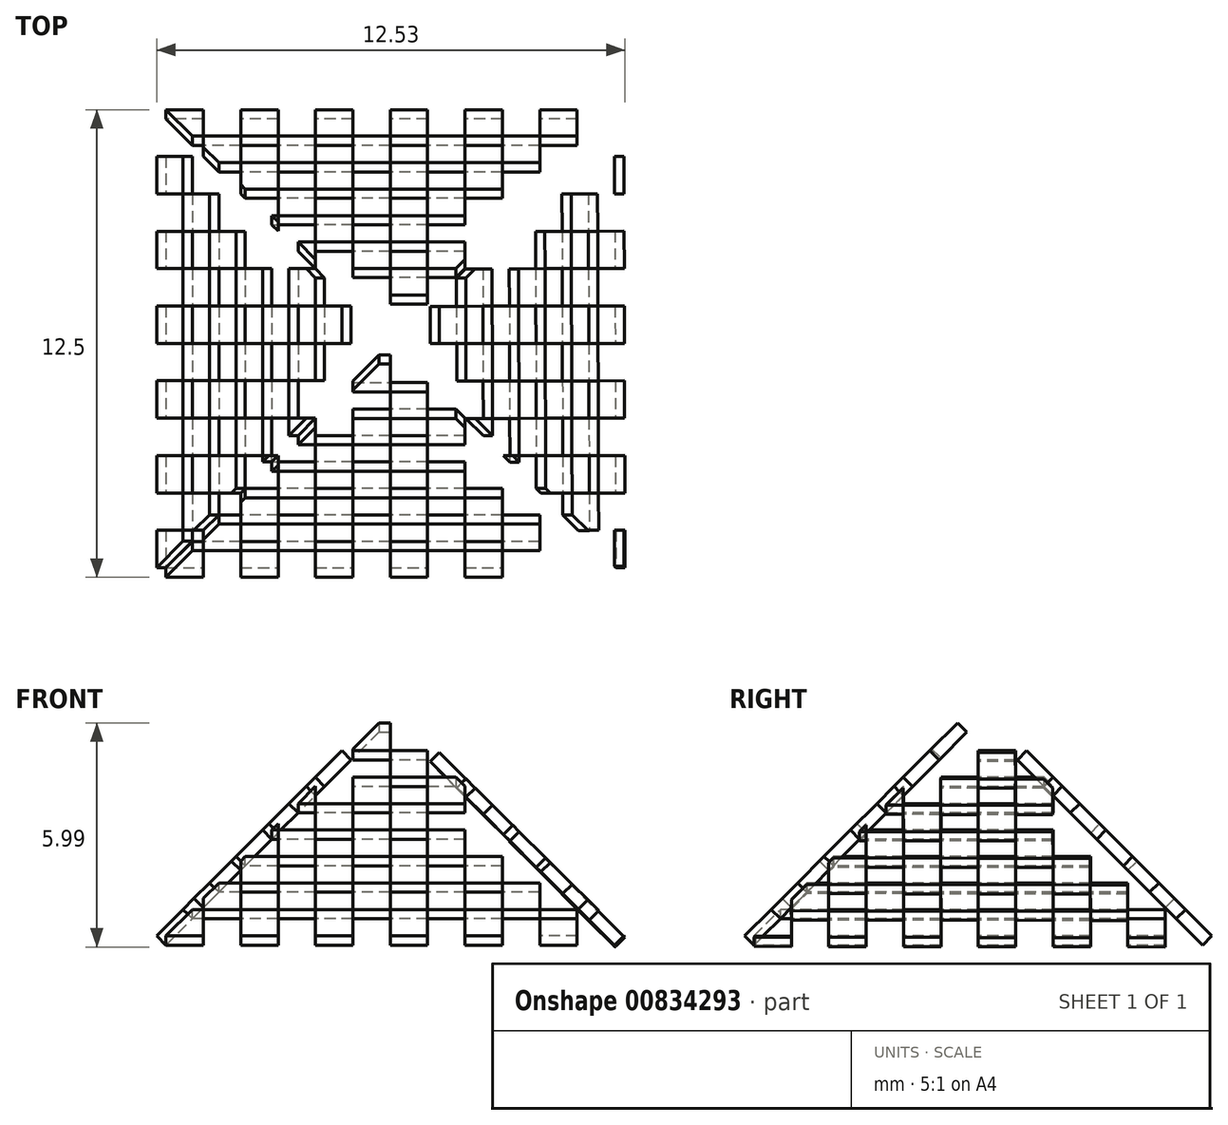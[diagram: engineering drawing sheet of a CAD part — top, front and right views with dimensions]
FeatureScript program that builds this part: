
annotation { "Feature Type Name" : "Feature", "Feature Type Description" : "" }
export const myFeature = defineFeature(function(context is Context, id is Id, definition is map)
    precondition{}
    {
        {
            var Q0;
            Q0=qCreatedBy(makeId("Front.planeOp"),FACE);
            var sketch = newSketch(context, id + "F7", { "sketchPlane" : qUnion([Q0])});
            skLineSegment(sketch, "E0.bottom", {"start": v(0, 0) * mm, "end": v(-1, 0) * mm});
            skLineSegment(sketch, "E0.top", {"start": v(-0.7, 1) * mm, "end": v(-1, 1) * mm});
            skLineSegment(sketch, "E0.right", {"start": v(-1, 0) * mm, "end": v(-1, 1) * mm});
            skLineSegment(sketch, "E1.bottom", {"start": v(-1, 1) * mm, "end": v(-2, 1) * mm});
            skLineSegment(sketch, "E1.left", {"start": v(-1, 1) * mm, "end": v(-1, 0) * mm});
            skLineSegment(sketch, "E1.right", {"start": v(-2, 1) * mm, "end": v(-2, 0) * mm});
            skLineSegment(sketch, "E2.bottom", {"start": v(-2, 1) * mm, "end": v(-3, 1) * mm});
            skLineSegment(sketch, "E2.top", {"start": v(-2, 0) * mm, "end": v(-3, 0) * mm});
            skLineSegment(sketch, "E2.right", {"start": v(-3, 1) * mm, "end": v(-3, 0) * mm});
            skLineSegment(sketch, "E3.bottom", {"start": v(-3, 1) * mm, "end": v(-4, 1) * mm});
            skLineSegment(sketch, "E3.right", {"start": v(-4, 1) * mm, "end": v(-4, 0) * mm});
            skLineSegment(sketch, "E4.bottom", {"start": v(-4, 1) * mm, "end": v(-5, 1) * mm});
            skLineSegment(sketch, "E4.top", {"start": v(-4, 0) * mm, "end": v(-5, 0) * mm});
            skLineSegment(sketch, "E4.right", {"start": v(-5, 1) * mm, "end": v(-5, 0) * mm});
            skLineSegment(sketch, "E5.bottom", {"start": v(-5, 1) * mm, "end": v(-6, 1) * mm});
            skLineSegment(sketch, "E5.right", {"start": v(-6, 1) * mm, "end": v(-6, 0) * mm});
            skLineSegment(sketch, "E6.bottom", {"start": v(-6, 1) * mm, "end": v(-7, 1) * mm});
            skLineSegment(sketch, "E6.top", {"start": v(-6, 0) * mm, "end": v(-7, 0) * mm});
            skLineSegment(sketch, "E6.right", {"start": v(-7, 1) * mm, "end": v(-7, 0) * mm});
            skLineSegment(sketch, "E7.bottom", {"start": v(-7, 1) * mm, "end": v(-8, 1) * mm});
            skLineSegment(sketch, "E7.right", {"start": v(-8, 1) * mm, "end": v(-8, 0) * mm});
            skLineSegment(sketch, "E8.bottom", {"start": v(-8, 1) * mm, "end": v(-9, 1) * mm});
            skLineSegment(sketch, "E8.top", {"start": v(-8, 0) * mm, "end": v(-9, 0) * mm});
            skLineSegment(sketch, "E8.right", {"start": v(-9, 1) * mm, "end": v(-9, 0) * mm});
            skLineSegment(sketch, "E9.bottom", {"start": v(-9, 1) * mm, "end": v(-10, 1) * mm});
            skLineSegment(sketch, "E9.right", {"start": v(-10, 1) * mm, "end": v(-10, 0) * mm});
            skLineSegment(sketch, "E10.bottom", {"start": v(-10, 1) * mm, "end": v(-11, 1) * mm});
            skLineSegment(sketch, "E10.top", {"start": v(-10, 0) * mm, "end": v(-11, 0) * mm});
            skLineSegment(sketch, "E10.right", {"start": v(-11, 1) * mm, "end": v(-11, 0) * mm});
            skLineSegment(sketch, "E11.bottom", {"start": v(-11, 1) * mm, "end": v(-11.3, 1) * mm});
            skLineSegment(sketch, "E12.right", {"start": v(-1, 1) * mm, "end": v(-1, 1.4) * mm});
            skLineSegment(sketch, "E13.bottom", {"start": v(-1.41, 2) * mm, "end": v(-2, 2) * mm});
            skLineSegment(sketch, "E13.left", {"start": v(-1, 1.4) * mm, "end": v(-1, 1) * mm});
            skLineSegment(sketch, "E13.right", {"start": v(-2, 2) * mm, "end": v(-2, 1) * mm});
            skLineSegment(sketch, "E14.bottom", {"start": v(-2, 2) * mm, "end": v(-3, 2) * mm});
            skLineSegment(sketch, "E14.right", {"start": v(-3, 2) * mm, "end": v(-3, 1) * mm});
            skLineSegment(sketch, "E15.bottom", {"start": v(-3, 2) * mm, "end": v(-4, 2) * mm});
            skLineSegment(sketch, "E15.right", {"start": v(-4, 2) * mm, "end": v(-4, 1) * mm});
            skLineSegment(sketch, "E16.bottom", {"start": v(-4, 2) * mm, "end": v(-5, 2) * mm});
            skLineSegment(sketch, "E16.right", {"start": v(-5, 2) * mm, "end": v(-5, 1) * mm});
            skLineSegment(sketch, "E17.bottom", {"start": v(-5, 2) * mm, "end": v(-6, 2) * mm});
            skLineSegment(sketch, "E17.right", {"start": v(-6, 2) * mm, "end": v(-6, 1) * mm});
            skLineSegment(sketch, "E18.right", {"start": v(-7, 2) * mm, "end": v(-7, 1) * mm});
            skLineSegment(sketch, "E19.bottom", {"start": v(-7, 2) * mm, "end": v(-8, 2) * mm});
            skLineSegment(sketch, "E19.right", {"start": v(-8, 2) * mm, "end": v(-8, 1) * mm});
            skLineSegment(sketch, "E20.bottom", {"start": v(-8, 2) * mm, "end": v(-9, 2) * mm});
            skLineSegment(sketch, "E20.right", {"start": v(-9, 2) * mm, "end": v(-9, 1) * mm});
            skLineSegment(sketch, "E21.bottom", {"start": v(-9, 2) * mm, "end": v(-10, 2) * mm});
            skLineSegment(sketch, "E21.right", {"start": v(-10, 2) * mm, "end": v(-10, 1) * mm});
            skLineSegment(sketch, "E22.bottom", {"start": v(-10, 2) * mm, "end": v(-10.59, 2) * mm});
            skLineSegment(sketch, "E22.right", {"start": v(-11, 1.41) * mm, "end": v(-11, 1) * mm});
            skLineSegment(sketch, "E23.right", {"start": v(-2, 2.83) * mm, "end": v(-2, 2) * mm});
            skLineSegment(sketch, "E24.bottom", {"start": v(-2.12, 3) * mm, "end": v(-3, 3) * mm});
            skLineSegment(sketch, "E24.right", {"start": v(-3, 3) * mm, "end": v(-3, 2) * mm});
            skLineSegment(sketch, "E25.bottom", {"start": v(-3, 3) * mm, "end": v(-4, 3) * mm});
            skLineSegment(sketch, "E25.right", {"start": v(-4, 3) * mm, "end": v(-4, 2) * mm});
            skLineSegment(sketch, "E26.bottom", {"start": v(-4, 3) * mm, "end": v(-5, 3) * mm});
            skLineSegment(sketch, "E26.right", {"start": v(-5, 3) * mm, "end": v(-5, 2) * mm});
            skLineSegment(sketch, "E27.right", {"start": v(-6, 3) * mm, "end": v(-6, 2) * mm});
            skLineSegment(sketch, "E28.bottom", {"start": v(-6, 3) * mm, "end": v(-7, 3) * mm});
            skLineSegment(sketch, "E28.top", {"start": v(-6, 2) * mm, "end": v(-7, 2) * mm});
            skLineSegment(sketch, "E28.right", {"start": v(-7, 3) * mm, "end": v(-7, 2) * mm});
            skLineSegment(sketch, "E29.bottom", {"start": v(-7, 3) * mm, "end": v(-8, 3) * mm});
            skLineSegment(sketch, "E29.right", {"start": v(-8, 3) * mm, "end": v(-8, 2) * mm});
            skLineSegment(sketch, "E30.bottom", {"start": v(-8, 3) * mm, "end": v(-9, 3) * mm});
            skLineSegment(sketch, "E30.right", {"start": v(-9, 3) * mm, "end": v(-9, 2) * mm});
            skLineSegment(sketch, "E31.bottom", {"start": v(-9, 3) * mm, "end": v(-9.88, 3) * mm});
            skLineSegment(sketch, "E31.right", {"start": v(-10, 2.83) * mm, "end": v(-10, 2) * mm});
            skLineSegment(sketch, "E32.right", {"start": v(-3, 4) * mm, "end": v(-3, 3) * mm});
            skLineSegment(sketch, "E33.bottom", {"start": v(-3, 4) * mm, "end": v(-4, 4) * mm});
            skLineSegment(sketch, "E33.right", {"start": v(-4, 4) * mm, "end": v(-4, 3) * mm});
            skLineSegment(sketch, "E34.bottom", {"start": v(-4, 4) * mm, "end": v(-5, 4) * mm});
            skLineSegment(sketch, "E34.right", {"start": v(-5, 4) * mm, "end": v(-5, 3) * mm});
            skLineSegment(sketch, "E35.bottom", {"start": v(-5, 4) * mm, "end": v(-6, 4) * mm});
            skLineSegment(sketch, "E35.top", {"start": v(-5, 3) * mm, "end": v(-6, 3) * mm});
            skLineSegment(sketch, "E35.right", {"start": v(-6, 4) * mm, "end": v(-6, 3) * mm});
            skLineSegment(sketch, "E36.bottom", {"start": v(-6, 4) * mm, "end": v(-7, 4) * mm});
            skLineSegment(sketch, "E36.right", {"start": v(-7, 4) * mm, "end": v(-7, 3) * mm});
            skLineSegment(sketch, "E37.bottom", {"start": v(-7, 4) * mm, "end": v(-8, 4) * mm});
            skLineSegment(sketch, "E37.right", {"start": v(-8, 4) * mm, "end": v(-8, 3) * mm});
            skLineSegment(sketch, "E38.bottom", {"start": v(-8, 4) * mm, "end": v(-9, 4) * mm});
            skLineSegment(sketch, "E38.right", {"start": v(-9, 4) * mm, "end": v(-9, 3) * mm});
            skLineSegment(sketch, "E39.right", {"start": v(-4, 5) * mm, "end": v(-4, 4) * mm});
            skLineSegment(sketch, "E40.bottom", {"start": v(-4, 5) * mm, "end": v(-5, 5) * mm});
            skLineSegment(sketch, "E40.right", {"start": v(-5, 5) * mm, "end": v(-5, 4) * mm});
            skLineSegment(sketch, "E41.bottom", {"start": v(-5, 5) * mm, "end": v(-6, 5) * mm});
            skLineSegment(sketch, "E41.right", {"start": v(-6, 5) * mm, "end": v(-6, 4) * mm});
            skLineSegment(sketch, "E42.bottom", {"start": v(-6, 5) * mm, "end": v(-7, 5) * mm});
            skLineSegment(sketch, "E42.right", {"start": v(-7, 5) * mm, "end": v(-7, 4) * mm});
            skLineSegment(sketch, "E43.bottom", {"start": v(-7, 5) * mm, "end": v(-8, 5) * mm});
            skLineSegment(sketch, "E43.right", {"start": v(-8, 5) * mm, "end": v(-8, 4) * mm});
            skLineSegment(sketch, "E44.right", {"start": v(-5, 6) * mm, "end": v(-5, 5) * mm});
            skLineSegment(sketch, "E45.bottom", {"start": v(-5, 6) * mm, "end": v(-6, 6) * mm});
            skLineSegment(sketch, "E45.right", {"start": v(-6, 6) * mm, "end": v(-6, 5) * mm});
            skLineSegment(sketch, "E46.right", {"start": v(-7, 6) * mm, "end": v(-7, 5) * mm});
            skLineSegment(sketch, "E47.top", {"start": v(-2, 2) * mm, "end": v(-1.41, 2) * mm});
            skLineSegment(sketch, "E48.bottom", {"start": v(-3, 4) * mm, "end": v(-2.83, 4) * mm});
            skLineSegment(sketch, "E48.top", {"start": v(-3, 3) * mm, "end": v(-2.12, 3) * mm});
            skLineSegment(sketch, "E49.bottom", {"start": v(-4, 5) * mm, "end": v(-3.54, 5) * mm});
            skLineSegment(sketch, "E49.top", {"start": v(-4, 4) * mm, "end": v(-3, 4) * mm});
            skLineSegment(sketch, "E49.right", {"start": v(-3, 4.24) * mm, "end": v(-3, 4) * mm});
            skLineSegment(sketch, "E50.top", {"start": v(-4.24, 6) * mm, "end": v(-5, 6) * mm});
            skLineSegment(sketch, "E50.left", {"start": v(-4, 5) * mm, "end": v(-4, 5.65) * mm});
            skLineSegment(sketch, "E50.right", {"start": v(-5, 5) * mm, "end": v(-5, 6) * mm});
            skLineSegment(sketch, "E51.right", {"start": v(-5, 6) * mm, "end": v(-5, 7) * mm});
            skLineSegment(sketch, "E52.bottom", {"start": v(-8, 5) * mm, "end": v(-7, 5) * mm});
            skLineSegment(sketch, "E52.top", {"start": v(-7.76, 6) * mm, "end": v(-7, 6) * mm});
            skLineSegment(sketch, "E52.right", {"start": v(-7, 5) * mm, "end": v(-7, 6) * mm});
            skLineSegment(sketch, "E53.bottom", {"start": v(-5, 7) * mm, "end": v(-6, 7) * mm});
            skLineSegment(sketch, "E53.left", {"start": v(-5, 7) * mm, "end": v(-5, 6) * mm});
            skLineSegment(sketch, "E53.right", {"start": v(-6, 7) * mm, "end": v(-6, 6) * mm});
            skLineSegment(sketch, "E54.top", {"start": v(-6, 6) * mm, "end": v(-7, 6) * mm});
            skLineSegment(sketch, "E54.right", {"start": v(-7, 7) * mm, "end": v(-7, 6) * mm});
            skLineSegment(sketch, "E55.top", {"start": v(-7, 6) * mm, "end": v(-7.76, 6) * mm});
            skLineSegment(sketch, "E56.right", {"start": v(-5, 7) * mm, "end": v(-5, 7.07) * mm});
            skLineSegment(sketch, "E57.bottom", {"start": v(-6, 7) * mm, "end": v(-5, 7) * mm});
            skLineSegment(sketch, "E57.top", {"start": v(-6, 8.05) * mm, "end": v(-5.7, 8.05) * mm});
            skLineSegment(sketch, "E57.left", {"start": v(-6, 7) * mm, "end": v(-6, 8.05) * mm});
            skLineSegment(sketch, "E58.bottom", {"start": v(-7, 7) * mm, "end": v(-6, 7) * mm});
            skLineSegment(sketch, "E58.top", {"start": v(-6.3, 8.05) * mm, "end": v(-6, 8.05) * mm});
            skLineSegment(sketch, "E58.left", {"start": v(-7, 7) * mm, "end": v(-7, 7.07) * mm});
            skLineSegment(sketch, "E59.bottom", {"start": v(-10.59, 2) * mm, "end": v(-10, 2) * mm});
            skLineSegment(sketch, "E59.right", {"start": v(-10, 2) * mm, "end": v(-10, 2.83) * mm});
            skLineSegment(sketch, "E60.bottom", {"start": v(-9.88, 3) * mm, "end": v(-9, 3) * mm});
            skLineSegment(sketch, "E60.top", {"start": v(-9.17, 4) * mm, "end": v(-9, 4) * mm});
            skLineSegment(sketch, "E60.right", {"start": v(-9, 3) * mm, "end": v(-9, 4) * mm});
            skLineSegment(sketch, "E61.bottom", {"start": v(-9, 4) * mm, "end": v(-8, 4) * mm});
            skLineSegment(sketch, "E61.top", {"start": v(-8.46, 5) * mm, "end": v(-8, 5) * mm});
            skLineSegment(sketch, "E61.left", {"start": v(-9, 4) * mm, "end": v(-9, 4.24) * mm});
            skLineSegment(sketch, "E61.right", {"start": v(-8, 4) * mm, "end": v(-8, 5) * mm});
            skLineSegment(sketch, "E62.right", {"start": v(-8, 5) * mm, "end": v(-8, 5.65) * mm});
            skLineSegment(sketch, "E63.bottom", {"start": v(-11.3, 1) * mm, "end": v(-11, 1) * mm});
            skLineSegment(sketch, "E63.right", {"start": v(-11, 1) * mm, "end": v(-11, 1.41) * mm});
            skLineSegment(sketch, "E64.bottom", {"start": v(-2.83, 4) * mm, "end": v(-3, 4) * mm});
            skLineSegment(sketch, "E64.right", {"start": v(-3, 4) * mm, "end": v(-3, 4.24) * mm});
            skLineSegment(sketch, "E65.left", {"start": v(-4, 5.65) * mm, "end": v(-4, 5) * mm});
            skLineSegment(sketch, "E66.bottom", {"start": v(-7, 7) * mm, "end": v(-7.05, 7) * mm});
            skLineSegment(sketch, "E67.bottom", {"start": v(-7.05, 7) * mm, "end": v(-7, 7) * mm});
            skLineSegment(sketch, "E68.bottom", {"start": v(-4.95, 7) * mm, "end": v(-5, 7) * mm});
            skLineSegment(sketch, "E69.bottom", {"start": v(-5.7, 8.05) * mm, "end": v(-6, 8.05) * mm});
            skLineSegment(sketch, "E69.right", {"start": v(-6, 8.05) * mm, "end": v(-6, 8.48) * mm});
            skLineSegment(sketch, "E70", {"start": v(-12, 0) * mm, "end": v(-11, 1.41) * mm});
            skLineSegment(sketch, "E71", {"start": v(-5.7, 8.05) * mm, "end": v(-5, 7.07) * mm});
            skLineSegment(sketch, "E72.trimOffspring", {"start": v(-10.59, 2) * mm, "end": v(-10, 2.83) * mm});
            skLineSegment(sketch, "E73.trimOffspring", {"start": v(-9.88, 3) * mm, "end": v(-9.17, 4) * mm});
            skLineSegment(sketch, "E74.trimOffspring", {"start": v(-9, 4.24) * mm, "end": v(-8.46, 5) * mm});
            skLineSegment(sketch, "E75.trimOffspring", {"start": v(-8, 5.65) * mm, "end": v(-7.76, 6) * mm});
            skLineSegment(sketch, "E76.trimOffspring", {"start": v(-7.05, 7) * mm, "end": v(-7, 7.07) * mm});
            skLineSegment(sketch, "E77.trimOffspring", {"start": v(-6.3, 8.05) * mm, "end": v(-6, 8.48) * mm});
            skLineSegment(sketch, "E78.trimOffspring", {"start": v(-4.95, 7) * mm, "end": v(-4.24, 6) * mm});
            skLineSegment(sketch, "E79.trimOffspring", {"start": v(-0.7, 1) * mm, "end": v(0, 0) * mm});
            skLineSegment(sketch, "E80.trimOffspring", {"start": v(-1.41, 2) * mm, "end": v(-1, 1.4) * mm});
            skLineSegment(sketch, "E81.trimOffspring", {"start": v(-2.12, 3) * mm, "end": v(-2, 2.83) * mm});
            skLineSegment(sketch, "E82.trimOffspring", {"start": v(-3, 4.24) * mm, "end": v(-2.83, 4) * mm});
            skLineSegment(sketch, "E83.trimOffspring", {"start": v(-4, 5.65) * mm, "end": v(-3.54, 5) * mm});
            skLineSegment(sketch, "E84", {"start": v(-6, 8.48) * mm, "end": v(0, 0) * mm});
            skLineSegment(sketch, "E85", {"start": v(-6, 8.48) * mm, "end": v(-12, 0) * mm});
            skLineSegment(sketch, "E86", {"start": v(-12, 0) * mm, "end": v(0, 0) * mm});
            skSolve(sketch);
        }
        {
            var Q0;
            {var subQ0=sQuery(id+"F7.wireOp",EDGE,"E10.right");Q0=makeQuery(id+"F7.imprint","IMPRINT",FACE,{"disambiguationData":[TD([[makeQuery(id+"F7.imprint","IMPRINT",EDGE,{"derivedFrom":subQ0}),-1.0]])]});}
            var Q1;
            Q1=makeQuery(id+"F7.imprint","IMPRINT",FACE,{"disambiguationData":[TD([[makeQuery(id+"F7.imprint","IMPRINT",EDGE,{"derivedFrom":sQuery(id+"F7.wireOp",EDGE,"E10.bottom")}),-1.0]])]});
            var Q2;
            Q2=makeQuery(id+"F7.imprint","IMPRINT",FACE,{"disambiguationData":[TD([[makeQuery(id+"F7.imprint","IMPRINT",EDGE,{"derivedFrom":sQuery(id+"F7.wireOp",EDGE,"E21.bottom")}),-1.0]])]});
            var Q3;
            {var subQ0=sQuery(id+"F7.wireOp",EDGE,"E8.right");Q3=makeQuery(id+"F7.imprint","IMPRINT",FACE,{"disambiguationData":[TD([[makeQuery(id+"F7.imprint","IMPRINT",EDGE,{"derivedFrom":subQ0}),-1.0]])]});}
            var Q4;
            Q4=makeQuery(id+"F7.imprint","IMPRINT",FACE,{"disambiguationData":[TD([[makeQuery(id+"F7.imprint","IMPRINT",EDGE,{"derivedFrom":sQuery(id+"F7.wireOp",EDGE,"E8.bottom")}),-1.0]])]});
            var Q5;
            Q5=makeQuery(id+"F7.imprint","IMPRINT",FACE,{"disambiguationData":[TD([[makeQuery(id+"F7.imprint","IMPRINT",EDGE,{"derivedFrom":sQuery(id+"F7.wireOp",EDGE,"E19.bottom")}),-1.0]])]});
            var Q6;
            Q6=makeQuery(id+"F7.imprint","IMPRINT",FACE,{"disambiguationData":[TD([[makeQuery(id+"F7.imprint","IMPRINT",EDGE,{"derivedFrom":sQuery(id+"F7.wireOp",EDGE,"E30.bottom")}),-1.0]])]});
            var Q7;
            Q7=makeQuery(id+"F7.imprint","IMPRINT",FACE,{"disambiguationData":[TD([[makeQuery(id+"F7.imprint","IMPRINT",EDGE,{"derivedFrom":sQuery(id+"F7.wireOp",EDGE,"E37.bottom")}),-1.0]])]});
            var Q8;
            {var subQ0=sQuery(id+"F7.wireOp",EDGE,"E61.top");Q8=makeQuery(id+"F7.imprint","IMPRINT",FACE,{"disambiguationData":[TD([[makeQuery(id+"F7.imprint","IMPRINT",EDGE,{"derivedFrom":subQ0}),1.0]])]});}
            var Q9;
            Q9=makeQuery(id+"F7.imprint","IMPRINT",FACE,{"disambiguationData":[TD([[makeQuery(id+"F7.imprint","IMPRINT",EDGE,{"derivedFrom":sQuery(id+"F7.wireOp",EDGE,"E42.bottom")}),-1.0]])]});
            var Q10;
            {var subQ0=sQuery(id+"F7.wireOp",EDGE,"E55.top");Q10=makeQuery(id+"F7.imprint","IMPRINT",FACE,{"disambiguationData":[TD([[makeQuery(id+"F7.imprint","IMPRINT",EDGE,{"derivedFrom":subQ0}),-1.0]])]});}
            var Q11;
            Q11=makeQuery(id+"F7.imprint","IMPRINT",FACE,{"disambiguationData":[TD([[makeQuery(id+"F7.imprint","IMPRINT",EDGE,{"derivedFrom":sQuery(id+"F7.wireOp",EDGE,"E58.bottom")}),1.0]])]});
            var Q12;
            {var subQ0=sQuery(id+"F7.wireOp",EDGE,"E69.bottom");Q12=makeQuery(id+"F7.imprint","IMPRINT",FACE,{"disambiguationData":[TD([[makeQuery(id+"F7.imprint","IMPRINT",EDGE,{"derivedFrom":subQ0}),-1.0]])]});}
            var Q13;
            Q13=makeQuery(id+"F7.imprint","IMPRINT",FACE,{"disambiguationData":[TD([[makeQuery(id+"F7.imprint","IMPRINT",EDGE,{"derivedFrom":sQuery(id+"F7.wireOp",EDGE,"E45.bottom")}),-1.0]])]});
            var Q14;
            Q14=makeQuery(id+"F7.imprint","IMPRINT",FACE,{"disambiguationData":[TD([[makeQuery(id+"F7.imprint","IMPRINT",EDGE,{"derivedFrom":sQuery(id+"F7.wireOp",EDGE,"E40.bottom")}),-1.0]])]});
            var Q15;
            Q15=makeQuery(id+"F7.imprint","IMPRINT",FACE,{"disambiguationData":[TD([[makeQuery(id+"F7.imprint","IMPRINT",EDGE,{"derivedFrom":sQuery(id+"F7.wireOp",EDGE,"E35.bottom")}),-1.0]])]});
            var Q16;
            Q16=makeQuery(id+"F7.imprint","IMPRINT",FACE,{"disambiguationData":[TD([[makeQuery(id+"F7.imprint","IMPRINT",EDGE,{"derivedFrom":sQuery(id+"F7.wireOp",EDGE,"E28.bottom")}),-1.0]])]});
            var Q17;
            Q17=makeQuery(id+"F7.imprint","IMPRINT",FACE,{"disambiguationData":[TD([[makeQuery(id+"F7.imprint","IMPRINT",EDGE,{"derivedFrom":sQuery(id+"F7.wireOp",EDGE,"E17.bottom")}),-1.0]])]});
            var Q18;
            Q18=makeQuery(id+"F7.imprint","IMPRINT",FACE,{"disambiguationData":[TD([[makeQuery(id+"F7.imprint","IMPRINT",EDGE,{"derivedFrom":sQuery(id+"F7.wireOp",EDGE,"E6.bottom")}),-1.0]])]});
            var Q19;
            {var subQ0=sQuery(id+"F7.wireOp",EDGE,"E6.right");Q19=makeQuery(id+"F7.imprint","IMPRINT",FACE,{"disambiguationData":[TD([[makeQuery(id+"F7.imprint","IMPRINT",EDGE,{"derivedFrom":subQ0}),-1.0]])]});}
            var Q20;
            Q20=makeQuery(id+"F7.imprint","IMPRINT",FACE,{"disambiguationData":[TD([[makeQuery(id+"F7.imprint","IMPRINT",EDGE,{"derivedFrom":sQuery(id+"F7.wireOp",EDGE,"E26.bottom")}),-1.0]])]});
            var Q21;
            Q21=makeQuery(id+"F7.imprint","IMPRINT",FACE,{"disambiguationData":[TD([[makeQuery(id+"F7.imprint","IMPRINT",EDGE,{"derivedFrom":sQuery(id+"F7.wireOp",EDGE,"E49.top")}),1.0]])]});
            var Q22;
            {var subQ0=sQuery(id+"F7.wireOp",EDGE,"E48.top");Q22=makeQuery(id+"F7.imprint","IMPRINT",FACE,{"disambiguationData":[TD([[makeQuery(id+"F7.imprint","IMPRINT",EDGE,{"derivedFrom":subQ0}),1.0]])]});}
            var Q23;
            Q23=makeQuery(id+"F7.imprint","IMPRINT",FACE,{"disambiguationData":[TD([[makeQuery(id+"F7.imprint","IMPRINT",EDGE,{"derivedFrom":sQuery(id+"F7.wireOp",EDGE,"E15.bottom")}),-1.0]])]});
            var Q24;
            Q24=makeQuery(id+"F7.imprint","IMPRINT",FACE,{"disambiguationData":[TD([[makeQuery(id+"F7.imprint","IMPRINT",EDGE,{"derivedFrom":sQuery(id+"F7.wireOp",EDGE,"E4.bottom")}),-1.0]])]});
            var Q25;
            {var subQ0=sQuery(id+"F7.wireOp",EDGE,"E4.right");Q25=makeQuery(id+"F7.imprint","IMPRINT",FACE,{"disambiguationData":[TD([[makeQuery(id+"F7.imprint","IMPRINT",EDGE,{"derivedFrom":subQ0}),-1.0]])]});}
            var Q26;
            {var subQ0=sQuery(id+"F7.wireOp",EDGE,"E2.right");Q26=makeQuery(id+"F7.imprint","IMPRINT",FACE,{"disambiguationData":[TD([[makeQuery(id+"F7.imprint","IMPRINT",EDGE,{"derivedFrom":subQ0}),-1.0]])]});}
            var Q27;
            Q27=makeQuery(id+"F7.imprint","IMPRINT",FACE,{"disambiguationData":[TD([[makeQuery(id+"F7.imprint","IMPRINT",EDGE,{"derivedFrom":sQuery(id+"F7.wireOp",EDGE,"E2.bottom")}),-1.0]])]});
            var Q28;
            {var subQ0=sQuery(id+"F7.wireOp",EDGE,"E47.top");Q28=makeQuery(id+"F7.imprint","IMPRINT",FACE,{"disambiguationData":[TD([[makeQuery(id+"F7.imprint","IMPRINT",EDGE,{"derivedFrom":subQ0}),1.0]])]});}
            var Q29;
            {var subQ0=sQuery(id+"F7.wireOp",EDGE,"E0.top");Q29=makeQuery(id+"F7.imprint","IMPRINT",FACE,{"disambiguationData":[TD([[makeQuery(id+"F7.imprint","IMPRINT",EDGE,{"derivedFrom":subQ0}),-1.0]])]});}
            var Q30;
            {var subQ0=sQuery(id+"F7.wireOp",EDGE,"E1.left");Q30=makeQuery(id+"F7.imprint","IMPRINT",FACE,{"disambiguationData":[TD([[makeQuery(id+"F7.imprint","IMPRINT",EDGE,{"derivedFrom":subQ0}),-1.0]])]});}
            var Q31;
            {var subQ0=sQuery(id+"F7.wireOp",EDGE,"E60.top");Q31=makeQuery(id+"F7.imprint","IMPRINT",FACE,{"disambiguationData":[TD([[makeQuery(id+"F7.imprint","IMPRINT",EDGE,{"derivedFrom":subQ0}),1.0]])]});}
            extrude(context, id + "F8", {"entities" : qUnion([Q0, Q1, Q2, Q3, Q4, Q5, Q6, Q7, Q8, Q9, Q10, Q11, Q12, Q13, Q14, Q15, Q16, Q17, Q18, Q19, Q20, Q21, Q22, Q23, Q24, Q25, Q26, Q27, Q28, Q29, Q30, Q31]), "depth" : 0.35 * mm, "offsetDistance" : 25.4 * mm});
        }
        {
            var Q0;
            Q0=makeQuery(id+"FwjZak2WU2AujaI_0.opExtrude","SWEPT_BODY",BODY,{"disambiguationData":[OSD([sQuery(id+"F7.wireOp",EDGE,"E59.bottom"),sQuery(id+"F7.wireOp",EDGE,"E59.right"),sQuery(id+"F7.wireOp",EDGE,"E85")])]});
            var Q1;
            Q1=makeQuery(id+"FwjZak2WU2AujaI_0.opExtrude","SWEPT_BODY",BODY,{"disambiguationData":[OSD([sQuery(id+"F7.wireOp",EDGE,"E60.bottom"),sQuery(id+"F7.wireOp",EDGE,"E60.right"),sQuery(id+"F7.wireOp",EDGE,"E60.top"),sQuery(id+"F7.wireOp",EDGE,"E85")])]});
            var Q2;
            Q2=makeQuery(id+"FwjZak2WU2AujaI_0.opExtrude","SWEPT_BODY",BODY,{"disambiguationData":[OSD([sQuery(id+"F7.wireOp",EDGE,"E57.bottom"),sQuery(id+"F7.wireOp",EDGE,"E57.left"),sQuery(id+"F7.wireOp",EDGE,"E56.right"),sQuery(id+"F7.wireOp",EDGE,"E69.bottom"),sQuery(id+"F7.wireOp",EDGE,"E84")])]});
            var Q3;
            Q3=makeQuery(id+"FwjZak2WU2AujaI_0.opExtrude","SWEPT_BODY",BODY,{"disambiguationData":[OSD([sQuery(id+"F7.wireOp",EDGE,"E54.top"),sQuery(id+"F7.wireOp",EDGE,"E53.right"),sQuery(id+"F7.wireOp",EDGE,"E58.bottom"),sQuery(id+"F7.wireOp",EDGE,"E54.right")])]});
            var Q4;
            Q4=makeQuery(id+"FwjZak2WU2AujaI_0.opExtrude","SWEPT_BODY",BODY,{"disambiguationData":[OSD([sQuery(id+"F7.wireOp",EDGE,"E67.bottom"),sQuery(id+"F7.wireOp",EDGE,"E58.left"),sQuery(id+"F7.wireOp",EDGE,"E85")])]});
            var Q5;
            Q5=makeQuery(id+"FwjZak2WU2AujaI_0.opExtrude","SWEPT_BODY",BODY,{"disambiguationData":[OSD([sQuery(id+"F7.wireOp",EDGE,"E52.bottom"),sQuery(id+"F7.wireOp",EDGE,"E52.right"),sQuery(id+"F7.wireOp",EDGE,"E62.right"),sQuery(id+"F7.wireOp",EDGE,"E55.top"),sQuery(id+"F7.wireOp",EDGE,"E85")])]});
            var Q6;
            Q6=makeQuery(id+"FwjZak2WU2AujaI_0.opExtrude","SWEPT_BODY",BODY,{"disambiguationData":[OSD([sQuery(id+"F7.wireOp",EDGE,"E63.bottom"),sQuery(id+"F7.wireOp",EDGE,"E63.right"),sQuery(id+"F7.wireOp",EDGE,"E85")])]});
            var Q7;
            Q7=makeQuery(id+"FwjZak2WU2AujaI_0.opExtrude","SWEPT_BODY",BODY,{"disambiguationData":[OSD([sQuery(id+"F7.wireOp",EDGE,"E48.bottom"),sQuery(id+"F7.wireOp",EDGE,"E49.right"),sQuery(id+"F7.wireOp",EDGE,"E84")])]});
            var Q8;
            Q8=makeQuery(id+"FwjZak2WU2AujaI_0.opExtrude","SWEPT_BODY",BODY,{"disambiguationData":[OSD([sQuery(id+"F7.wireOp",EDGE,"E49.bottom"),sQuery(id+"F7.wireOp",EDGE,"E65.left"),sQuery(id+"F7.wireOp",EDGE,"E84")])]});
            var Q9;
            Q9=makeQuery(id+"FwjZak2WU2AujaI_0.opExtrude","SWEPT_BODY",BODY,{"disambiguationData":[OSD([sQuery(id+"F7.wireOp",EDGE,"E61.bottom"),sQuery(id+"F7.wireOp",EDGE,"E61.right"),sQuery(id+"F7.wireOp",EDGE,"E61.left"),sQuery(id+"F7.wireOp",EDGE,"E61.top"),sQuery(id+"F7.wireOp",EDGE,"E85")])]});
            var Q10;
            Q10=makeQuery(id+"FwjZak2WU2AujaI_0.opExtrude","SWEPT_BODY",BODY,{"disambiguationData":[OSD([sQuery(id+"F7.wireOp",EDGE,"E35.top"),sQuery(id+"F7.wireOp",EDGE,"E34.right"),sQuery(id+"F7.wireOp",EDGE,"E35.right"),sQuery(id+"F7.wireOp",EDGE,"E35.bottom")])]});
            var Q11;
            Q11=makeQuery(id+"FwjZak2WU2AujaI_0.opExtrude","SWEPT_BODY",BODY,{"disambiguationData":[OSD([sQuery(id+"F7.wireOp",EDGE,"E29.bottom"),sQuery(id+"F7.wireOp",EDGE,"E36.right"),sQuery(id+"F7.wireOp",EDGE,"E37.right"),sQuery(id+"F7.wireOp",EDGE,"E37.bottom")])]});
            var Q12;
            Q12=makeQuery(id+"FwjZak2WU2AujaI_0.opExtrude","SWEPT_BODY",BODY,{"disambiguationData":[OSD([sQuery(id+"F7.wireOp",EDGE,"E34.bottom"),sQuery(id+"F7.wireOp",EDGE,"E40.right"),sQuery(id+"F7.wireOp",EDGE,"E39.right"),sQuery(id+"F7.wireOp",EDGE,"E40.bottom")])]});
            var Q13;
            Q13=makeQuery(id+"FwjZak2WU2AujaI_0.opExtrude","SWEPT_BODY",BODY,{"disambiguationData":[OSD([sQuery(id+"F7.wireOp",EDGE,"E41.bottom"),sQuery(id+"F7.wireOp",EDGE,"E45.right"),sQuery(id+"F7.wireOp",EDGE,"E50.right"),sQuery(id+"F7.wireOp",EDGE,"E45.bottom")])]});
            var Q14;
            Q14=makeQuery(id+"FwjZak2WU2AujaI_0.opExtrude","SWEPT_BODY",BODY,{"disambiguationData":[OSD([sQuery(id+"F7.wireOp",EDGE,"E16.bottom"),sQuery(id+"F7.wireOp",EDGE,"E25.right"),sQuery(id+"F7.wireOp",EDGE,"E26.right"),sQuery(id+"F7.wireOp",EDGE,"E26.bottom")])]});
            var Q15;
            Q15=makeQuery(id+"FwjZak2WU2AujaI_0.opExtrude","SWEPT_BODY",BODY,{"disambiguationData":[OSD([sQuery(id+"F7.wireOp",EDGE,"E20.bottom"),sQuery(id+"F7.wireOp",EDGE,"E29.right"),sQuery(id+"F7.wireOp",EDGE,"E30.right"),sQuery(id+"F7.wireOp",EDGE,"E30.bottom")])]});
            var Q16;
            Q16=makeQuery(id+"FwjZak2WU2AujaI_0.opExtrude","SWEPT_BODY",BODY,{"disambiguationData":[OSD([sQuery(id+"F7.wireOp",EDGE,"E28.top"),sQuery(id+"F7.wireOp",EDGE,"E27.right"),sQuery(id+"F7.wireOp",EDGE,"E28.right"),sQuery(id+"F7.wireOp",EDGE,"E28.bottom")])]});
            var Q17;
            Q17=makeQuery(id+"FwjZak2WU2AujaI_0.opExtrude","SWEPT_BODY",BODY,{"disambiguationData":[OSD([sQuery(id+"F7.wireOp",EDGE,"E36.bottom"),sQuery(id+"F7.wireOp",EDGE,"E41.right"),sQuery(id+"F7.wireOp",EDGE,"E42.right"),sQuery(id+"F7.wireOp",EDGE,"E42.bottom")])]});
            var Q18;
            Q18=makeQuery(id+"FwjZak2WU2AujaI_0.opExtrude","SWEPT_BODY",BODY,{"disambiguationData":[OSD([sQuery(id+"F7.wireOp",EDGE,"E9.bottom"),sQuery(id+"F7.wireOp",EDGE,"E20.right"),sQuery(id+"F7.wireOp",EDGE,"E21.right"),sQuery(id+"F7.wireOp",EDGE,"E21.bottom")])]});
            var Q19;
            Q19=makeQuery(id+"FwjZak2WU2AujaI_0.opExtrude","SWEPT_BODY",BODY,{"disambiguationData":[OSD([sQuery(id+"F7.wireOp",EDGE,"E25.bottom"),sQuery(id+"F7.wireOp",EDGE,"E33.right"),sQuery(id+"F7.wireOp",EDGE,"E32.right"),sQuery(id+"F7.wireOp",EDGE,"E49.top")])]});
            var Q20;
            Q20=makeQuery(id+"FwjZak2WU2AujaI_0.opExtrude","SWEPT_BODY",BODY,{"disambiguationData":[OSD([sQuery(id+"F7.wireOp",EDGE,"E14.bottom"),sQuery(id+"F7.wireOp",EDGE,"E24.right"),sQuery(id+"F7.wireOp",EDGE,"E23.right"),sQuery(id+"F7.wireOp",EDGE,"E48.top"),sQuery(id+"F7.wireOp",EDGE,"E84")])]});
            var Q21;
            Q21=makeQuery(id+"FwjZak2WU2AujaI_0.opExtrude","SWEPT_BODY",BODY,{"disambiguationData":[OSD([sQuery(id+"F7.wireOp",EDGE,"E50.top"),sQuery(id+"F7.wireOp",EDGE,"E53.left"),sQuery(id+"F7.wireOp",EDGE,"E68.bottom"),sQuery(id+"F7.wireOp",EDGE,"E84")])]});
            var Q22;
            Q22=makeQuery(id+"FwjZak2WU2AujaI_0.opExtrude","SWEPT_BODY",BODY,{"disambiguationData":[OSD([sQuery(id+"F7.wireOp",EDGE,"E3.bottom"),sQuery(id+"F7.wireOp",EDGE,"E14.right"),sQuery(id+"F7.wireOp",EDGE,"E15.right"),sQuery(id+"F7.wireOp",EDGE,"E15.bottom")])]});
            var Q23;
            Q23=makeQuery(id+"F8.opExtrude","SWEPT_BODY",BODY,{"disambiguationData":[OSD([sQuery(id+"F7.wireOp",EDGE,"E2.right"),sQuery(id+"F7.wireOp",EDGE,"E3.right"),sQuery(id+"F7.wireOp",EDGE,"E3.bottom"),sQuery(id+"F7.wireOp",EDGE,"E86")])]});
            var Q24;
            Q24=makeQuery(id+"FwjZak2WU2AujaI_0.opExtrude","SWEPT_BODY",BODY,{"disambiguationData":[OSD([sQuery(id+"F7.wireOp",EDGE,"E9.right"),sQuery(id+"F7.wireOp",EDGE,"E10.right"),sQuery(id+"F7.wireOp",EDGE,"E10.bottom"),sQuery(id+"F7.wireOp",EDGE,"E86")])]});
            var Q25;
            Q25=makeQuery(id+"FwjZak2WU2AujaI_0.opExtrude","SWEPT_BODY",BODY,{"disambiguationData":[OSD([sQuery(id+"F7.wireOp",EDGE,"E5.right"),sQuery(id+"F7.wireOp",EDGE,"E6.right"),sQuery(id+"F7.wireOp",EDGE,"E6.bottom"),sQuery(id+"F7.wireOp",EDGE,"E86")])]});
            var Q26;
            Q26=makeQuery(id+"FwjZak2WU2AujaI_0.opExtrude","SWEPT_BODY",BODY,{"disambiguationData":[OSD([sQuery(id+"F7.wireOp",EDGE,"E7.right"),sQuery(id+"F7.wireOp",EDGE,"E8.right"),sQuery(id+"F7.wireOp",EDGE,"E8.bottom"),sQuery(id+"F7.wireOp",EDGE,"E86")])]});
            var Q27;
            Q27=makeQuery(id+"FwjZak2WU2AujaI_0.opExtrude","SWEPT_BODY",BODY,{"disambiguationData":[OSD([sQuery(id+"F7.wireOp",EDGE,"E1.right"),sQuery(id+"F7.wireOp",EDGE,"E2.right"),sQuery(id+"F7.wireOp",EDGE,"E2.bottom"),sQuery(id+"F7.wireOp",EDGE,"E86")])]});
            var Q28;
            Q28=makeQuery(id+"FwjZak2WU2AujaI_0.opExtrude","SWEPT_BODY",BODY,{"disambiguationData":[OSD([sQuery(id+"F7.wireOp",EDGE,"E3.right"),sQuery(id+"F7.wireOp",EDGE,"E4.right"),sQuery(id+"F7.wireOp",EDGE,"E4.bottom"),sQuery(id+"F7.wireOp",EDGE,"E86")])]});
            var Q29;
            Q29=makeQuery(id+"FwjZak2WU2AujaI_0.opExtrude","SWEPT_BODY",BODY,{"disambiguationData":[OSD([sQuery(id+"F7.wireOp",EDGE,"E1.left"),sQuery(id+"F7.wireOp",EDGE,"E1.bottom"),sQuery(id+"F7.wireOp",EDGE,"E13.right"),sQuery(id+"F7.wireOp",EDGE,"E0.top"),sQuery(id+"F7.wireOp",EDGE,"E12.right"),sQuery(id+"F7.wireOp",EDGE,"E47.top"),sQuery(id+"F7.wireOp",EDGE,"E84"),sQuery(id+"F7.wireOp",EDGE,"E86")])]});
            var Q30;
            Q30=makeQuery(id+"F8.opExtrude","SWEPT_BODY",BODY,{"disambiguationData":[OSD([sQuery(id+"F7.wireOp",EDGE,"E6.right"),sQuery(id+"F7.wireOp",EDGE,"E7.right"),sQuery(id+"F7.wireOp",EDGE,"E7.bottom"),sQuery(id+"F7.wireOp",EDGE,"E86")])]});
            var Q31;
            Q31=makeQuery(id+"F8.opExtrude","SWEPT_BODY",BODY,{"disambiguationData":[OSD([sQuery(id+"F7.wireOp",EDGE,"E1.left"),sQuery(id+"F7.wireOp",EDGE,"E1.right"),sQuery(id+"F7.wireOp",EDGE,"E1.bottom"),sQuery(id+"F7.wireOp",EDGE,"E86")])]});
            var Q32;
            Q32=makeQuery(id+"FwjZak2WU2AujaI_0.opExtrude","SWEPT_BODY",BODY,{"disambiguationData":[OSD([sQuery(id+"F7.wireOp",EDGE,"E7.bottom"),sQuery(id+"F7.wireOp",EDGE,"E18.right"),sQuery(id+"F7.wireOp",EDGE,"E19.right"),sQuery(id+"F7.wireOp",EDGE,"E19.bottom")])]});
            var Q33;
            Q33=makeQuery(id+"F8.opExtrude","SWEPT_BODY",BODY,{"disambiguationData":[OSD([sQuery(id+"F7.wireOp",EDGE,"E8.right"),sQuery(id+"F7.wireOp",EDGE,"E9.right"),sQuery(id+"F7.wireOp",EDGE,"E9.bottom"),sQuery(id+"F7.wireOp",EDGE,"E86")])]});
            var Q34;
            Q34=makeQuery(id+"F8.opExtrude","SWEPT_BODY",BODY,{"disambiguationData":[OSD([sQuery(id+"F7.wireOp",EDGE,"E4.right"),sQuery(id+"F7.wireOp",EDGE,"E5.right"),sQuery(id+"F7.wireOp",EDGE,"E5.bottom"),sQuery(id+"F7.wireOp",EDGE,"E86")])]});
            var Q35;
            Q35=makeQuery(id+"F8.opExtrude","SWEPT_BODY",BODY,{"disambiguationData":[OSD([sQuery(id+"F7.wireOp",EDGE,"E10.right"),sQuery(id+"F7.wireOp",EDGE,"E63.bottom"),sQuery(id+"F7.wireOp",EDGE,"E85"),sQuery(id+"F7.wireOp",EDGE,"E86")])]});
            var Q36;
            Q36=makeQuery(id+"F8.opExtrude","SWEPT_BODY",BODY,{"disambiguationData":[OSD([sQuery(id+"F7.wireOp",EDGE,"E8.bottom"),sQuery(id+"F7.wireOp",EDGE,"E19.right"),sQuery(id+"F7.wireOp",EDGE,"E20.right"),sQuery(id+"F7.wireOp",EDGE,"E20.bottom")])]});
            var Q37;
            Q37=makeQuery(id+"F8.opExtrude","SWEPT_BODY",BODY,{"disambiguationData":[OSD([sQuery(id+"F7.wireOp",EDGE,"E10.bottom"),sQuery(id+"F7.wireOp",EDGE,"E21.right"),sQuery(id+"F7.wireOp",EDGE,"E59.bottom"),sQuery(id+"F7.wireOp",EDGE,"E63.right"),sQuery(id+"F7.wireOp",EDGE,"E85")])]});
            var Q38;
            Q38=makeQuery(id+"F8.opExtrude","SWEPT_BODY",BODY,{"disambiguationData":[OSD([sQuery(id+"F7.wireOp",EDGE,"E15.bottom"),sQuery(id+"F7.wireOp",EDGE,"E24.right"),sQuery(id+"F7.wireOp",EDGE,"E25.right"),sQuery(id+"F7.wireOp",EDGE,"E25.bottom")])]});
            var Q39;
            Q39=makeQuery(id+"F8.opExtrude","SWEPT_BODY",BODY,{"disambiguationData":[OSD([sQuery(id+"F7.wireOp",EDGE,"E17.bottom"),sQuery(id+"F7.wireOp",EDGE,"E26.right"),sQuery(id+"F7.wireOp",EDGE,"E27.right"),sQuery(id+"F7.wireOp",EDGE,"E35.top")])]});
            var Q40;
            Q40=makeQuery(id+"F8.opExtrude","SWEPT_BODY",BODY,{"disambiguationData":[OSD([sQuery(id+"F7.wireOp",EDGE,"E21.bottom"),sQuery(id+"F7.wireOp",EDGE,"E30.right"),sQuery(id+"F7.wireOp",EDGE,"E60.bottom"),sQuery(id+"F7.wireOp",EDGE,"E59.right"),sQuery(id+"F7.wireOp",EDGE,"E85")])]});
            var Q41;
            Q41=makeQuery(id+"F8.opExtrude","SWEPT_BODY",BODY,{"disambiguationData":[OSD([sQuery(id+"F7.wireOp",EDGE,"E19.bottom"),sQuery(id+"F7.wireOp",EDGE,"E28.right"),sQuery(id+"F7.wireOp",EDGE,"E29.right"),sQuery(id+"F7.wireOp",EDGE,"E29.bottom")])]});
            var Q42;
            Q42=makeQuery(id+"F8.opExtrude","SWEPT_BODY",BODY,{"disambiguationData":[OSD([sQuery(id+"F7.wireOp",EDGE,"E26.bottom"),sQuery(id+"F7.wireOp",EDGE,"E33.right"),sQuery(id+"F7.wireOp",EDGE,"E34.right"),sQuery(id+"F7.wireOp",EDGE,"E34.bottom")])]});
            var Q43;
            Q43=makeQuery(id+"F8.opExtrude","SWEPT_BODY",BODY,{"disambiguationData":[OSD([sQuery(id+"F7.wireOp",EDGE,"E35.bottom"),sQuery(id+"F7.wireOp",EDGE,"E40.right"),sQuery(id+"F7.wireOp",EDGE,"E41.right"),sQuery(id+"F7.wireOp",EDGE,"E41.bottom")])]});
            var Q44;
            Q44=makeQuery(id+"F8.opExtrude","SWEPT_BODY",BODY,{"disambiguationData":[OSD([sQuery(id+"F7.wireOp",EDGE,"E30.bottom"),sQuery(id+"F7.wireOp",EDGE,"E37.right"),sQuery(id+"F7.wireOp",EDGE,"E60.right"),sQuery(id+"F7.wireOp",EDGE,"E61.bottom")])]});
            var Q45;
            Q45=makeQuery(id+"F8.opExtrude","SWEPT_BODY",BODY,{"disambiguationData":[OSD([sQuery(id+"F7.wireOp",EDGE,"E37.bottom"),sQuery(id+"F7.wireOp",EDGE,"E42.right"),sQuery(id+"F7.wireOp",EDGE,"E52.bottom"),sQuery(id+"F7.wireOp",EDGE,"E61.right")])]});
            var Q46;
            Q46=makeQuery(id+"F8.opExtrude","SWEPT_BODY",BODY,{"disambiguationData":[OSD([sQuery(id+"F7.wireOp",EDGE,"E42.bottom"),sQuery(id+"F7.wireOp",EDGE,"E45.right"),sQuery(id+"F7.wireOp",EDGE,"E52.right"),sQuery(id+"F7.wireOp",EDGE,"E54.top")])]});
            var Q47;
            Q47=makeQuery(id+"F8.opExtrude","SWEPT_BODY",BODY,{"disambiguationData":[OSD([sQuery(id+"F7.wireOp",EDGE,"E48.top"),sQuery(id+"F7.wireOp",EDGE,"E32.right"),sQuery(id+"F7.wireOp",EDGE,"E48.bottom"),sQuery(id+"F7.wireOp",EDGE,"E84")])]});
            var Q48;
            Q48=makeQuery(id+"F8.opExtrude","SWEPT_BODY",BODY,{"disambiguationData":[OSD([sQuery(id+"F7.wireOp",EDGE,"E47.top"),sQuery(id+"F7.wireOp",EDGE,"E23.right"),sQuery(id+"F7.wireOp",EDGE,"E84")])]});
            var Q49;
            Q49=makeQuery(id+"F8.opExtrude","SWEPT_BODY",BODY,{"disambiguationData":[OSD([sQuery(id+"F7.wireOp",EDGE,"E49.top"),sQuery(id+"F7.wireOp",EDGE,"E39.right"),sQuery(id+"F7.wireOp",EDGE,"E49.right"),sQuery(id+"F7.wireOp",EDGE,"E49.bottom"),sQuery(id+"F7.wireOp",EDGE,"E84")])]});
            var Q50;
            Q50=makeQuery(id+"F8.opExtrude","SWEPT_BODY",BODY,{"disambiguationData":[OSD([sQuery(id+"F7.wireOp",EDGE,"E40.bottom"),sQuery(id+"F7.wireOp",EDGE,"E50.right"),sQuery(id+"F7.wireOp",EDGE,"E50.top"),sQuery(id+"F7.wireOp",EDGE,"E65.left"),sQuery(id+"F7.wireOp",EDGE,"E84")])]});
            var Q51;
            Q51=makeQuery(id+"F8.opExtrude","SWEPT_BODY",BODY,{"disambiguationData":[OSD([sQuery(id+"F7.wireOp",EDGE,"E58.bottom"),sQuery(id+"F7.wireOp",EDGE,"E57.left"),sQuery(id+"F7.wireOp",EDGE,"E58.left"),sQuery(id+"F7.wireOp",EDGE,"E58.top"),sQuery(id+"F7.wireOp",EDGE,"E85")])]});
            var Q52;
            Q52=makeQuery(id+"F8.opExtrude","SWEPT_BODY",BODY,{"disambiguationData":[OSD([sQuery(id+"F7.wireOp",EDGE,"E45.bottom"),sQuery(id+"F7.wireOp",EDGE,"E53.left"),sQuery(id+"F7.wireOp",EDGE,"E53.right"),sQuery(id+"F7.wireOp",EDGE,"E57.bottom")])]});
            var Q53;
            Q53=makeQuery(id+"F8.opExtrude","SWEPT_BODY",BODY,{"disambiguationData":[OSD([sQuery(id+"F7.wireOp",EDGE,"E60.top"),sQuery(id+"F7.wireOp",EDGE,"E61.left"),sQuery(id+"F7.wireOp",EDGE,"E85")])]});
            var Q54;
            Q54=makeQuery(id+"F8.opExtrude","SWEPT_BODY",BODY,{"disambiguationData":[OSD([sQuery(id+"F7.wireOp",EDGE,"E55.top"),sQuery(id+"F7.wireOp",EDGE,"E54.right"),sQuery(id+"F7.wireOp",EDGE,"E67.bottom"),sQuery(id+"F7.wireOp",EDGE,"E85")])]});
            var Q55;
            Q55=makeQuery(id+"F8.opExtrude","SWEPT_BODY",BODY,{"disambiguationData":[OSD([sQuery(id+"F7.wireOp",EDGE,"E61.top"),sQuery(id+"F7.wireOp",EDGE,"E62.right"),sQuery(id+"F7.wireOp",EDGE,"E85")])]});
            var Q56;
            Q56=makeQuery(id+"FwjZak2WU2AujaI_0.opExtrude","SWEPT_BODY",BODY,{"disambiguationData":[OSD([sQuery(id+"F7.wireOp",EDGE,"E58.top"),sQuery(id+"F7.wireOp",EDGE,"E69.right"),sQuery(id+"F7.wireOp",EDGE,"E85")])]});
            var Q57;
            Q57=makeQuery(id+"FwjZak2WU2AujaI_0.opExtrude","SWEPT_BODY",BODY,{"disambiguationData":[OSD([sQuery(id+"F7.wireOp",EDGE,"E5.bottom"),sQuery(id+"F7.wireOp",EDGE,"E16.right"),sQuery(id+"F7.wireOp",EDGE,"E17.right"),sQuery(id+"F7.wireOp",EDGE,"E17.bottom")])]});
            var Q58;
            Q58=makeQuery(id+"F8.opExtrude","SWEPT_BODY",BODY,{"disambiguationData":[OSD([sQuery(id+"F7.wireOp",EDGE,"E2.bottom"),sQuery(id+"F7.wireOp",EDGE,"E13.right"),sQuery(id+"F7.wireOp",EDGE,"E14.right"),sQuery(id+"F7.wireOp",EDGE,"E14.bottom")])]});
            var Q59;
            Q59=makeQuery(id+"F8.opExtrude","SWEPT_BODY",BODY,{"disambiguationData":[OSD([sQuery(id+"F7.wireOp",EDGE,"E4.bottom"),sQuery(id+"F7.wireOp",EDGE,"E15.right"),sQuery(id+"F7.wireOp",EDGE,"E16.right"),sQuery(id+"F7.wireOp",EDGE,"E16.bottom")])]});
            var Q60;
            Q60=makeQuery(id+"F8.opExtrude","SWEPT_BODY",BODY,{"disambiguationData":[OSD([sQuery(id+"F7.wireOp",EDGE,"E6.bottom"),sQuery(id+"F7.wireOp",EDGE,"E17.right"),sQuery(id+"F7.wireOp",EDGE,"E18.right"),sQuery(id+"F7.wireOp",EDGE,"E28.top")])]});
            var Q61;
            Q61=makeQuery(id+"F8.opExtrude","SWEPT_BODY",BODY,{"disambiguationData":[OSD([sQuery(id+"F7.wireOp",EDGE,"E28.bottom"),sQuery(id+"F7.wireOp",EDGE,"E35.right"),sQuery(id+"F7.wireOp",EDGE,"E36.right"),sQuery(id+"F7.wireOp",EDGE,"E36.bottom")])]});
            var Q62;
            Q62=makeQuery(id+"F8.opExtrude","SWEPT_BODY",BODY,{"disambiguationData":[OSD([sQuery(id+"F7.wireOp",EDGE,"E0.top"),sQuery(id+"F7.wireOp",EDGE,"E12.right"),sQuery(id+"F7.wireOp",EDGE,"E84")])]});
            var Q63;
            Q63=makeQuery(id+"F8.opExtrude","SWEPT_BODY",BODY,{"disambiguationData":[OSD([sQuery(id+"F7.wireOp",EDGE,"E69.bottom"),sQuery(id+"F7.wireOp",EDGE,"E69.right"),sQuery(id+"F7.wireOp",EDGE,"E84")])]});
            var Q64;
            Q64=sQuery(id+"F7.wireOp",EDGE,"E86");
            transform(context, id + "F9", {"entities" : qUnion([Q0, Q1, Q2, Q3, Q4, Q5, Q6, Q7, Q8, Q9, Q10, Q11, Q12, Q13, Q14, Q15, Q16, Q17, Q18, Q19, Q20, Q21, Q22, Q23, Q24, Q25, Q26, Q27, Q28, Q29, Q30, Q31, Q32, Q33, Q34, Q35, Q36, Q37, Q38, Q39, Q40, Q41, Q42, Q43, Q44, Q45, Q46, Q47, Q48, Q49, Q50, Q51, Q52, Q53, Q54, Q55, Q56, Q57, Q58, Q59, Q60, Q61, Q62, Q63]), "transformType" : TransformType.ROTATION, "transformAxis" : qUnion([Q64]), "angle" : 45 * degree, "oppositeDirection" : true, "makeCopy" : false});
        }
        {
            var Q0;
            Q0=qCreatedBy(makeId("Right.planeOp"),FACE);
            var sketch = newSketch(context, id + "F10", { "sketchPlane" : qUnion([Q0])});
            skLineSegment(sketch, "E87.bottom", {"start": v(12, -0.05) * mm, "end": v(11, -0.05) * mm});
            skLineSegment(sketch, "E87.top", {"start": v(11.3, 0.95) * mm, "end": v(11, 0.95) * mm});
            skLineSegment(sketch, "E87.right", {"start": v(11, -0.05) * mm, "end": v(11, 0.95) * mm});
            skLineSegment(sketch, "E88.bottom", {"start": v(11, 0.95) * mm, "end": v(10, 0.95) * mm});
            skLineSegment(sketch, "E88.top", {"start": v(11, -0.05) * mm, "end": v(10, -0.05) * mm});
            skLineSegment(sketch, "E88.left", {"start": v(11, 0.95) * mm, "end": v(11, -0.05) * mm});
            skLineSegment(sketch, "E88.right", {"start": v(10, 0.95) * mm, "end": v(10, -0.05) * mm});
            skLineSegment(sketch, "E89.bottom", {"start": v(10, 0.95) * mm, "end": v(9, 0.95) * mm});
            skLineSegment(sketch, "E89.top", {"start": v(10, -0.05) * mm, "end": v(9, -0.05) * mm});
            skLineSegment(sketch, "E89.right", {"start": v(9, 0.95) * mm, "end": v(9, -0.05) * mm});
            skLineSegment(sketch, "E90.bottom", {"start": v(9, 0.95) * mm, "end": v(8, 0.95) * mm});
            skLineSegment(sketch, "E90.top", {"start": v(9, -0.05) * mm, "end": v(8, -0.05) * mm});
            skLineSegment(sketch, "E90.right", {"start": v(8, 0.95) * mm, "end": v(8, -0.05) * mm});
            skLineSegment(sketch, "E91.bottom", {"start": v(8, 0.95) * mm, "end": v(7, 0.95) * mm});
            skLineSegment(sketch, "E91.top", {"start": v(8, -0.05) * mm, "end": v(7, -0.05) * mm});
            skLineSegment(sketch, "E91.right", {"start": v(7, 0.95) * mm, "end": v(7, -0.05) * mm});
            skLineSegment(sketch, "E92.bottom", {"start": v(7, 0.95) * mm, "end": v(6, 0.95) * mm});
            skLineSegment(sketch, "E92.top", {"start": v(7, -0.05) * mm, "end": v(6, -0.05) * mm});
            skLineSegment(sketch, "E92.right", {"start": v(6, 0.95) * mm, "end": v(6, -0.05) * mm});
            skLineSegment(sketch, "E93.bottom", {"start": v(6, 0.95) * mm, "end": v(5, 0.95) * mm});
            skLineSegment(sketch, "E93.top", {"start": v(6, -0.05) * mm, "end": v(5, -0.05) * mm});
            skLineSegment(sketch, "E93.right", {"start": v(5, 0.95) * mm, "end": v(5, -0.05) * mm});
            skLineSegment(sketch, "E94.bottom", {"start": v(5, 0.95) * mm, "end": v(4, 0.95) * mm});
            skLineSegment(sketch, "E94.top", {"start": v(5, -0.05) * mm, "end": v(4, -0.05) * mm});
            skLineSegment(sketch, "E94.right", {"start": v(4, 0.95) * mm, "end": v(4, -0.05) * mm});
            skLineSegment(sketch, "E95.bottom", {"start": v(4, 0.95) * mm, "end": v(3, 0.95) * mm});
            skLineSegment(sketch, "E95.top", {"start": v(4, -0.05) * mm, "end": v(3, -0.05) * mm});
            skLineSegment(sketch, "E95.right", {"start": v(3, 0.95) * mm, "end": v(3, -0.05) * mm});
            skLineSegment(sketch, "E96.bottom", {"start": v(3, 0.95) * mm, "end": v(2, 0.95) * mm});
            skLineSegment(sketch, "E96.top", {"start": v(3, -0.05) * mm, "end": v(2, -0.05) * mm});
            skLineSegment(sketch, "E96.right", {"start": v(2, 0.95) * mm, "end": v(2, -0.05) * mm});
            skLineSegment(sketch, "E97.bottom", {"start": v(2, 0.95) * mm, "end": v(1, 0.95) * mm});
            skLineSegment(sketch, "E97.top", {"start": v(2, -0.05) * mm, "end": v(1, -0.05) * mm});
            skLineSegment(sketch, "E97.right", {"start": v(1, 0.95) * mm, "end": v(1, -0.05) * mm});
            skLineSegment(sketch, "E98.bottom", {"start": v(1, 0.95) * mm, "end": v(0.7, 0.95) * mm});
            skLineSegment(sketch, "E98.top", {"start": v(1, -0.05) * mm, "end": v(0, -0.05) * mm});
            skLineSegment(sketch, "E99.right", {"start": v(11, 0.95) * mm, "end": v(11, 1.36) * mm});
            skLineSegment(sketch, "E100.bottom", {"start": v(10.59, 1.95) * mm, "end": v(10, 1.95) * mm});
            skLineSegment(sketch, "E100.left", {"start": v(11, 1.36) * mm, "end": v(11, 0.95) * mm});
            skLineSegment(sketch, "E100.right", {"start": v(10, 1.95) * mm, "end": v(10, 0.95) * mm});
            skLineSegment(sketch, "E101.bottom", {"start": v(10, 1.95) * mm, "end": v(9, 1.95) * mm});
            skLineSegment(sketch, "E101.right", {"start": v(9, 1.95) * mm, "end": v(9, 0.95) * mm});
            skLineSegment(sketch, "E102.bottom", {"start": v(9, 1.95) * mm, "end": v(8, 1.95) * mm});
            skLineSegment(sketch, "E102.right", {"start": v(8, 1.95) * mm, "end": v(8, 0.95) * mm});
            skLineSegment(sketch, "E103.bottom", {"start": v(8, 1.95) * mm, "end": v(7, 1.95) * mm});
            skLineSegment(sketch, "E103.right", {"start": v(7, 1.95) * mm, "end": v(7, 0.95) * mm});
            skLineSegment(sketch, "E104.bottom", {"start": v(7, 1.95) * mm, "end": v(6, 1.95) * mm});
            skLineSegment(sketch, "E104.right", {"start": v(6, 1.95) * mm, "end": v(6, 0.95) * mm});
            skLineSegment(sketch, "E105.bottom", {"start": v(6, 1.95) * mm, "end": v(5, 1.95) * mm});
            skLineSegment(sketch, "E105.right", {"start": v(5, 1.95) * mm, "end": v(5, 0.95) * mm});
            skLineSegment(sketch, "E106.bottom", {"start": v(5, 1.95) * mm, "end": v(4, 1.95) * mm});
            skLineSegment(sketch, "E106.right", {"start": v(4, 1.95) * mm, "end": v(4, 0.95) * mm});
            skLineSegment(sketch, "E107.bottom", {"start": v(4, 1.95) * mm, "end": v(3, 1.95) * mm});
            skLineSegment(sketch, "E107.right", {"start": v(3, 1.95) * mm, "end": v(3, 0.95) * mm});
            skLineSegment(sketch, "E108.bottom", {"start": v(3, 1.95) * mm, "end": v(2, 1.95) * mm});
            skLineSegment(sketch, "E108.right", {"start": v(2, 1.95) * mm, "end": v(2, 0.95) * mm});
            skLineSegment(sketch, "E109.bottom", {"start": v(2, 1.95) * mm, "end": v(1.41, 1.95) * mm});
            skLineSegment(sketch, "E109.right", {"start": v(1, 1.36) * mm, "end": v(1, 0.95) * mm});
            skLineSegment(sketch, "E110.right", {"start": v(10, 2.78) * mm, "end": v(10, 1.95) * mm});
            skLineSegment(sketch, "E111.bottom", {"start": v(9.88, 2.95) * mm, "end": v(9, 2.95) * mm});
            skLineSegment(sketch, "E111.right", {"start": v(9, 2.95) * mm, "end": v(9, 1.95) * mm});
            skLineSegment(sketch, "E112.bottom", {"start": v(9, 2.95) * mm, "end": v(8, 2.95) * mm});
            skLineSegment(sketch, "E112.right", {"start": v(8, 2.95) * mm, "end": v(8, 1.95) * mm});
            skLineSegment(sketch, "E113.bottom", {"start": v(8, 2.95) * mm, "end": v(7, 2.95) * mm});
            skLineSegment(sketch, "E113.right", {"start": v(7, 2.95) * mm, "end": v(7, 1.95) * mm});
            skLineSegment(sketch, "E114.bottom", {"start": v(7, 2.95) * mm, "end": v(6, 2.95) * mm});
            skLineSegment(sketch, "E114.right", {"start": v(6, 2.95) * mm, "end": v(6, 1.95) * mm});
            skLineSegment(sketch, "E115.bottom", {"start": v(6, 2.95) * mm, "end": v(5, 2.95) * mm});
            skLineSegment(sketch, "E115.right", {"start": v(5, 2.95) * mm, "end": v(5, 1.95) * mm});
            skLineSegment(sketch, "E116.bottom", {"start": v(5, 2.95) * mm, "end": v(4, 2.95) * mm});
            skLineSegment(sketch, "E116.right", {"start": v(4, 2.95) * mm, "end": v(4, 1.95) * mm});
            skLineSegment(sketch, "E117.bottom", {"start": v(4, 2.95) * mm, "end": v(3, 2.95) * mm});
            skLineSegment(sketch, "E117.right", {"start": v(3, 2.95) * mm, "end": v(3, 1.95) * mm});
            skLineSegment(sketch, "E118.bottom", {"start": v(3, 2.95) * mm, "end": v(2.12, 2.95) * mm});
            skLineSegment(sketch, "E118.right", {"start": v(2, 2.78) * mm, "end": v(2, 1.95) * mm});
            skLineSegment(sketch, "E119.right", {"start": v(9, 3.95) * mm, "end": v(9, 2.95) * mm});
            skLineSegment(sketch, "E120.bottom", {"start": v(9, 3.95) * mm, "end": v(8, 3.95) * mm});
            skLineSegment(sketch, "E120.right", {"start": v(8, 3.95) * mm, "end": v(8, 2.95) * mm});
            skLineSegment(sketch, "E121.bottom", {"start": v(8, 3.95) * mm, "end": v(7, 3.95) * mm});
            skLineSegment(sketch, "E121.right", {"start": v(7, 3.95) * mm, "end": v(7, 2.95) * mm});
            skLineSegment(sketch, "E122.bottom", {"start": v(7, 3.95) * mm, "end": v(6, 3.95) * mm});
            skLineSegment(sketch, "E122.right", {"start": v(6, 3.95) * mm, "end": v(6, 2.95) * mm});
            skLineSegment(sketch, "E123.bottom", {"start": v(6, 3.95) * mm, "end": v(5, 3.95) * mm});
            skLineSegment(sketch, "E123.right", {"start": v(5, 3.95) * mm, "end": v(5, 2.95) * mm});
            skLineSegment(sketch, "E124.bottom", {"start": v(5, 3.95) * mm, "end": v(4, 3.95) * mm});
            skLineSegment(sketch, "E124.right", {"start": v(4, 3.95) * mm, "end": v(4, 2.95) * mm});
            skLineSegment(sketch, "E125.bottom", {"start": v(4, 3.95) * mm, "end": v(3, 3.95) * mm});
            skLineSegment(sketch, "E125.right", {"start": v(3, 3.95) * mm, "end": v(3, 2.95) * mm});
            skLineSegment(sketch, "E126.right", {"start": v(8, 4.95) * mm, "end": v(8, 3.95) * mm});
            skLineSegment(sketch, "E127.bottom", {"start": v(8, 4.95) * mm, "end": v(7, 4.95) * mm});
            skLineSegment(sketch, "E127.right", {"start": v(7, 4.95) * mm, "end": v(7, 3.95) * mm});
            skLineSegment(sketch, "E128.bottom", {"start": v(7, 4.95) * mm, "end": v(6, 4.95) * mm});
            skLineSegment(sketch, "E128.right", {"start": v(6, 4.95) * mm, "end": v(6, 3.95) * mm});
            skLineSegment(sketch, "E129.bottom", {"start": v(6, 4.95) * mm, "end": v(5, 4.95) * mm});
            skLineSegment(sketch, "E129.right", {"start": v(5, 4.95) * mm, "end": v(5, 3.95) * mm});
            skLineSegment(sketch, "E130.bottom", {"start": v(5, 4.95) * mm, "end": v(4, 4.95) * mm});
            skLineSegment(sketch, "E130.right", {"start": v(4, 4.95) * mm, "end": v(4, 3.95) * mm});
            skLineSegment(sketch, "E131.right", {"start": v(7, 5.95) * mm, "end": v(7, 4.95) * mm});
            skLineSegment(sketch, "E132.bottom", {"start": v(7, 5.95) * mm, "end": v(6, 5.95) * mm});
            skLineSegment(sketch, "E132.right", {"start": v(6, 5.95) * mm, "end": v(6, 4.95) * mm});
            skLineSegment(sketch, "E133.bottom", {"start": v(6, 5.95) * mm, "end": v(5, 5.95) * mm});
            skLineSegment(sketch, "E133.right", {"start": v(5, 5.95) * mm, "end": v(5, 4.95) * mm});
            skLineSegment(sketch, "E134.top", {"start": v(10, 1.95) * mm, "end": v(10.59, 1.95) * mm});
            skLineSegment(sketch, "E135.bottom", {"start": v(9, 3.95) * mm, "end": v(9.17, 3.95) * mm});
            skLineSegment(sketch, "E135.top", {"start": v(9, 2.95) * mm, "end": v(9.88, 2.95) * mm});
            skLineSegment(sketch, "E136.bottom", {"start": v(8, 4.95) * mm, "end": v(8.46, 4.95) * mm});
            skLineSegment(sketch, "E136.top", {"start": v(8, 3.95) * mm, "end": v(9, 3.95) * mm});
            skLineSegment(sketch, "E136.right", {"start": v(9, 4.2) * mm, "end": v(9, 3.95) * mm});
            skLineSegment(sketch, "E137.top", {"start": v(7.76, 5.95) * mm, "end": v(7, 5.95) * mm});
            skLineSegment(sketch, "E137.left", {"start": v(8, 4.95) * mm, "end": v(8, 5.6) * mm});
            skLineSegment(sketch, "E137.right", {"start": v(7, 4.95) * mm, "end": v(7, 5.95) * mm});
            skLineSegment(sketch, "E138.right", {"start": v(7, 5.95) * mm, "end": v(7, 6.95) * mm});
            skLineSegment(sketch, "E139.bottom", {"start": v(4, 4.95) * mm, "end": v(5, 4.95) * mm});
            skLineSegment(sketch, "E139.top", {"start": v(4.24, 5.95) * mm, "end": v(5, 5.95) * mm});
            skLineSegment(sketch, "E139.right", {"start": v(5, 4.95) * mm, "end": v(5, 5.95) * mm});
            skLineSegment(sketch, "E140.bottom", {"start": v(7, 6.95) * mm, "end": v(6, 6.95) * mm});
            skLineSegment(sketch, "E140.left", {"start": v(7, 6.95) * mm, "end": v(7, 5.95) * mm});
            skLineSegment(sketch, "E140.right", {"start": v(6, 6.95) * mm, "end": v(6, 5.95) * mm});
            skLineSegment(sketch, "E141.bottom", {"start": v(6, 6.95) * mm, "end": v(5, 6.95) * mm});
            skLineSegment(sketch, "E141.right", {"start": v(5, 6.95) * mm, "end": v(5, 5.95) * mm});
            skLineSegment(sketch, "E142.top", {"start": v(5, 5.95) * mm, "end": v(4.24, 5.95) * mm});
            skLineSegment(sketch, "E143.right", {"start": v(7, 6.95) * mm, "end": v(7, 7.02) * mm});
            skLineSegment(sketch, "E144.bottom", {"start": v(6, 6.95) * mm, "end": v(7, 6.95) * mm});
            skLineSegment(sketch, "E144.top", {"start": v(6, 8) * mm, "end": v(6.3, 8) * mm});
            skLineSegment(sketch, "E144.left", {"start": v(6, 6.95) * mm, "end": v(6, 8) * mm});
            skLineSegment(sketch, "E145.bottom", {"start": v(5, 6.95) * mm, "end": v(6, 6.95) * mm});
            skLineSegment(sketch, "E145.top", {"start": v(5.7, 8) * mm, "end": v(6, 8) * mm});
            skLineSegment(sketch, "E145.left", {"start": v(5, 6.95) * mm, "end": v(5, 7.02) * mm});
            skLineSegment(sketch, "E146.bottom", {"start": v(1.41, 1.95) * mm, "end": v(2, 1.95) * mm});
            skLineSegment(sketch, "E146.right", {"start": v(2, 1.95) * mm, "end": v(2, 2.78) * mm});
            skLineSegment(sketch, "E147.bottom", {"start": v(2.12, 2.95) * mm, "end": v(3, 2.95) * mm});
            skLineSegment(sketch, "E147.top", {"start": v(2.83, 3.95) * mm, "end": v(3, 3.95) * mm});
            skLineSegment(sketch, "E147.right", {"start": v(3, 2.95) * mm, "end": v(3, 3.95) * mm});
            skLineSegment(sketch, "E148.bottom", {"start": v(3, 3.95) * mm, "end": v(4, 3.95) * mm});
            skLineSegment(sketch, "E148.top", {"start": v(3.54, 4.95) * mm, "end": v(4, 4.95) * mm});
            skLineSegment(sketch, "E148.left", {"start": v(3, 3.95) * mm, "end": v(3, 4.2) * mm});
            skLineSegment(sketch, "E148.right", {"start": v(4, 3.95) * mm, "end": v(4, 4.95) * mm});
            skLineSegment(sketch, "E149.right", {"start": v(4, 4.95) * mm, "end": v(4, 5.6) * mm});
            skLineSegment(sketch, "E150.bottom", {"start": v(0.7, 0.95) * mm, "end": v(1, 0.95) * mm});
            skLineSegment(sketch, "E150.right", {"start": v(1, 0.95) * mm, "end": v(1, 1.36) * mm});
            skLineSegment(sketch, "E151.bottom", {"start": v(9.17, 3.95) * mm, "end": v(9, 3.95) * mm});
            skLineSegment(sketch, "E151.right", {"start": v(9, 3.95) * mm, "end": v(9, 4.2) * mm});
            skLineSegment(sketch, "E152.left", {"start": v(8, 5.6) * mm, "end": v(8, 4.95) * mm});
            skLineSegment(sketch, "E153.bottom", {"start": v(5, 6.95) * mm, "end": v(4.95, 6.95) * mm});
            skLineSegment(sketch, "E154.bottom", {"start": v(4.95, 6.95) * mm, "end": v(5, 6.95) * mm});
            skLineSegment(sketch, "E155.bottom", {"start": v(7.05, 6.95) * mm, "end": v(7, 6.95) * mm});
            skLineSegment(sketch, "E156.bottom", {"start": v(6.3, 8) * mm, "end": v(6, 8) * mm});
            skLineSegment(sketch, "E156.right", {"start": v(6, 8) * mm, "end": v(6, 8.43) * mm});
            skLineSegment(sketch, "E157", {"start": v(0, -0.05) * mm, "end": v(6, 8.43) * mm});
            skLineSegment(sketch, "E158", {"start": v(6, 8.43) * mm, "end": v(12, -0.05) * mm});
            skLineSegment(sketch, "E159", {"start": v(0, 0) * mm, "end": v(12, -0.05) * mm});
            skSolve(sketch);
        }
        {
            var Q0;
            {var subQ0=sQuery(id+"F10.wireOp",EDGE,"E98.top");Q0=makeQuery(id+"F10.imprint","IMPRINT",FACE,{"disambiguationData":[TD([[makeQuery(id+"F10.imprint","IMPRINT",EDGE,{"derivedFrom":subQ0}),-1.0]])]});}
            var Q1;
            Q1=makeQuery(id+"F10.imprint","IMPRINT",FACE,{"disambiguationData":[TD([[makeQuery(id+"F10.imprint","IMPRINT",EDGE,{"derivedFrom":sQuery(id+"F10.wireOp",EDGE,"E97.bottom")}),-1.0]])]});
            var Q2;
            Q2=makeQuery(id+"F10.imprint","IMPRINT",FACE,{"disambiguationData":[TD([[makeQuery(id+"F10.imprint","IMPRINT",EDGE,{"derivedFrom":sQuery(id+"F10.wireOp",EDGE,"E108.bottom")}),-1.0]])]});
            var Q3;
            Q3=makeQuery(id+"F10.imprint","IMPRINT",FACE,{"disambiguationData":[TD([[makeQuery(id+"F10.imprint","IMPRINT",EDGE,{"derivedFrom":sQuery(id+"F10.wireOp",EDGE,"E96.top")}),-1.0]])]});
            var Q4;
            Q4=makeQuery(id+"F10.imprint","IMPRINT",FACE,{"disambiguationData":[TD([[makeQuery(id+"F10.imprint","IMPRINT",EDGE,{"derivedFrom":sQuery(id+"F10.wireOp",EDGE,"E95.bottom")}),-1.0]])]});
            var Q5;
            Q5=makeQuery(id+"F10.imprint","IMPRINT",FACE,{"disambiguationData":[TD([[makeQuery(id+"F10.imprint","IMPRINT",EDGE,{"derivedFrom":sQuery(id+"F10.wireOp",EDGE,"E106.bottom")}),-1.0]])]});
            var Q6;
            Q6=makeQuery(id+"F10.imprint","IMPRINT",FACE,{"disambiguationData":[TD([[makeQuery(id+"F10.imprint","IMPRINT",EDGE,{"derivedFrom":sQuery(id+"F10.wireOp",EDGE,"E117.bottom")}),-1.0]])]});
            var Q7;
            Q7=makeQuery(id+"F10.imprint","IMPRINT",FACE,{"disambiguationData":[TD([[makeQuery(id+"F10.imprint","IMPRINT",EDGE,{"derivedFrom":sQuery(id+"F10.wireOp",EDGE,"E124.bottom")}),-1.0]])]});
            var Q8;
            Q8=makeQuery(id+"F10.imprint","IMPRINT",FACE,{"disambiguationData":[TD([[makeQuery(id+"F10.imprint","IMPRINT",EDGE,{"derivedFrom":sQuery(id+"F10.wireOp",EDGE,"E115.bottom")}),-1.0]])]});
            var Q9;
            Q9=makeQuery(id+"F10.imprint","IMPRINT",FACE,{"disambiguationData":[TD([[makeQuery(id+"F10.imprint","IMPRINT",EDGE,{"derivedFrom":sQuery(id+"F10.wireOp",EDGE,"E93.bottom")}),-1.0]])]});
            var Q10;
            Q10=makeQuery(id+"F10.imprint","IMPRINT",FACE,{"disambiguationData":[TD([[makeQuery(id+"F10.imprint","IMPRINT",EDGE,{"derivedFrom":sQuery(id+"F10.wireOp",EDGE,"E94.top")}),-1.0]])]});
            var Q11;
            Q11=makeQuery(id+"F10.imprint","IMPRINT",FACE,{"disambiguationData":[TD([[makeQuery(id+"F10.imprint","IMPRINT",EDGE,{"derivedFrom":sQuery(id+"F10.wireOp",EDGE,"E104.bottom")}),-1.0]])]});
            var Q12;
            Q12=makeQuery(id+"F10.imprint","IMPRINT",FACE,{"disambiguationData":[TD([[makeQuery(id+"F10.imprint","IMPRINT",EDGE,{"derivedFrom":sQuery(id+"F10.wireOp",EDGE,"E91.bottom")}),-1.0]])]});
            var Q13;
            Q13=makeQuery(id+"F10.imprint","IMPRINT",FACE,{"disambiguationData":[TD([[makeQuery(id+"F10.imprint","IMPRINT",EDGE,{"derivedFrom":sQuery(id+"F10.wireOp",EDGE,"E92.top")}),-1.0]])]});
            var Q14;
            Q14=makeQuery(id+"F10.imprint","IMPRINT",FACE,{"disambiguationData":[TD([[makeQuery(id+"F10.imprint","IMPRINT",EDGE,{"derivedFrom":sQuery(id+"F10.wireOp",EDGE,"E102.bottom")}),-1.0]])]});
            var Q15;
            Q15=makeQuery(id+"F10.imprint","IMPRINT",FACE,{"disambiguationData":[TD([[makeQuery(id+"F10.imprint","IMPRINT",EDGE,{"derivedFrom":sQuery(id+"F10.wireOp",EDGE,"E89.bottom")}),-1.0]])]});
            var Q16;
            Q16=makeQuery(id+"F10.imprint","IMPRINT",FACE,{"disambiguationData":[TD([[makeQuery(id+"F10.imprint","IMPRINT",EDGE,{"derivedFrom":sQuery(id+"F10.wireOp",EDGE,"E90.top")}),-1.0]])]});
            var Q17;
            Q17=makeQuery(id+"F10.imprint","IMPRINT",FACE,{"disambiguationData":[TD([[makeQuery(id+"F10.imprint","IMPRINT",EDGE,{"derivedFrom":sQuery(id+"F10.wireOp",EDGE,"E88.top")}),-1.0]])]});
            var Q18;
            {var subQ0=sQuery(id+"F10.wireOp",EDGE,"E87.top");Q18=makeQuery(id+"F10.imprint","IMPRINT",FACE,{"disambiguationData":[TD([[makeQuery(id+"F10.imprint","IMPRINT",EDGE,{"derivedFrom":subQ0}),-1.0]])]});}
            var Q19;
            {var subQ0=sQuery(id+"F10.wireOp",EDGE,"E134.top");Q19=makeQuery(id+"F10.imprint","IMPRINT",FACE,{"disambiguationData":[TD([[makeQuery(id+"F10.imprint","IMPRINT",EDGE,{"derivedFrom":subQ0}),1.0]])]});}
            var Q20;
            {var subQ0=sQuery(id+"F10.wireOp",EDGE,"E135.top");Q20=makeQuery(id+"F10.imprint","IMPRINT",FACE,{"disambiguationData":[TD([[makeQuery(id+"F10.imprint","IMPRINT",EDGE,{"derivedFrom":subQ0}),1.0]])]});}
            var Q21;
            Q21=makeQuery(id+"F10.imprint","IMPRINT",FACE,{"disambiguationData":[TD([[makeQuery(id+"F10.imprint","IMPRINT",EDGE,{"derivedFrom":sQuery(id+"F10.wireOp",EDGE,"E136.top")}),1.0]])]});
            var Q22;
            Q22=makeQuery(id+"F10.imprint","IMPRINT",FACE,{"disambiguationData":[TD([[makeQuery(id+"F10.imprint","IMPRINT",EDGE,{"derivedFrom":sQuery(id+"F10.wireOp",EDGE,"E113.bottom")}),-1.0]])]});
            var Q23;
            Q23=makeQuery(id+"F10.imprint","IMPRINT",FACE,{"disambiguationData":[TD([[makeQuery(id+"F10.imprint","IMPRINT",EDGE,{"derivedFrom":sQuery(id+"F10.wireOp",EDGE,"E122.bottom")}),-1.0]])]});
            var Q24;
            Q24=makeQuery(id+"F10.imprint","IMPRINT",FACE,{"disambiguationData":[TD([[makeQuery(id+"F10.imprint","IMPRINT",EDGE,{"derivedFrom":sQuery(id+"F10.wireOp",EDGE,"E127.bottom")}),-1.0]])]});
            var Q25;
            Q25=makeQuery(id+"F10.imprint","IMPRINT",FACE,{"disambiguationData":[TD([[makeQuery(id+"F10.imprint","IMPRINT",EDGE,{"derivedFrom":sQuery(id+"F10.wireOp",EDGE,"E129.bottom")}),-1.0]])]});
            var Q26;
            {var subQ0=sQuery(id+"F10.wireOp",EDGE,"E142.top");Q26=makeQuery(id+"F10.imprint","IMPRINT",FACE,{"disambiguationData":[TD([[makeQuery(id+"F10.imprint","IMPRINT",EDGE,{"derivedFrom":subQ0}),-1.0]])]});}
            var Q27;
            {var subQ0=sQuery(id+"F10.wireOp",EDGE,"E148.top");Q27=makeQuery(id+"F10.imprint","IMPRINT",FACE,{"disambiguationData":[TD([[makeQuery(id+"F10.imprint","IMPRINT",EDGE,{"derivedFrom":subQ0}),1.0]])]});}
            var Q28;
            {var subQ0=sQuery(id+"F10.wireOp",EDGE,"E147.top");Q28=makeQuery(id+"F10.imprint","IMPRINT",FACE,{"disambiguationData":[TD([[makeQuery(id+"F10.imprint","IMPRINT",EDGE,{"derivedFrom":subQ0}),1.0]])]});}
            var Q29;
            Q29=makeQuery(id+"F10.imprint","IMPRINT",FACE,{"disambiguationData":[TD([[makeQuery(id+"F10.imprint","IMPRINT",EDGE,{"derivedFrom":sQuery(id+"F10.wireOp",EDGE,"E145.bottom")}),1.0]])]});
            var Q30;
            Q30=makeQuery(id+"F10.imprint","IMPRINT",FACE,{"disambiguationData":[TD([[makeQuery(id+"F10.imprint","IMPRINT",EDGE,{"derivedFrom":sQuery(id+"F10.wireOp",EDGE,"E132.bottom")}),-1.0]])]});
            var Q31;
            {var subQ0=sQuery(id+"F10.wireOp",EDGE,"E156.bottom");Q31=makeQuery(id+"F10.imprint","IMPRINT",FACE,{"disambiguationData":[TD([[makeQuery(id+"F10.imprint","IMPRINT",EDGE,{"derivedFrom":subQ0}),-1.0]])]});}
            var Q32;
            {var subQ0=sQuery(id+"F10.wireOp",EDGE,"E150.bottom");Q32=makeQuery(id+"F10.imprint","IMPRINT",FACE,{"disambiguationData":[TD([[makeQuery(id+"F10.imprint","IMPRINT",EDGE,{"derivedFrom":subQ0}),-1.0]])]});}
            var Q33;
            {var subQ0=sQuery(id+"F10.wireOp",EDGE,"E96.bottom");Q33=makeQuery(id+"F10.imprint","IMPRINT",FACE,{"disambiguationData":[TD([[makeQuery(id+"F10.imprint","IMPRINT",EDGE,{"derivedFrom":subQ0}),1.0]])]});}
            var Q34;
            {var subQ0=sQuery(id+"F10.wireOp",EDGE,"E94.bottom");Q34=makeQuery(id+"F10.imprint","IMPRINT",FACE,{"disambiguationData":[TD([[makeQuery(id+"F10.imprint","IMPRINT",EDGE,{"derivedFrom":subQ0}),1.0]])]});}
            var Q35;
            {var subQ0=sQuery(id+"F10.wireOp",EDGE,"E92.bottom");Q35=makeQuery(id+"F10.imprint","IMPRINT",FACE,{"disambiguationData":[TD([[makeQuery(id+"F10.imprint","IMPRINT",EDGE,{"derivedFrom":subQ0}),1.0]])]});}
            var Q36;
            {var subQ0=sQuery(id+"F10.wireOp",EDGE,"E90.bottom");Q36=makeQuery(id+"F10.imprint","IMPRINT",FACE,{"disambiguationData":[TD([[makeQuery(id+"F10.imprint","IMPRINT",EDGE,{"derivedFrom":subQ0}),1.0]])]});}
            var Q37;
            {var subQ0=sQuery(id+"F10.wireOp",EDGE,"E88.bottom");var subQ1=sQuery(id+"F10.wireOp",EDGE,"E88.left");var subQ2=makeQuery(id+"F10.imprint","INTERSECT",VERTEX,{"derivedFrom":[subQ1,subQ0]});Q37=makeQuery(id+"F10.imprint","IMPRINT",FACE,{"disambiguationData":[TD([[makeQuery(id+"F10.imprint","IMPRINT",EDGE,{"disambiguationData":[TD([[subQ2,-1.0]])],"derivedFrom":subQ1}),-1.0]])]});}
            extrude(context, id + "F11", {"entities" : qUnion([Q0, Q1, Q2, Q3, Q4, Q5, Q6, Q7, Q8, Q9, Q10, Q11, Q12, Q13, Q14, Q15, Q16, Q17, Q18, Q19, Q20, Q21, Q22, Q23, Q24, Q25, Q26, Q27, Q28, Q29, Q30, Q31, Q32, Q33, Q34, Q35, Q36, Q37]), "depth" : 0.35 * mm, "offsetDistance" : 25.4 * mm});
        }
        {
            var Q0;
            Q0=makeQuery(id+"F11.opExtrude","SWEPT_BODY",BODY,{"disambiguationData":[OSD([sQuery(id+"F10.wireOp",EDGE,"E142.top"),sQuery(id+"F10.wireOp",EDGE,"E141.right"),sQuery(id+"F10.wireOp",EDGE,"E154.bottom"),sQuery(id+"F10.wireOp",EDGE,"E157")])]});
            var Q1;
            Q1=makeQuery(id+"FCQHRB49jGmblAJ_62.opExtrude","SWEPT_BODY",BODY,{"disambiguationData":[OSD([sQuery(id+"F10.wireOp",EDGE,"E147.bottom"),sQuery(id+"F10.wireOp",EDGE,"E147.right"),sQuery(id+"F10.wireOp",EDGE,"E147.top"),sQuery(id+"F10.wireOp",EDGE,"E157")])]});
            var Q2;
            Q2=makeQuery(id+"F11.opExtrude","SWEPT_BODY",BODY,{"disambiguationData":[OSD([sQuery(id+"F10.wireOp",EDGE,"E148.top"),sQuery(id+"F10.wireOp",EDGE,"E149.right"),sQuery(id+"F10.wireOp",EDGE,"E157")])]});
            var Q3;
            Q3=makeQuery(id+"F11.opExtrude","SWEPT_BODY",BODY,{"disambiguationData":[OSD([sQuery(id+"F10.wireOp",EDGE,"E147.top"),sQuery(id+"F10.wireOp",EDGE,"E148.left"),sQuery(id+"F10.wireOp",EDGE,"E157")])]});
            var Q4;
            Q4=makeQuery(id+"F11.opExtrude","SWEPT_BODY",BODY,{"disambiguationData":[OSD([sQuery(id+"F10.wireOp",EDGE,"E145.bottom"),sQuery(id+"F10.wireOp",EDGE,"E144.left"),sQuery(id+"F10.wireOp",EDGE,"E145.left"),sQuery(id+"F10.wireOp",EDGE,"E145.top"),sQuery(id+"F10.wireOp",EDGE,"E157")])]});
            var Q5;
            Q5=makeQuery(id+"F11.opExtrude","SWEPT_BODY",BODY,{"disambiguationData":[OSD([sQuery(id+"F10.wireOp",EDGE,"E108.bottom"),sQuery(id+"F10.wireOp",EDGE,"E117.right"),sQuery(id+"F10.wireOp",EDGE,"E147.bottom"),sQuery(id+"F10.wireOp",EDGE,"E146.right"),sQuery(id+"F10.wireOp",EDGE,"E157")])]});
            var Q6;
            Q6=makeQuery(id+"F11.opExtrude","SWEPT_BODY",BODY,{"disambiguationData":[OSD([sQuery(id+"F10.wireOp",EDGE,"E97.bottom"),sQuery(id+"F10.wireOp",EDGE,"E108.right"),sQuery(id+"F10.wireOp",EDGE,"E146.bottom"),sQuery(id+"F10.wireOp",EDGE,"E150.right"),sQuery(id+"F10.wireOp",EDGE,"E157")])]});
            var Q7;
            Q7=makeQuery(id+"FCQHRB49jGmblAJ_62.opExtrude","SWEPT_BODY",BODY,{"disambiguationData":[OSD([sQuery(id+"F10.wireOp",EDGE,"E145.top"),sQuery(id+"F10.wireOp",EDGE,"E156.right"),sQuery(id+"F10.wireOp",EDGE,"E157")])]});
            var Q8;
            Q8=makeQuery(id+"FCQHRB49jGmblAJ_62.opExtrude","SWEPT_BODY",BODY,{"disambiguationData":[OSD([sQuery(id+"F10.wireOp",EDGE,"E150.bottom"),sQuery(id+"F10.wireOp",EDGE,"E150.right"),sQuery(id+"F10.wireOp",EDGE,"E157")])]});
            var Q9;
            Q9=makeQuery(id+"FCQHRB49jGmblAJ_62.opExtrude","SWEPT_BODY",BODY,{"disambiguationData":[OSD([sQuery(id+"F10.wireOp",EDGE,"E148.bottom"),sQuery(id+"F10.wireOp",EDGE,"E148.right"),sQuery(id+"F10.wireOp",EDGE,"E148.left"),sQuery(id+"F10.wireOp",EDGE,"E148.top"),sQuery(id+"F10.wireOp",EDGE,"E157")])]});
            var Q10;
            Q10=makeQuery(id+"FCQHRB49jGmblAJ_62.opExtrude","SWEPT_BODY",BODY,{"disambiguationData":[OSD([sQuery(id+"F10.wireOp",EDGE,"E146.bottom"),sQuery(id+"F10.wireOp",EDGE,"E146.right"),sQuery(id+"F10.wireOp",EDGE,"E157")])]});
            var Q11;
            Q11=makeQuery(id+"FCQHRB49jGmblAJ_62.opExtrude","SWEPT_BODY",BODY,{"disambiguationData":[OSD([sQuery(id+"F10.wireOp",EDGE,"E139.bottom"),sQuery(id+"F10.wireOp",EDGE,"E139.right"),sQuery(id+"F10.wireOp",EDGE,"E149.right"),sQuery(id+"F10.wireOp",EDGE,"E142.top"),sQuery(id+"F10.wireOp",EDGE,"E157")])]});
            var Q12;
            Q12=makeQuery(id+"F11.opExtrude","SWEPT_BODY",BODY,{"disambiguationData":[OSD([sQuery(id+"F10.wireOp",EDGE,"E98.top"),sQuery(id+"F10.wireOp",EDGE,"E97.right"),sQuery(id+"F10.wireOp",EDGE,"E150.bottom"),sQuery(id+"F10.wireOp",EDGE,"E157")])]});
            var Q13;
            Q13=makeQuery(id+"F11.opExtrude","SWEPT_BODY",BODY,{"disambiguationData":[OSD([sQuery(id+"F10.wireOp",EDGE,"E156.bottom"),sQuery(id+"F10.wireOp",EDGE,"E156.right"),sQuery(id+"F10.wireOp",EDGE,"E158")])]});
            var Q14;
            Q14=makeQuery(id+"F11.opExtrude","SWEPT_BODY",BODY,{"disambiguationData":[OSD([sQuery(id+"F10.wireOp",EDGE,"E124.bottom"),sQuery(id+"F10.wireOp",EDGE,"E129.right"),sQuery(id+"F10.wireOp",EDGE,"E139.bottom"),sQuery(id+"F10.wireOp",EDGE,"E148.right")])]});
            var Q15;
            Q15=makeQuery(id+"F11.opExtrude","SWEPT_BODY",BODY,{"disambiguationData":[OSD([sQuery(id+"F10.wireOp",EDGE,"E129.bottom"),sQuery(id+"F10.wireOp",EDGE,"E132.right"),sQuery(id+"F10.wireOp",EDGE,"E139.right"),sQuery(id+"F10.wireOp",EDGE,"E133.bottom")])]});
            var Q16;
            Q16=makeQuery(id+"F11.opExtrude","SWEPT_BODY",BODY,{"disambiguationData":[OSD([sQuery(id+"F10.wireOp",EDGE,"E117.bottom"),sQuery(id+"F10.wireOp",EDGE,"E124.right"),sQuery(id+"F10.wireOp",EDGE,"E147.right"),sQuery(id+"F10.wireOp",EDGE,"E148.bottom")])]});
            var Q17;
            Q17=makeQuery(id+"FCQHRB49jGmblAJ_62.opExtrude","SWEPT_BODY",BODY,{"disambiguationData":[OSD([sQuery(id+"F10.wireOp",EDGE,"E136.bottom"),sQuery(id+"F10.wireOp",EDGE,"E152.left"),sQuery(id+"F10.wireOp",EDGE,"E158")])]});
            var Q18;
            Q18=makeQuery(id+"FCQHRB49jGmblAJ_62.opExtrude","SWEPT_BODY",BODY,{"disambiguationData":[OSD([sQuery(id+"F10.wireOp",EDGE,"E135.bottom"),sQuery(id+"F10.wireOp",EDGE,"E136.right"),sQuery(id+"F10.wireOp",EDGE,"E158")])]});
            var Q19;
            Q19=makeQuery(id+"FCQHRB49jGmblAJ_62.opExtrude","SWEPT_BODY",BODY,{"disambiguationData":[OSD([sQuery(id+"F10.wireOp",EDGE,"E133.bottom"),sQuery(id+"F10.wireOp",EDGE,"E140.right"),sQuery(id+"F10.wireOp",EDGE,"E145.bottom"),sQuery(id+"F10.wireOp",EDGE,"E141.right")])]});
            var Q20;
            Q20=makeQuery(id+"FCQHRB49jGmblAJ_62.opExtrude","SWEPT_BODY",BODY,{"disambiguationData":[OSD([sQuery(id+"F10.wireOp",EDGE,"E144.bottom"),sQuery(id+"F10.wireOp",EDGE,"E144.left"),sQuery(id+"F10.wireOp",EDGE,"E143.right"),sQuery(id+"F10.wireOp",EDGE,"E156.bottom"),sQuery(id+"F10.wireOp",EDGE,"E158")])]});
            var Q21;
            Q21=makeQuery(id+"FCQHRB49jGmblAJ_62.opExtrude","SWEPT_BODY",BODY,{"disambiguationData":[OSD([sQuery(id+"F10.wireOp",EDGE,"E96.bottom"),sQuery(id+"F10.wireOp",EDGE,"E107.right"),sQuery(id+"F10.wireOp",EDGE,"E108.right"),sQuery(id+"F10.wireOp",EDGE,"E108.bottom")])]});
            var Q22;
            Q22=makeQuery(id+"FCQHRB49jGmblAJ_62.opExtrude","SWEPT_BODY",BODY,{"disambiguationData":[OSD([sQuery(id+"F10.wireOp",EDGE,"E107.bottom"),sQuery(id+"F10.wireOp",EDGE,"E116.right"),sQuery(id+"F10.wireOp",EDGE,"E117.right"),sQuery(id+"F10.wireOp",EDGE,"E117.bottom")])]});
            var Q23;
            Q23=makeQuery(id+"FCQHRB49jGmblAJ_62.opExtrude","SWEPT_BODY",BODY,{"disambiguationData":[OSD([sQuery(id+"F10.wireOp",EDGE,"E101.bottom"),sQuery(id+"F10.wireOp",EDGE,"E111.right"),sQuery(id+"F10.wireOp",EDGE,"E110.right"),sQuery(id+"F10.wireOp",EDGE,"E135.top"),sQuery(id+"F10.wireOp",EDGE,"E158")])]});
            var Q24;
            Q24=makeQuery(id+"FCQHRB49jGmblAJ_62.opExtrude","SWEPT_BODY",BODY,{"disambiguationData":[OSD([sQuery(id+"F10.wireOp",EDGE,"E97.top"),sQuery(id+"F10.wireOp",EDGE,"E96.right"),sQuery(id+"F10.wireOp",EDGE,"E97.right"),sQuery(id+"F10.wireOp",EDGE,"E97.bottom")])]});
            var Q25;
            Q25=makeQuery(id+"FCQHRB49jGmblAJ_62.opExtrude","SWEPT_BODY",BODY,{"disambiguationData":[OSD([sQuery(id+"F10.wireOp",EDGE,"E87.bottom"),sQuery(id+"F10.wireOp",EDGE,"E88.left"),sQuery(id+"F10.wireOp",EDGE,"E88.bottom"),sQuery(id+"F10.wireOp",EDGE,"E100.right"),sQuery(id+"F10.wireOp",EDGE,"E87.top"),sQuery(id+"F10.wireOp",EDGE,"E99.right"),sQuery(id+"F10.wireOp",EDGE,"E134.top"),sQuery(id+"F10.wireOp",EDGE,"E158")])]});
            var Q26;
            Q26=makeQuery(id+"F11.opExtrude","SWEPT_BODY",BODY,{"disambiguationData":[OSD([sQuery(id+"F10.wireOp",EDGE,"E132.bottom"),sQuery(id+"F10.wireOp",EDGE,"E140.left"),sQuery(id+"F10.wireOp",EDGE,"E140.right"),sQuery(id+"F10.wireOp",EDGE,"E144.bottom")])]});
            var Q27;
            Q27=makeQuery(id+"F11.opExtrude","SWEPT_BODY",BODY,{"disambiguationData":[OSD([sQuery(id+"F10.wireOp",EDGE,"E127.bottom"),sQuery(id+"F10.wireOp",EDGE,"E137.right"),sQuery(id+"F10.wireOp",EDGE,"E137.top"),sQuery(id+"F10.wireOp",EDGE,"E152.left"),sQuery(id+"F10.wireOp",EDGE,"E158")])]});
            var Q28;
            Q28=makeQuery(id+"F11.opExtrude","SWEPT_BODY",BODY,{"disambiguationData":[OSD([sQuery(id+"F10.wireOp",EDGE,"E136.top"),sQuery(id+"F10.wireOp",EDGE,"E126.right"),sQuery(id+"F10.wireOp",EDGE,"E136.right"),sQuery(id+"F10.wireOp",EDGE,"E136.bottom"),sQuery(id+"F10.wireOp",EDGE,"E158")])]});
            var Q29;
            Q29=makeQuery(id+"F11.opExtrude","SWEPT_BODY",BODY,{"disambiguationData":[OSD([sQuery(id+"F10.wireOp",EDGE,"E134.top"),sQuery(id+"F10.wireOp",EDGE,"E110.right"),sQuery(id+"F10.wireOp",EDGE,"E158")])]});
            var Q30;
            Q30=makeQuery(id+"F11.opExtrude","SWEPT_BODY",BODY,{"disambiguationData":[OSD([sQuery(id+"F10.wireOp",EDGE,"E87.top"),sQuery(id+"F10.wireOp",EDGE,"E99.right"),sQuery(id+"F10.wireOp",EDGE,"E158")])]});
            var Q31;
            Q31=makeQuery(id+"F11.opExtrude","SWEPT_BODY",BODY,{"disambiguationData":[OSD([sQuery(id+"F10.wireOp",EDGE,"E106.bottom"),sQuery(id+"F10.wireOp",EDGE,"E115.right"),sQuery(id+"F10.wireOp",EDGE,"E116.right"),sQuery(id+"F10.wireOp",EDGE,"E116.bottom")])]});
            var Q32;
            Q32=makeQuery(id+"F11.opExtrude","SWEPT_BODY",BODY,{"disambiguationData":[OSD([sQuery(id+"F10.wireOp",EDGE,"E95.bottom"),sQuery(id+"F10.wireOp",EDGE,"E106.right"),sQuery(id+"F10.wireOp",EDGE,"E107.right"),sQuery(id+"F10.wireOp",EDGE,"E107.bottom")])]});
            var Q33;
            Q33=makeQuery(id+"FCQHRB49jGmblAJ_62.opExtrude","SWEPT_BODY",BODY,{"disambiguationData":[OSD([sQuery(id+"F10.wireOp",EDGE,"E128.bottom"),sQuery(id+"F10.wireOp",EDGE,"E132.right"),sQuery(id+"F10.wireOp",EDGE,"E137.right"),sQuery(id+"F10.wireOp",EDGE,"E132.bottom")])]});
            var Q34;
            Q34=makeQuery(id+"FCQHRB49jGmblAJ_62.opExtrude","SWEPT_BODY",BODY,{"disambiguationData":[OSD([sQuery(id+"F10.wireOp",EDGE,"E123.bottom"),sQuery(id+"F10.wireOp",EDGE,"E128.right"),sQuery(id+"F10.wireOp",EDGE,"E129.right"),sQuery(id+"F10.wireOp",EDGE,"E129.bottom")])]});
            var Q35;
            Q35=makeQuery(id+"FCQHRB49jGmblAJ_62.opExtrude","SWEPT_BODY",BODY,{"disambiguationData":[OSD([sQuery(id+"F10.wireOp",EDGE,"E116.bottom"),sQuery(id+"F10.wireOp",EDGE,"E123.right"),sQuery(id+"F10.wireOp",EDGE,"E124.right"),sQuery(id+"F10.wireOp",EDGE,"E124.bottom")])]});
            var Q36;
            Q36=makeQuery(id+"F11.opExtrude","SWEPT_BODY",BODY,{"disambiguationData":[OSD([sQuery(id+"F10.wireOp",EDGE,"E96.top"),sQuery(id+"F10.wireOp",EDGE,"E95.right"),sQuery(id+"F10.wireOp",EDGE,"E96.right"),sQuery(id+"F10.wireOp",EDGE,"E96.bottom")])]});
            var Q37;
            Q37=makeQuery(id+"F11.opExtrude","SWEPT_BODY",BODY,{"disambiguationData":[OSD([sQuery(id+"F10.wireOp",EDGE,"E122.bottom"),sQuery(id+"F10.wireOp",EDGE,"E127.right"),sQuery(id+"F10.wireOp",EDGE,"E128.right"),sQuery(id+"F10.wireOp",EDGE,"E128.bottom")])]});
            var Q38;
            Q38=makeQuery(id+"F11.opExtrude","SWEPT_BODY",BODY,{"disambiguationData":[OSD([sQuery(id+"F10.wireOp",EDGE,"E115.bottom"),sQuery(id+"F10.wireOp",EDGE,"E122.right"),sQuery(id+"F10.wireOp",EDGE,"E123.right"),sQuery(id+"F10.wireOp",EDGE,"E123.bottom")])]});
            var Q39;
            Q39=makeQuery(id+"FCQHRB49jGmblAJ_62.opExtrude","SWEPT_BODY",BODY,{"disambiguationData":[OSD([sQuery(id+"F10.wireOp",EDGE,"E137.top"),sQuery(id+"F10.wireOp",EDGE,"E140.left"),sQuery(id+"F10.wireOp",EDGE,"E155.bottom"),sQuery(id+"F10.wireOp",EDGE,"E158")])]});
            var Q40;
            Q40=makeQuery(id+"FCQHRB49jGmblAJ_62.opExtrude","SWEPT_BODY",BODY,{"disambiguationData":[OSD([sQuery(id+"F10.wireOp",EDGE,"E105.bottom"),sQuery(id+"F10.wireOp",EDGE,"E114.right"),sQuery(id+"F10.wireOp",EDGE,"E115.right"),sQuery(id+"F10.wireOp",EDGE,"E115.bottom")])]});
            var Q41;
            Q41=makeQuery(id+"FCQHRB49jGmblAJ_62.opExtrude","SWEPT_BODY",BODY,{"disambiguationData":[OSD([sQuery(id+"F10.wireOp",EDGE,"E94.bottom"),sQuery(id+"F10.wireOp",EDGE,"E105.right"),sQuery(id+"F10.wireOp",EDGE,"E106.right"),sQuery(id+"F10.wireOp",EDGE,"E106.bottom")])]});
            var Q42;
            Q42=makeQuery(id+"FCQHRB49jGmblAJ_62.opExtrude","SWEPT_BODY",BODY,{"disambiguationData":[OSD([sQuery(id+"F10.wireOp",EDGE,"E95.top"),sQuery(id+"F10.wireOp",EDGE,"E94.right"),sQuery(id+"F10.wireOp",EDGE,"E95.right"),sQuery(id+"F10.wireOp",EDGE,"E95.bottom")])]});
            var Q43;
            Q43=makeQuery(id+"F11.opExtrude","SWEPT_BODY",BODY,{"disambiguationData":[OSD([sQuery(id+"F10.wireOp",EDGE,"E104.bottom"),sQuery(id+"F10.wireOp",EDGE,"E113.right"),sQuery(id+"F10.wireOp",EDGE,"E114.right"),sQuery(id+"F10.wireOp",EDGE,"E114.bottom")])]});
            var Q44;
            Q44=makeQuery(id+"FCQHRB49jGmblAJ_62.opExtrude","SWEPT_BODY",BODY,{"disambiguationData":[OSD([sQuery(id+"F10.wireOp",EDGE,"E121.bottom"),sQuery(id+"F10.wireOp",EDGE,"E127.right"),sQuery(id+"F10.wireOp",EDGE,"E126.right"),sQuery(id+"F10.wireOp",EDGE,"E127.bottom")])]});
            var Q45;
            Q45=makeQuery(id+"FCQHRB49jGmblAJ_62.opExtrude","SWEPT_BODY",BODY,{"disambiguationData":[OSD([sQuery(id+"F10.wireOp",EDGE,"E114.bottom"),sQuery(id+"F10.wireOp",EDGE,"E121.right"),sQuery(id+"F10.wireOp",EDGE,"E122.right"),sQuery(id+"F10.wireOp",EDGE,"E122.bottom")])]});
            var Q46;
            Q46=makeQuery(id+"F11.opExtrude","SWEPT_BODY",BODY,{"disambiguationData":[OSD([sQuery(id+"F10.wireOp",EDGE,"E93.bottom"),sQuery(id+"F10.wireOp",EDGE,"E104.right"),sQuery(id+"F10.wireOp",EDGE,"E105.right"),sQuery(id+"F10.wireOp",EDGE,"E105.bottom")])]});
            var Q47;
            Q47=makeQuery(id+"F11.opExtrude","SWEPT_BODY",BODY,{"disambiguationData":[OSD([sQuery(id+"F10.wireOp",EDGE,"E94.top"),sQuery(id+"F10.wireOp",EDGE,"E93.right"),sQuery(id+"F10.wireOp",EDGE,"E94.right"),sQuery(id+"F10.wireOp",EDGE,"E94.bottom")])]});
            var Q48;
            Q48=makeQuery(id+"F11.opExtrude","SWEPT_BODY",BODY,{"disambiguationData":[OSD([sQuery(id+"F10.wireOp",EDGE,"E113.bottom"),sQuery(id+"F10.wireOp",EDGE,"E120.right"),sQuery(id+"F10.wireOp",EDGE,"E121.right"),sQuery(id+"F10.wireOp",EDGE,"E121.bottom")])]});
            var Q49;
            Q49=makeQuery(id+"FCQHRB49jGmblAJ_62.opExtrude","SWEPT_BODY",BODY,{"disambiguationData":[OSD([sQuery(id+"F10.wireOp",EDGE,"E103.bottom"),sQuery(id+"F10.wireOp",EDGE,"E112.right"),sQuery(id+"F10.wireOp",EDGE,"E113.right"),sQuery(id+"F10.wireOp",EDGE,"E113.bottom")])]});
            var Q50;
            Q50=makeQuery(id+"FCQHRB49jGmblAJ_62.opExtrude","SWEPT_BODY",BODY,{"disambiguationData":[OSD([sQuery(id+"F10.wireOp",EDGE,"E92.bottom"),sQuery(id+"F10.wireOp",EDGE,"E103.right"),sQuery(id+"F10.wireOp",EDGE,"E104.right"),sQuery(id+"F10.wireOp",EDGE,"E104.bottom")])]});
            var Q51;
            Q51=makeQuery(id+"FCQHRB49jGmblAJ_62.opExtrude","SWEPT_BODY",BODY,{"disambiguationData":[OSD([sQuery(id+"F10.wireOp",EDGE,"E93.top"),sQuery(id+"F10.wireOp",EDGE,"E92.right"),sQuery(id+"F10.wireOp",EDGE,"E93.right"),sQuery(id+"F10.wireOp",EDGE,"E93.bottom")])]});
            var Q52;
            Q52=makeQuery(id+"F11.opExtrude","SWEPT_BODY",BODY,{"disambiguationData":[OSD([sQuery(id+"F10.wireOp",EDGE,"E92.top"),sQuery(id+"F10.wireOp",EDGE,"E91.right"),sQuery(id+"F10.wireOp",EDGE,"E92.right"),sQuery(id+"F10.wireOp",EDGE,"E92.bottom")])]});
            var Q53;
            Q53=makeQuery(id+"F11.opExtrude","SWEPT_BODY",BODY,{"disambiguationData":[OSD([sQuery(id+"F10.wireOp",EDGE,"E102.bottom"),sQuery(id+"F10.wireOp",EDGE,"E111.right"),sQuery(id+"F10.wireOp",EDGE,"E112.right"),sQuery(id+"F10.wireOp",EDGE,"E112.bottom")])]});
            var Q54;
            Q54=makeQuery(id+"FCQHRB49jGmblAJ_62.opExtrude","SWEPT_BODY",BODY,{"disambiguationData":[OSD([sQuery(id+"F10.wireOp",EDGE,"E112.bottom"),sQuery(id+"F10.wireOp",EDGE,"E120.right"),sQuery(id+"F10.wireOp",EDGE,"E119.right"),sQuery(id+"F10.wireOp",EDGE,"E136.top")])]});
            var Q55;
            Q55=makeQuery(id+"F11.opExtrude","SWEPT_BODY",BODY,{"disambiguationData":[OSD([sQuery(id+"F10.wireOp",EDGE,"E91.bottom"),sQuery(id+"F10.wireOp",EDGE,"E102.right"),sQuery(id+"F10.wireOp",EDGE,"E103.right"),sQuery(id+"F10.wireOp",EDGE,"E103.bottom")])]});
            var Q56;
            Q56=makeQuery(id+"F11.opExtrude","SWEPT_BODY",BODY,{"disambiguationData":[OSD([sQuery(id+"F10.wireOp",EDGE,"E135.top"),sQuery(id+"F10.wireOp",EDGE,"E119.right"),sQuery(id+"F10.wireOp",EDGE,"E135.bottom"),sQuery(id+"F10.wireOp",EDGE,"E158")])]});
            var Q57;
            Q57=makeQuery(id+"FCQHRB49jGmblAJ_62.opExtrude","SWEPT_BODY",BODY,{"disambiguationData":[OSD([sQuery(id+"F10.wireOp",EDGE,"E90.bottom"),sQuery(id+"F10.wireOp",EDGE,"E101.right"),sQuery(id+"F10.wireOp",EDGE,"E102.right"),sQuery(id+"F10.wireOp",EDGE,"E102.bottom")])]});
            var Q58;
            Q58=makeQuery(id+"FCQHRB49jGmblAJ_62.opExtrude","SWEPT_BODY",BODY,{"disambiguationData":[OSD([sQuery(id+"F10.wireOp",EDGE,"E91.top"),sQuery(id+"F10.wireOp",EDGE,"E90.right"),sQuery(id+"F10.wireOp",EDGE,"E91.right"),sQuery(id+"F10.wireOp",EDGE,"E91.bottom")])]});
            var Q59;
            Q59=makeQuery(id+"F11.opExtrude","SWEPT_BODY",BODY,{"disambiguationData":[OSD([sQuery(id+"F10.wireOp",EDGE,"E90.top"),sQuery(id+"F10.wireOp",EDGE,"E89.right"),sQuery(id+"F10.wireOp",EDGE,"E90.right"),sQuery(id+"F10.wireOp",EDGE,"E90.bottom")])]});
            var Q60;
            Q60=makeQuery(id+"F11.opExtrude","SWEPT_BODY",BODY,{"disambiguationData":[OSD([sQuery(id+"F10.wireOp",EDGE,"E89.bottom"),sQuery(id+"F10.wireOp",EDGE,"E100.right"),sQuery(id+"F10.wireOp",EDGE,"E101.right"),sQuery(id+"F10.wireOp",EDGE,"E101.bottom")])]});
            var Q61;
            Q61=makeQuery(id+"FCQHRB49jGmblAJ_62.opExtrude","SWEPT_BODY",BODY,{"disambiguationData":[OSD([sQuery(id+"F10.wireOp",EDGE,"E89.top"),sQuery(id+"F10.wireOp",EDGE,"E88.right"),sQuery(id+"F10.wireOp",EDGE,"E89.right"),sQuery(id+"F10.wireOp",EDGE,"E89.bottom")])]});
            var Q62;
            Q62=makeQuery(id+"F11.opExtrude","SWEPT_BODY",BODY,{"disambiguationData":[OSD([sQuery(id+"F10.wireOp",EDGE,"E88.top"),sQuery(id+"F10.wireOp",EDGE,"E88.left"),sQuery(id+"F10.wireOp",EDGE,"E88.right"),sQuery(id+"F10.wireOp",EDGE,"E88.bottom")])]});
            var Q63;
            Q63=sQuery(id+"F10.wireOp",EDGE,"E159");
            transform(context, id + "F12", {"entities" : qUnion([Q0, Q1, Q2, Q3, Q4, Q5, Q6, Q7, Q8, Q9, Q10, Q11, Q12, Q13, Q14, Q15, Q16, Q17, Q18, Q19, Q20, Q21, Q22, Q23, Q24, Q25, Q26, Q27, Q28, Q29, Q30, Q31, Q32, Q33, Q34, Q35, Q36, Q37, Q38, Q39, Q40, Q41, Q42, Q43, Q44, Q45, Q46, Q47, Q48, Q49, Q50, Q51, Q52, Q53, Q54, Q55, Q56, Q57, Q58, Q59, Q60, Q61, Q62]), "transformType" : TransformType.ROTATION, "transformAxis" : qUnion([Q63]), "angle" : 45 * degree, "oppositeDirection" : true, "makeCopy" : false});
        }
        {
            var Q0;
            Q0=qCreatedBy(makeId("Front.planeOp"),FACE);
            var sketch = newSketch(context, id + "F13", { "sketchPlane" : qUnion([Q0])});
            skLineSegment(sketch, "E160.bottom", {"start": v(0, 0) * mm, "end": v(-1, 0) * mm});
            skLineSegment(sketch, "E160.top", {"start": v(-0.7, 1) * mm, "end": v(-1, 1) * mm});
            skLineSegment(sketch, "E160.right", {"start": v(-1, 0) * mm, "end": v(-1, 1) * mm});
            skLineSegment(sketch, "E161.bottom", {"start": v(-1, 1) * mm, "end": v(-2, 1) * mm});
            skLineSegment(sketch, "E161.top", {"start": v(-1, 0) * mm, "end": v(-2, 0) * mm});
            skLineSegment(sketch, "E161.left", {"start": v(-1, 1) * mm, "end": v(-1, 0) * mm});
            skLineSegment(sketch, "E161.right", {"start": v(-2, 1) * mm, "end": v(-2, 0) * mm});
            skLineSegment(sketch, "E162.bottom", {"start": v(-2, 1) * mm, "end": v(-3, 1) * mm});
            skLineSegment(sketch, "E162.top", {"start": v(-2, 0) * mm, "end": v(-3, 0) * mm});
            skLineSegment(sketch, "E162.right", {"start": v(-3, 1) * mm, "end": v(-3, 0) * mm});
            skLineSegment(sketch, "E163.bottom", {"start": v(-3, 1) * mm, "end": v(-4, 1) * mm});
            skLineSegment(sketch, "E163.top", {"start": v(-3, 0) * mm, "end": v(-4, 0) * mm});
            skLineSegment(sketch, "E163.right", {"start": v(-4, 1) * mm, "end": v(-4, 0) * mm});
            skLineSegment(sketch, "E164.bottom", {"start": v(-4, 1) * mm, "end": v(-5, 1) * mm});
            skLineSegment(sketch, "E164.top", {"start": v(-4, 0) * mm, "end": v(-5, 0) * mm});
            skLineSegment(sketch, "E164.right", {"start": v(-5, 1) * mm, "end": v(-5, 0) * mm});
            skLineSegment(sketch, "E165.bottom", {"start": v(-5, 1) * mm, "end": v(-6, 1) * mm});
            skLineSegment(sketch, "E165.top", {"start": v(-5, 0) * mm, "end": v(-6, 0) * mm});
            skLineSegment(sketch, "E165.right", {"start": v(-6, 1) * mm, "end": v(-6, 0) * mm});
            skLineSegment(sketch, "E166.bottom", {"start": v(-6, 1) * mm, "end": v(-7, 1) * mm});
            skLineSegment(sketch, "E166.top", {"start": v(-6, 0) * mm, "end": v(-7, 0) * mm});
            skLineSegment(sketch, "E166.right", {"start": v(-7, 1) * mm, "end": v(-7, 0) * mm});
            skLineSegment(sketch, "E167.bottom", {"start": v(-7, 1) * mm, "end": v(-8, 1) * mm});
            skLineSegment(sketch, "E167.top", {"start": v(-7, 0) * mm, "end": v(-8, 0) * mm});
            skLineSegment(sketch, "E167.right", {"start": v(-8, 1) * mm, "end": v(-8, 0) * mm});
            skLineSegment(sketch, "E168.bottom", {"start": v(-8, 1) * mm, "end": v(-9, 1) * mm});
            skLineSegment(sketch, "E168.top", {"start": v(-8, 0) * mm, "end": v(-9, 0) * mm});
            skLineSegment(sketch, "E168.right", {"start": v(-9, 1) * mm, "end": v(-9, 0) * mm});
            skLineSegment(sketch, "E169.bottom", {"start": v(-9, 1) * mm, "end": v(-10, 1) * mm});
            skLineSegment(sketch, "E169.top", {"start": v(-9, 0) * mm, "end": v(-10, 0) * mm});
            skLineSegment(sketch, "E169.right", {"start": v(-10, 1) * mm, "end": v(-10, 0) * mm});
            skLineSegment(sketch, "E170.bottom", {"start": v(-10, 1) * mm, "end": v(-11, 1) * mm});
            skLineSegment(sketch, "E170.top", {"start": v(-10, 0) * mm, "end": v(-11, 0) * mm});
            skLineSegment(sketch, "E170.right", {"start": v(-11, 1) * mm, "end": v(-11, 0) * mm});
            skLineSegment(sketch, "E171.bottom", {"start": v(-11, 1) * mm, "end": v(-11.3, 1) * mm});
            skLineSegment(sketch, "E171.top", {"start": v(-11, 0) * mm, "end": v(-12, 0) * mm});
            skLineSegment(sketch, "E172.right", {"start": v(-1, 1) * mm, "end": v(-1, 1.4) * mm});
            skLineSegment(sketch, "E173.bottom", {"start": v(-1.41, 2) * mm, "end": v(-2, 2) * mm});
            skLineSegment(sketch, "E173.left", {"start": v(-1, 1.4) * mm, "end": v(-1, 1) * mm});
            skLineSegment(sketch, "E173.right", {"start": v(-2, 2) * mm, "end": v(-2, 1) * mm});
            skLineSegment(sketch, "E174.bottom", {"start": v(-2, 2) * mm, "end": v(-3, 2) * mm});
            skLineSegment(sketch, "E174.right", {"start": v(-3, 2) * mm, "end": v(-3, 1) * mm});
            skLineSegment(sketch, "E175.bottom", {"start": v(-3, 2) * mm, "end": v(-4, 2) * mm});
            skLineSegment(sketch, "E175.right", {"start": v(-4, 2) * mm, "end": v(-4, 1) * mm});
            skLineSegment(sketch, "E176.bottom", {"start": v(-4, 2) * mm, "end": v(-5, 2) * mm});
            skLineSegment(sketch, "E176.right", {"start": v(-5, 2) * mm, "end": v(-5, 1) * mm});
            skLineSegment(sketch, "E177.bottom", {"start": v(-5, 2) * mm, "end": v(-6, 2) * mm});
            skLineSegment(sketch, "E177.right", {"start": v(-6, 2) * mm, "end": v(-6, 1) * mm});
            skLineSegment(sketch, "E178.bottom", {"start": v(-6, 2) * mm, "end": v(-7, 2) * mm});
            skLineSegment(sketch, "E178.right", {"start": v(-7, 2) * mm, "end": v(-7, 1) * mm});
            skLineSegment(sketch, "E179.bottom", {"start": v(-7, 2) * mm, "end": v(-8, 2) * mm});
            skLineSegment(sketch, "E179.right", {"start": v(-8, 2) * mm, "end": v(-8, 1) * mm});
            skLineSegment(sketch, "E180.bottom", {"start": v(-8, 2) * mm, "end": v(-9, 2) * mm});
            skLineSegment(sketch, "E180.right", {"start": v(-9, 2) * mm, "end": v(-9, 1) * mm});
            skLineSegment(sketch, "E181.bottom", {"start": v(-9, 2) * mm, "end": v(-10, 2) * mm});
            skLineSegment(sketch, "E181.right", {"start": v(-10, 2) * mm, "end": v(-10, 1) * mm});
            skLineSegment(sketch, "E182.bottom", {"start": v(-10, 2) * mm, "end": v(-10.59, 2) * mm});
            skLineSegment(sketch, "E182.right", {"start": v(-11, 1.41) * mm, "end": v(-11, 1) * mm});
            skLineSegment(sketch, "E183.right", {"start": v(-2, 2.83) * mm, "end": v(-2, 2) * mm});
            skLineSegment(sketch, "E184.bottom", {"start": v(-2.12, 3) * mm, "end": v(-3, 3) * mm});
            skLineSegment(sketch, "E184.right", {"start": v(-3, 3) * mm, "end": v(-3, 2) * mm});
            skLineSegment(sketch, "E185.bottom", {"start": v(-3, 3) * mm, "end": v(-4, 3) * mm});
            skLineSegment(sketch, "E185.right", {"start": v(-4, 3) * mm, "end": v(-4, 2) * mm});
            skLineSegment(sketch, "E186.bottom", {"start": v(-4, 3) * mm, "end": v(-5, 3) * mm});
            skLineSegment(sketch, "E186.right", {"start": v(-5, 3) * mm, "end": v(-5, 2) * mm});
            skLineSegment(sketch, "E187.bottom", {"start": v(-5, 3) * mm, "end": v(-6, 3) * mm});
            skLineSegment(sketch, "E187.right", {"start": v(-6, 3) * mm, "end": v(-6, 2) * mm});
            skLineSegment(sketch, "E188.bottom", {"start": v(-6, 3) * mm, "end": v(-7, 3) * mm});
            skLineSegment(sketch, "E188.right", {"start": v(-7, 3) * mm, "end": v(-7, 2) * mm});
            skLineSegment(sketch, "E189.bottom", {"start": v(-7, 3) * mm, "end": v(-8, 3) * mm});
            skLineSegment(sketch, "E189.right", {"start": v(-8, 3) * mm, "end": v(-8, 2) * mm});
            skLineSegment(sketch, "E190.bottom", {"start": v(-8, 3) * mm, "end": v(-9, 3) * mm});
            skLineSegment(sketch, "E190.right", {"start": v(-9, 3) * mm, "end": v(-9, 2) * mm});
            skLineSegment(sketch, "E191.bottom", {"start": v(-9, 3) * mm, "end": v(-9.88, 3) * mm});
            skLineSegment(sketch, "E191.right", {"start": v(-10, 2.83) * mm, "end": v(-10, 2) * mm});
            skLineSegment(sketch, "E192.right", {"start": v(-3, 4) * mm, "end": v(-3, 3) * mm});
            skLineSegment(sketch, "E193.bottom", {"start": v(-3, 4) * mm, "end": v(-4, 4) * mm});
            skLineSegment(sketch, "E193.right", {"start": v(-4, 4) * mm, "end": v(-4, 3) * mm});
            skLineSegment(sketch, "E194.bottom", {"start": v(-4, 4) * mm, "end": v(-5, 4) * mm});
            skLineSegment(sketch, "E194.right", {"start": v(-5, 4) * mm, "end": v(-5, 3) * mm});
            skLineSegment(sketch, "E195.bottom", {"start": v(-5, 4) * mm, "end": v(-6, 4) * mm});
            skLineSegment(sketch, "E195.right", {"start": v(-6, 4) * mm, "end": v(-6, 3) * mm});
            skLineSegment(sketch, "E196.bottom", {"start": v(-6, 4) * mm, "end": v(-7, 4) * mm});
            skLineSegment(sketch, "E196.right", {"start": v(-7, 4) * mm, "end": v(-7, 3) * mm});
            skLineSegment(sketch, "E197.bottom", {"start": v(-7, 4) * mm, "end": v(-8, 4) * mm});
            skLineSegment(sketch, "E197.right", {"start": v(-8, 4) * mm, "end": v(-8, 3) * mm});
            skLineSegment(sketch, "E198.bottom", {"start": v(-8, 4) * mm, "end": v(-9, 4) * mm});
            skLineSegment(sketch, "E198.right", {"start": v(-9, 4) * mm, "end": v(-9, 3) * mm});
            skLineSegment(sketch, "E199.right", {"start": v(-4, 5) * mm, "end": v(-4, 4) * mm});
            skLineSegment(sketch, "E200.bottom", {"start": v(-4, 5) * mm, "end": v(-5, 5) * mm});
            skLineSegment(sketch, "E200.right", {"start": v(-5, 5) * mm, "end": v(-5, 4) * mm});
            skLineSegment(sketch, "E201.bottom", {"start": v(-5, 5) * mm, "end": v(-6, 5) * mm});
            skLineSegment(sketch, "E201.right", {"start": v(-6, 5) * mm, "end": v(-6, 4) * mm});
            skLineSegment(sketch, "E202.bottom", {"start": v(-6, 5) * mm, "end": v(-7, 5) * mm});
            skLineSegment(sketch, "E202.right", {"start": v(-7, 5) * mm, "end": v(-7, 4) * mm});
            skLineSegment(sketch, "E203.bottom", {"start": v(-7, 5) * mm, "end": v(-8, 5) * mm});
            skLineSegment(sketch, "E203.right", {"start": v(-8, 5) * mm, "end": v(-8, 4) * mm});
            skLineSegment(sketch, "E204.right", {"start": v(-5, 6) * mm, "end": v(-5, 5) * mm});
            skLineSegment(sketch, "E205.bottom", {"start": v(-5, 6) * mm, "end": v(-6, 6) * mm});
            skLineSegment(sketch, "E205.right", {"start": v(-6, 6) * mm, "end": v(-6, 5) * mm});
            skLineSegment(sketch, "E206.bottom", {"start": v(-6, 6) * mm, "end": v(-7, 6) * mm});
            skLineSegment(sketch, "E206.right", {"start": v(-7, 6) * mm, "end": v(-7, 5) * mm});
            skLineSegment(sketch, "E207.top", {"start": v(-2, 2) * mm, "end": v(-1.41, 2) * mm});
            skLineSegment(sketch, "E208.bottom", {"start": v(-3, 4) * mm, "end": v(-2.83, 4) * mm});
            skLineSegment(sketch, "E208.top", {"start": v(-3, 3) * mm, "end": v(-2.12, 3) * mm});
            skLineSegment(sketch, "E209.bottom", {"start": v(-4, 5) * mm, "end": v(-3.54, 5) * mm});
            skLineSegment(sketch, "E209.top", {"start": v(-4, 4) * mm, "end": v(-3, 4) * mm});
            skLineSegment(sketch, "E209.right", {"start": v(-3, 4.24) * mm, "end": v(-3, 4) * mm});
            skLineSegment(sketch, "E210.top", {"start": v(-4.24, 6) * mm, "end": v(-5, 6) * mm});
            skLineSegment(sketch, "E210.left", {"start": v(-4, 5) * mm, "end": v(-4, 5.65) * mm});
            skLineSegment(sketch, "E210.right", {"start": v(-5, 5) * mm, "end": v(-5, 6) * mm});
            skLineSegment(sketch, "E211.right", {"start": v(-5, 6) * mm, "end": v(-5, 7) * mm});
            skLineSegment(sketch, "E212.bottom", {"start": v(-8, 5) * mm, "end": v(-7, 5) * mm});
            skLineSegment(sketch, "E212.top", {"start": v(-7.76, 6) * mm, "end": v(-7, 6) * mm});
            skLineSegment(sketch, "E212.right", {"start": v(-7, 5) * mm, "end": v(-7, 6) * mm});
            skLineSegment(sketch, "E213.bottom", {"start": v(-5, 7) * mm, "end": v(-6, 7) * mm});
            skLineSegment(sketch, "E213.left", {"start": v(-5, 7) * mm, "end": v(-5, 6) * mm});
            skLineSegment(sketch, "E213.right", {"start": v(-6, 7) * mm, "end": v(-6, 6) * mm});
            skLineSegment(sketch, "E214.bottom", {"start": v(-6, 7) * mm, "end": v(-7, 7) * mm});
            skLineSegment(sketch, "E214.right", {"start": v(-7, 7) * mm, "end": v(-7, 6) * mm});
            skLineSegment(sketch, "E215.top", {"start": v(-7, 6) * mm, "end": v(-7.76, 6) * mm});
            skLineSegment(sketch, "E216.right", {"start": v(-5, 7) * mm, "end": v(-5, 7.07) * mm});
            skLineSegment(sketch, "E217.bottom", {"start": v(-6, 7) * mm, "end": v(-5, 7) * mm});
            skLineSegment(sketch, "E217.top", {"start": v(-6, 8.05) * mm, "end": v(-5.7, 8.05) * mm});
            skLineSegment(sketch, "E217.left", {"start": v(-6, 7) * mm, "end": v(-6, 8.05) * mm});
            skLineSegment(sketch, "E218.bottom", {"start": v(-7, 7) * mm, "end": v(-6, 7) * mm});
            skLineSegment(sketch, "E218.top", {"start": v(-6.3, 8.05) * mm, "end": v(-6, 8.05) * mm});
            skLineSegment(sketch, "E218.left", {"start": v(-7, 7) * mm, "end": v(-7, 7.07) * mm});
            skLineSegment(sketch, "E219.bottom", {"start": v(-10.59, 2) * mm, "end": v(-10, 2) * mm});
            skLineSegment(sketch, "E219.right", {"start": v(-10, 2) * mm, "end": v(-10, 2.83) * mm});
            skLineSegment(sketch, "E220.bottom", {"start": v(-9.88, 3) * mm, "end": v(-9, 3) * mm});
            skLineSegment(sketch, "E220.top", {"start": v(-9.17, 4) * mm, "end": v(-9, 4) * mm});
            skLineSegment(sketch, "E220.right", {"start": v(-9, 3) * mm, "end": v(-9, 4) * mm});
            skLineSegment(sketch, "E221.bottom", {"start": v(-9, 4) * mm, "end": v(-8, 4) * mm});
            skLineSegment(sketch, "E221.top", {"start": v(-8.46, 5) * mm, "end": v(-8, 5) * mm});
            skLineSegment(sketch, "E221.left", {"start": v(-9, 4) * mm, "end": v(-9, 4.24) * mm});
            skLineSegment(sketch, "E221.right", {"start": v(-8, 4) * mm, "end": v(-8, 5) * mm});
            skLineSegment(sketch, "E222.right", {"start": v(-8, 5) * mm, "end": v(-8, 5.65) * mm});
            skLineSegment(sketch, "E223.bottom", {"start": v(-11.3, 1) * mm, "end": v(-11, 1) * mm});
            skLineSegment(sketch, "E223.right", {"start": v(-11, 1) * mm, "end": v(-11, 1.41) * mm});
            skLineSegment(sketch, "E224.bottom", {"start": v(-2.83, 4) * mm, "end": v(-3, 4) * mm});
            skLineSegment(sketch, "E224.right", {"start": v(-3, 4) * mm, "end": v(-3, 4.24) * mm});
            skLineSegment(sketch, "E225.left", {"start": v(-4, 5.65) * mm, "end": v(-4, 5) * mm});
            skLineSegment(sketch, "E226.bottom", {"start": v(-7, 7) * mm, "end": v(-7.05, 7) * mm});
            skLineSegment(sketch, "E227.bottom", {"start": v(-7.05, 7) * mm, "end": v(-7, 7) * mm});
            skLineSegment(sketch, "E228.bottom", {"start": v(-4.95, 7) * mm, "end": v(-5, 7) * mm});
            skLineSegment(sketch, "E229.bottom", {"start": v(-5.7, 8.05) * mm, "end": v(-6, 8.05) * mm});
            skLineSegment(sketch, "E229.right", {"start": v(-6, 8.05) * mm, "end": v(-6, 8.48) * mm});
            skLineSegment(sketch, "E230", {"start": v(-12, 0) * mm, "end": v(-6, 8.48) * mm});
            skLineSegment(sketch, "E231", {"start": v(-6, 8.48) * mm, "end": v(0, 0) * mm});
            skSolve(sketch);
        }
        {
            var Q0;
            {var subQ0=sQuery(id+"F13.wireOp",EDGE,"E171.top");Q0=makeQuery(id+"F13.imprint","IMPRINT",FACE,{"disambiguationData":[TD([[makeQuery(id+"F13.imprint","IMPRINT",EDGE,{"derivedFrom":subQ0}),-1.0]])]});}
            var Q1;
            Q1=makeQuery(id+"F13.imprint","IMPRINT",FACE,{"disambiguationData":[TD([[makeQuery(id+"F13.imprint","IMPRINT",EDGE,{"derivedFrom":sQuery(id+"F13.wireOp",EDGE,"E170.bottom")}),-1.0]])]});
            var Q2;
            Q2=makeQuery(id+"F13.imprint","IMPRINT",FACE,{"disambiguationData":[TD([[makeQuery(id+"F13.imprint","IMPRINT",EDGE,{"derivedFrom":sQuery(id+"F13.wireOp",EDGE,"E169.top")}),-1.0]])]});
            var Q3;
            Q3=makeQuery(id+"F13.imprint","IMPRINT",FACE,{"disambiguationData":[TD([[makeQuery(id+"F13.imprint","IMPRINT",EDGE,{"derivedFrom":sQuery(id+"F13.wireOp",EDGE,"E181.bottom")}),-1.0]])]});
            var Q4;
            Q4=makeQuery(id+"F13.imprint","IMPRINT",FACE,{"disambiguationData":[TD([[makeQuery(id+"F13.imprint","IMPRINT",EDGE,{"derivedFrom":sQuery(id+"F13.wireOp",EDGE,"E168.bottom")}),-1.0]])]});
            var Q5;
            Q5=makeQuery(id+"F13.imprint","IMPRINT",FACE,{"disambiguationData":[TD([[makeQuery(id+"F13.imprint","IMPRINT",EDGE,{"derivedFrom":sQuery(id+"F13.wireOp",EDGE,"E167.top")}),-1.0]])]});
            var Q6;
            Q6=makeQuery(id+"F13.imprint","IMPRINT",FACE,{"disambiguationData":[TD([[makeQuery(id+"F13.imprint","IMPRINT",EDGE,{"derivedFrom":sQuery(id+"F13.wireOp",EDGE,"E179.bottom")}),-1.0]])]});
            var Q7;
            Q7=makeQuery(id+"F13.imprint","IMPRINT",FACE,{"disambiguationData":[TD([[makeQuery(id+"F13.imprint","IMPRINT",EDGE,{"derivedFrom":sQuery(id+"F13.wireOp",EDGE,"E166.bottom")}),-1.0]])]});
            var Q8;
            Q8=makeQuery(id+"F13.imprint","IMPRINT",FACE,{"disambiguationData":[TD([[makeQuery(id+"F13.imprint","IMPRINT",EDGE,{"derivedFrom":sQuery(id+"F13.wireOp",EDGE,"E190.bottom")}),-1.0]])]});
            var Q9;
            {var subQ0=sQuery(id+"F13.wireOp",EDGE,"E220.top");Q9=makeQuery(id+"F13.imprint","IMPRINT",FACE,{"disambiguationData":[TD([[makeQuery(id+"F13.imprint","IMPRINT",EDGE,{"derivedFrom":subQ0}),1.0]])]});}
            var Q10;
            {var subQ0=sQuery(id+"F13.wireOp",EDGE,"E221.top");Q10=makeQuery(id+"F13.imprint","IMPRINT",FACE,{"disambiguationData":[TD([[makeQuery(id+"F13.imprint","IMPRINT",EDGE,{"derivedFrom":subQ0}),1.0]])]});}
            var Q11;
            Q11=makeQuery(id+"F13.imprint","IMPRINT",FACE,{"disambiguationData":[TD([[makeQuery(id+"F13.imprint","IMPRINT",EDGE,{"derivedFrom":sQuery(id+"F13.wireOp",EDGE,"E197.bottom")}),-1.0]])]});
            var Q12;
            Q12=makeQuery(id+"F13.imprint","IMPRINT",FACE,{"disambiguationData":[TD([[makeQuery(id+"F13.imprint","IMPRINT",EDGE,{"derivedFrom":sQuery(id+"F13.wireOp",EDGE,"E188.bottom")}),-1.0]])]});
            var Q13;
            Q13=makeQuery(id+"F13.imprint","IMPRINT",FACE,{"disambiguationData":[TD([[makeQuery(id+"F13.imprint","IMPRINT",EDGE,{"derivedFrom":sQuery(id+"F13.wireOp",EDGE,"E177.bottom")}),-1.0]])]});
            var Q14;
            Q14=makeQuery(id+"F13.imprint","IMPRINT",FACE,{"disambiguationData":[TD([[makeQuery(id+"F13.imprint","IMPRINT",EDGE,{"derivedFrom":sQuery(id+"F13.wireOp",EDGE,"E164.bottom")}),-1.0]])]});
            var Q15;
            Q15=makeQuery(id+"F13.imprint","IMPRINT",FACE,{"disambiguationData":[TD([[makeQuery(id+"F13.imprint","IMPRINT",EDGE,{"derivedFrom":sQuery(id+"F13.wireOp",EDGE,"E165.top")}),-1.0]])]});
            var Q16;
            Q16=makeQuery(id+"F13.imprint","IMPRINT",FACE,{"disambiguationData":[TD([[makeQuery(id+"F13.imprint","IMPRINT",EDGE,{"derivedFrom":sQuery(id+"F13.wireOp",EDGE,"E163.top")}),-1.0]])]});
            var Q17;
            Q17=makeQuery(id+"F13.imprint","IMPRINT",FACE,{"disambiguationData":[TD([[makeQuery(id+"F13.imprint","IMPRINT",EDGE,{"derivedFrom":sQuery(id+"F13.wireOp",EDGE,"E162.bottom")}),-1.0]])]});
            var Q18;
            Q18=makeQuery(id+"F13.imprint","IMPRINT",FACE,{"disambiguationData":[TD([[makeQuery(id+"F13.imprint","IMPRINT",EDGE,{"derivedFrom":sQuery(id+"F13.wireOp",EDGE,"E161.top")}),-1.0]])]});
            var Q19;
            {var subQ0=sQuery(id+"F13.wireOp",EDGE,"E160.top");Q19=makeQuery(id+"F13.imprint","IMPRINT",FACE,{"disambiguationData":[TD([[makeQuery(id+"F13.imprint","IMPRINT",EDGE,{"derivedFrom":subQ0}),-1.0]])]});}
            var Q20;
            {var subQ0=sQuery(id+"F13.wireOp",EDGE,"E207.top");Q20=makeQuery(id+"F13.imprint","IMPRINT",FACE,{"disambiguationData":[TD([[makeQuery(id+"F13.imprint","IMPRINT",EDGE,{"derivedFrom":subQ0}),1.0]])]});}
            var Q21;
            Q21=makeQuery(id+"F13.imprint","IMPRINT",FACE,{"disambiguationData":[TD([[makeQuery(id+"F13.imprint","IMPRINT",EDGE,{"derivedFrom":sQuery(id+"F13.wireOp",EDGE,"E175.bottom")}),-1.0]])]});
            var Q22;
            {var subQ0=sQuery(id+"F13.wireOp",EDGE,"E208.top");Q22=makeQuery(id+"F13.imprint","IMPRINT",FACE,{"disambiguationData":[TD([[makeQuery(id+"F13.imprint","IMPRINT",EDGE,{"derivedFrom":subQ0}),1.0]])]});}
            var Q23;
            Q23=makeQuery(id+"F13.imprint","IMPRINT",FACE,{"disambiguationData":[TD([[makeQuery(id+"F13.imprint","IMPRINT",EDGE,{"derivedFrom":sQuery(id+"F13.wireOp",EDGE,"E186.bottom")}),-1.0]])]});
            var Q24;
            Q24=makeQuery(id+"F13.imprint","IMPRINT",FACE,{"disambiguationData":[TD([[makeQuery(id+"F13.imprint","IMPRINT",EDGE,{"derivedFrom":sQuery(id+"F13.wireOp",EDGE,"E209.top")}),1.0]])]});
            var Q25;
            Q25=makeQuery(id+"F13.imprint","IMPRINT",FACE,{"disambiguationData":[TD([[makeQuery(id+"F13.imprint","IMPRINT",EDGE,{"derivedFrom":sQuery(id+"F13.wireOp",EDGE,"E195.bottom")}),-1.0]])]});
            var Q26;
            Q26=makeQuery(id+"F13.imprint","IMPRINT",FACE,{"disambiguationData":[TD([[makeQuery(id+"F13.imprint","IMPRINT",EDGE,{"derivedFrom":sQuery(id+"F13.wireOp",EDGE,"E200.bottom")}),-1.0]])]});
            var Q27;
            Q27=makeQuery(id+"F13.imprint","IMPRINT",FACE,{"disambiguationData":[TD([[makeQuery(id+"F13.imprint","IMPRINT",EDGE,{"derivedFrom":sQuery(id+"F13.wireOp",EDGE,"E202.bottom")}),-1.0]])]});
            var Q28;
            {var subQ0=sQuery(id+"F13.wireOp",EDGE,"E215.top");Q28=makeQuery(id+"F13.imprint","IMPRINT",FACE,{"disambiguationData":[TD([[makeQuery(id+"F13.imprint","IMPRINT",EDGE,{"derivedFrom":subQ0}),-1.0]])]});}
            var Q29;
            Q29=makeQuery(id+"F13.imprint","IMPRINT",FACE,{"disambiguationData":[TD([[makeQuery(id+"F13.imprint","IMPRINT",EDGE,{"derivedFrom":sQuery(id+"F13.wireOp",EDGE,"E218.bottom")}),1.0]])]});
            var Q30;
            Q30=makeQuery(id+"F13.imprint","IMPRINT",FACE,{"disambiguationData":[TD([[makeQuery(id+"F13.imprint","IMPRINT",EDGE,{"derivedFrom":sQuery(id+"F13.wireOp",EDGE,"E205.bottom")}),-1.0]])]});
            var Q31;
            {var subQ0=sQuery(id+"F13.wireOp",EDGE,"E229.bottom");Q31=makeQuery(id+"F13.imprint","IMPRINT",FACE,{"disambiguationData":[TD([[makeQuery(id+"F13.imprint","IMPRINT",EDGE,{"derivedFrom":subQ0}),-1.0]])]});}
            extrude(context, id + "F14", {"entities" : qUnion([Q0, Q1, Q2, Q3, Q4, Q5, Q6, Q7, Q8, Q9, Q10, Q11, Q12, Q13, Q14, Q15, Q16, Q17, Q18, Q19, Q20, Q21, Q22, Q23, Q24, Q25, Q26, Q27, Q28, Q29, Q30, Q31]), "depth" : 0.35 * mm, "offsetDistance" : 25.4 * mm});
        }
        {
            var Q0;
            Q0=makeQuery(id+"F14.opExtrude","SWEPT_BODY",BODY,{"disambiguationData":[OSD([sQuery(id+"F13.wireOp",EDGE,"E218.bottom"),sQuery(id+"F13.wireOp",EDGE,"E217.left"),sQuery(id+"F13.wireOp",EDGE,"E218.left"),sQuery(id+"F13.wireOp",EDGE,"E218.top"),sQuery(id+"F13.wireOp",EDGE,"E230")])]});
            var Q1;
            Q1=makeQuery(id+"F14.opExtrude","SWEPT_BODY",BODY,{"disambiguationData":[OSD([sQuery(id+"F13.wireOp",EDGE,"E209.top"),sQuery(id+"F13.wireOp",EDGE,"E199.right"),sQuery(id+"F13.wireOp",EDGE,"E209.right"),sQuery(id+"F13.wireOp",EDGE,"E209.bottom"),sQuery(id+"F13.wireOp",EDGE,"E231")])]});
            var Q2;
            Q2=makeQuery(id+"F14.opExtrude","SWEPT_BODY",BODY,{"disambiguationData":[OSD([sQuery(id+"F13.wireOp",EDGE,"E200.bottom"),sQuery(id+"F13.wireOp",EDGE,"E210.right"),sQuery(id+"F13.wireOp",EDGE,"E210.top"),sQuery(id+"F13.wireOp",EDGE,"E225.left"),sQuery(id+"F13.wireOp",EDGE,"E231")])]});
            var Q3;
            Q3=makeQuery(id+"F14.opExtrude","SWEPT_BODY",BODY,{"disambiguationData":[OSD([sQuery(id+"F13.wireOp",EDGE,"E207.top"),sQuery(id+"F13.wireOp",EDGE,"E183.right"),sQuery(id+"F13.wireOp",EDGE,"E231")])]});
            var Q4;
            Q4=makeQuery(id+"F14.opExtrude","SWEPT_BODY",BODY,{"disambiguationData":[OSD([sQuery(id+"F13.wireOp",EDGE,"E160.top"),sQuery(id+"F13.wireOp",EDGE,"E172.right"),sQuery(id+"F13.wireOp",EDGE,"E231")])]});
            var Q5;
            Q5=makeQuery(id+"F14.opExtrude","SWEPT_BODY",BODY,{"disambiguationData":[OSD([sQuery(id+"F13.wireOp",EDGE,"E208.top"),sQuery(id+"F13.wireOp",EDGE,"E192.right"),sQuery(id+"F13.wireOp",EDGE,"E208.bottom"),sQuery(id+"F13.wireOp",EDGE,"E231")])]});
            var Q6;
            Q6=makeQuery(id+"F14.opExtrude","SWEPT_BODY",BODY,{"disambiguationData":[OSD([sQuery(id+"F13.wireOp",EDGE,"E202.bottom"),sQuery(id+"F13.wireOp",EDGE,"E205.right"),sQuery(id+"F13.wireOp",EDGE,"E212.right"),sQuery(id+"F13.wireOp",EDGE,"E206.bottom")])]});
            var Q7;
            Q7=makeQuery(id+"F14.opExtrude","SWEPT_BODY",BODY,{"disambiguationData":[OSD([sQuery(id+"F13.wireOp",EDGE,"E195.bottom"),sQuery(id+"F13.wireOp",EDGE,"E200.right"),sQuery(id+"F13.wireOp",EDGE,"E201.right"),sQuery(id+"F13.wireOp",EDGE,"E201.bottom")])]});
            var Q8;
            Q8=makeQuery(id+"F14.opExtrude","SWEPT_BODY",BODY,{"disambiguationData":[OSD([sQuery(id+"F13.wireOp",EDGE,"E197.bottom"),sQuery(id+"F13.wireOp",EDGE,"E202.right"),sQuery(id+"F13.wireOp",EDGE,"E212.bottom"),sQuery(id+"F13.wireOp",EDGE,"E221.right")])]});
            var Q9;
            Q9=makeQuery(id+"F14.opExtrude","SWEPT_BODY",BODY,{"disambiguationData":[OSD([sQuery(id+"F13.wireOp",EDGE,"E188.bottom"),sQuery(id+"F13.wireOp",EDGE,"E195.right"),sQuery(id+"F13.wireOp",EDGE,"E196.right"),sQuery(id+"F13.wireOp",EDGE,"E196.bottom")])]});
            var Q10;
            Q10=makeQuery(id+"F14.opExtrude","SWEPT_BODY",BODY,{"disambiguationData":[OSD([sQuery(id+"F13.wireOp",EDGE,"E186.bottom"),sQuery(id+"F13.wireOp",EDGE,"E193.right"),sQuery(id+"F13.wireOp",EDGE,"E194.right"),sQuery(id+"F13.wireOp",EDGE,"E194.bottom")])]});
            var Q11;
            Q11=makeQuery(id+"F14.opExtrude","SWEPT_BODY",BODY,{"disambiguationData":[OSD([sQuery(id+"F13.wireOp",EDGE,"E190.bottom"),sQuery(id+"F13.wireOp",EDGE,"E197.right"),sQuery(id+"F13.wireOp",EDGE,"E220.right"),sQuery(id+"F13.wireOp",EDGE,"E221.bottom")])]});
            var Q12;
            Q12=makeQuery(id+"F14.opExtrude","SWEPT_BODY",BODY,{"disambiguationData":[OSD([sQuery(id+"F13.wireOp",EDGE,"E179.bottom"),sQuery(id+"F13.wireOp",EDGE,"E188.right"),sQuery(id+"F13.wireOp",EDGE,"E189.right"),sQuery(id+"F13.wireOp",EDGE,"E189.bottom")])]});
            var Q13;
            Q13=makeQuery(id+"F14.opExtrude","SWEPT_BODY",BODY,{"disambiguationData":[OSD([sQuery(id+"F13.wireOp",EDGE,"E181.bottom"),sQuery(id+"F13.wireOp",EDGE,"E190.right"),sQuery(id+"F13.wireOp",EDGE,"E220.bottom"),sQuery(id+"F13.wireOp",EDGE,"E219.right"),sQuery(id+"F13.wireOp",EDGE,"E230")])]});
            var Q14;
            Q14=makeQuery(id+"F14.opExtrude","SWEPT_BODY",BODY,{"disambiguationData":[OSD([sQuery(id+"F13.wireOp",EDGE,"E175.bottom"),sQuery(id+"F13.wireOp",EDGE,"E184.right"),sQuery(id+"F13.wireOp",EDGE,"E185.right"),sQuery(id+"F13.wireOp",EDGE,"E185.bottom")])]});
            var Q15;
            Q15=makeQuery(id+"F14.opExtrude","SWEPT_BODY",BODY,{"disambiguationData":[OSD([sQuery(id+"F13.wireOp",EDGE,"E177.bottom"),sQuery(id+"F13.wireOp",EDGE,"E186.right"),sQuery(id+"F13.wireOp",EDGE,"E187.right"),sQuery(id+"F13.wireOp",EDGE,"E187.bottom")])]});
            var Q16;
            Q16=makeQuery(id+"F14.opExtrude","SWEPT_BODY",BODY,{"disambiguationData":[OSD([sQuery(id+"F13.wireOp",EDGE,"E170.bottom"),sQuery(id+"F13.wireOp",EDGE,"E181.right"),sQuery(id+"F13.wireOp",EDGE,"E219.bottom"),sQuery(id+"F13.wireOp",EDGE,"E223.right"),sQuery(id+"F13.wireOp",EDGE,"E230")])]});
            var Q17;
            Q17=makeQuery(id+"F14.opExtrude","SWEPT_BODY",BODY,{"disambiguationData":[OSD([sQuery(id+"F13.wireOp",EDGE,"E166.bottom"),sQuery(id+"F13.wireOp",EDGE,"E177.right"),sQuery(id+"F13.wireOp",EDGE,"E178.right"),sQuery(id+"F13.wireOp",EDGE,"E178.bottom")])]});
            var Q18;
            Q18=makeQuery(id+"F14.opExtrude","SWEPT_BODY",BODY,{"disambiguationData":[OSD([sQuery(id+"F13.wireOp",EDGE,"E168.bottom"),sQuery(id+"F13.wireOp",EDGE,"E179.right"),sQuery(id+"F13.wireOp",EDGE,"E180.right"),sQuery(id+"F13.wireOp",EDGE,"E180.bottom")])]});
            var Q19;
            Q19=makeQuery(id+"F14.opExtrude","SWEPT_BODY",BODY,{"disambiguationData":[OSD([sQuery(id+"F13.wireOp",EDGE,"E162.bottom"),sQuery(id+"F13.wireOp",EDGE,"E173.right"),sQuery(id+"F13.wireOp",EDGE,"E174.right"),sQuery(id+"F13.wireOp",EDGE,"E174.bottom")])]});
            var Q20;
            Q20=makeQuery(id+"F14.opExtrude","SWEPT_BODY",BODY,{"disambiguationData":[OSD([sQuery(id+"F13.wireOp",EDGE,"E164.bottom"),sQuery(id+"F13.wireOp",EDGE,"E175.right"),sQuery(id+"F13.wireOp",EDGE,"E176.right"),sQuery(id+"F13.wireOp",EDGE,"E176.bottom")])]});
            var Q21;
            Q21=makeQuery(id+"F14.opExtrude","SWEPT_BODY",BODY,{"disambiguationData":[OSD([sQuery(id+"F13.wireOp",EDGE,"E169.top"),sQuery(id+"F13.wireOp",EDGE,"E168.right"),sQuery(id+"F13.wireOp",EDGE,"E169.right"),sQuery(id+"F13.wireOp",EDGE,"E169.bottom")])]});
            var Q22;
            Q22=makeQuery(id+"F14.opExtrude","SWEPT_BODY",BODY,{"disambiguationData":[OSD([sQuery(id+"F13.wireOp",EDGE,"E167.top"),sQuery(id+"F13.wireOp",EDGE,"E166.right"),sQuery(id+"F13.wireOp",EDGE,"E167.right"),sQuery(id+"F13.wireOp",EDGE,"E167.bottom")])]});
            var Q23;
            Q23=makeQuery(id+"F14.opExtrude","SWEPT_BODY",BODY,{"disambiguationData":[OSD([sQuery(id+"F13.wireOp",EDGE,"E171.top"),sQuery(id+"F13.wireOp",EDGE,"E170.right"),sQuery(id+"F13.wireOp",EDGE,"E223.bottom"),sQuery(id+"F13.wireOp",EDGE,"E230")])]});
            var Q24;
            Q24=makeQuery(id+"F14.opExtrude","SWEPT_BODY",BODY,{"disambiguationData":[OSD([sQuery(id+"F13.wireOp",EDGE,"E163.top"),sQuery(id+"F13.wireOp",EDGE,"E162.right"),sQuery(id+"F13.wireOp",EDGE,"E163.right"),sQuery(id+"F13.wireOp",EDGE,"E163.bottom")])]});
            var Q25;
            Q25=makeQuery(id+"F14.opExtrude","SWEPT_BODY",BODY,{"disambiguationData":[OSD([sQuery(id+"F13.wireOp",EDGE,"E165.top"),sQuery(id+"F13.wireOp",EDGE,"E164.right"),sQuery(id+"F13.wireOp",EDGE,"E165.right"),sQuery(id+"F13.wireOp",EDGE,"E165.bottom")])]});
            var Q26;
            Q26=makeQuery(id+"FyfzPNdeHjCoWzU_0.opExtrude","SWEPT_BODY",BODY,{"disambiguationData":[OSD([sQuery(id+"F13.wireOp",EDGE,"E218.top"),sQuery(id+"F13.wireOp",EDGE,"E229.right"),sQuery(id+"F13.wireOp",EDGE,"E230")])]});
            var Q27;
            Q27=makeQuery(id+"FyfzPNdeHjCoWzU_0.opExtrude","SWEPT_BODY",BODY,{"disambiguationData":[OSD([sQuery(id+"F13.wireOp",EDGE,"E209.bottom"),sQuery(id+"F13.wireOp",EDGE,"E225.left"),sQuery(id+"F13.wireOp",EDGE,"E231")])]});
            var Q28;
            Q28=makeQuery(id+"F14.opExtrude","SWEPT_BODY",BODY,{"disambiguationData":[OSD([sQuery(id+"F13.wireOp",EDGE,"E205.bottom"),sQuery(id+"F13.wireOp",EDGE,"E213.left"),sQuery(id+"F13.wireOp",EDGE,"E213.right"),sQuery(id+"F13.wireOp",EDGE,"E217.bottom")])]});
            var Q29;
            Q29=makeQuery(id+"FyfzPNdeHjCoWzU_0.opExtrude","SWEPT_BODY",BODY,{"disambiguationData":[OSD([sQuery(id+"F13.wireOp",EDGE,"E208.bottom"),sQuery(id+"F13.wireOp",EDGE,"E209.right"),sQuery(id+"F13.wireOp",EDGE,"E231")])]});
            var Q30;
            Q30=makeQuery(id+"FyfzPNdeHjCoWzU_0.opExtrude","SWEPT_BODY",BODY,{"disambiguationData":[OSD([sQuery(id+"F13.wireOp",EDGE,"E223.bottom"),sQuery(id+"F13.wireOp",EDGE,"E223.right"),sQuery(id+"F13.wireOp",EDGE,"E230")])]});
            var Q31;
            Q31=makeQuery(id+"FyfzPNdeHjCoWzU_0.opExtrude","SWEPT_BODY",BODY,{"disambiguationData":[OSD([sQuery(id+"F13.wireOp",EDGE,"E221.bottom"),sQuery(id+"F13.wireOp",EDGE,"E221.right"),sQuery(id+"F13.wireOp",EDGE,"E221.left"),sQuery(id+"F13.wireOp",EDGE,"E221.top"),sQuery(id+"F13.wireOp",EDGE,"E230")])]});
            var Q32;
            Q32=makeQuery(id+"FyfzPNdeHjCoWzU_0.opExtrude","SWEPT_BODY",BODY,{"disambiguationData":[OSD([sQuery(id+"F13.wireOp",EDGE,"E220.bottom"),sQuery(id+"F13.wireOp",EDGE,"E220.right"),sQuery(id+"F13.wireOp",EDGE,"E220.top"),sQuery(id+"F13.wireOp",EDGE,"E230")])]});
            var Q33;
            Q33=makeQuery(id+"FyfzPNdeHjCoWzU_0.opExtrude","SWEPT_BODY",BODY,{"disambiguationData":[OSD([sQuery(id+"F13.wireOp",EDGE,"E219.bottom"),sQuery(id+"F13.wireOp",EDGE,"E219.right"),sQuery(id+"F13.wireOp",EDGE,"E230")])]});
            var Q34;
            Q34=makeQuery(id+"FyfzPNdeHjCoWzU_0.opExtrude","SWEPT_BODY",BODY,{"disambiguationData":[OSD([sQuery(id+"F13.wireOp",EDGE,"E206.bottom"),sQuery(id+"F13.wireOp",EDGE,"E213.right"),sQuery(id+"F13.wireOp",EDGE,"E218.bottom"),sQuery(id+"F13.wireOp",EDGE,"E214.right")])]});
            var Q35;
            Q35=makeQuery(id+"FyfzPNdeHjCoWzU_0.opExtrude","SWEPT_BODY",BODY,{"disambiguationData":[OSD([sQuery(id+"F13.wireOp",EDGE,"E217.bottom"),sQuery(id+"F13.wireOp",EDGE,"E217.left"),sQuery(id+"F13.wireOp",EDGE,"E216.right"),sQuery(id+"F13.wireOp",EDGE,"E229.bottom"),sQuery(id+"F13.wireOp",EDGE,"E231")])]});
            var Q36;
            Q36=makeQuery(id+"FyfzPNdeHjCoWzU_0.opExtrude","SWEPT_BODY",BODY,{"disambiguationData":[OSD([sQuery(id+"F13.wireOp",EDGE,"E210.top"),sQuery(id+"F13.wireOp",EDGE,"E213.left"),sQuery(id+"F13.wireOp",EDGE,"E228.bottom"),sQuery(id+"F13.wireOp",EDGE,"E231")])]});
            var Q37;
            Q37=makeQuery(id+"FyfzPNdeHjCoWzU_0.opExtrude","SWEPT_BODY",BODY,{"disambiguationData":[OSD([sQuery(id+"F13.wireOp",EDGE,"E212.bottom"),sQuery(id+"F13.wireOp",EDGE,"E212.right"),sQuery(id+"F13.wireOp",EDGE,"E222.right"),sQuery(id+"F13.wireOp",EDGE,"E215.top"),sQuery(id+"F13.wireOp",EDGE,"E230")])]});
            var Q38;
            Q38=makeQuery(id+"FyfzPNdeHjCoWzU_0.opExtrude","SWEPT_BODY",BODY,{"disambiguationData":[OSD([sQuery(id+"F13.wireOp",EDGE,"E201.bottom"),sQuery(id+"F13.wireOp",EDGE,"E205.right"),sQuery(id+"F13.wireOp",EDGE,"E210.right"),sQuery(id+"F13.wireOp",EDGE,"E205.bottom")])]});
            var Q39;
            Q39=makeQuery(id+"FyfzPNdeHjCoWzU_0.opExtrude","SWEPT_BODY",BODY,{"disambiguationData":[OSD([sQuery(id+"F13.wireOp",EDGE,"E194.bottom"),sQuery(id+"F13.wireOp",EDGE,"E200.right"),sQuery(id+"F13.wireOp",EDGE,"E199.right"),sQuery(id+"F13.wireOp",EDGE,"E200.bottom")])]});
            var Q40;
            Q40=makeQuery(id+"FyfzPNdeHjCoWzU_0.opExtrude","SWEPT_BODY",BODY,{"disambiguationData":[OSD([sQuery(id+"F13.wireOp",EDGE,"E196.bottom"),sQuery(id+"F13.wireOp",EDGE,"E201.right"),sQuery(id+"F13.wireOp",EDGE,"E202.right"),sQuery(id+"F13.wireOp",EDGE,"E202.bottom")])]});
            var Q41;
            Q41=makeQuery(id+"FyfzPNdeHjCoWzU_0.opExtrude","SWEPT_BODY",BODY,{"disambiguationData":[OSD([sQuery(id+"F13.wireOp",EDGE,"E189.bottom"),sQuery(id+"F13.wireOp",EDGE,"E196.right"),sQuery(id+"F13.wireOp",EDGE,"E197.right"),sQuery(id+"F13.wireOp",EDGE,"E197.bottom")])]});
            var Q42;
            Q42=makeQuery(id+"FyfzPNdeHjCoWzU_0.opExtrude","SWEPT_BODY",BODY,{"disambiguationData":[OSD([sQuery(id+"F13.wireOp",EDGE,"E185.bottom"),sQuery(id+"F13.wireOp",EDGE,"E193.right"),sQuery(id+"F13.wireOp",EDGE,"E192.right"),sQuery(id+"F13.wireOp",EDGE,"E209.top")])]});
            var Q43;
            Q43=makeQuery(id+"FyfzPNdeHjCoWzU_0.opExtrude","SWEPT_BODY",BODY,{"disambiguationData":[OSD([sQuery(id+"F13.wireOp",EDGE,"E187.bottom"),sQuery(id+"F13.wireOp",EDGE,"E194.right"),sQuery(id+"F13.wireOp",EDGE,"E195.right"),sQuery(id+"F13.wireOp",EDGE,"E195.bottom")])]});
            var Q44;
            Q44=makeQuery(id+"FyfzPNdeHjCoWzU_0.opExtrude","SWEPT_BODY",BODY,{"disambiguationData":[OSD([sQuery(id+"F13.wireOp",EDGE,"E180.bottom"),sQuery(id+"F13.wireOp",EDGE,"E189.right"),sQuery(id+"F13.wireOp",EDGE,"E190.right"),sQuery(id+"F13.wireOp",EDGE,"E190.bottom")])]});
            var Q45;
            Q45=makeQuery(id+"FyfzPNdeHjCoWzU_0.opExtrude","SWEPT_BODY",BODY,{"disambiguationData":[OSD([sQuery(id+"F13.wireOp",EDGE,"E178.bottom"),sQuery(id+"F13.wireOp",EDGE,"E187.right"),sQuery(id+"F13.wireOp",EDGE,"E188.right"),sQuery(id+"F13.wireOp",EDGE,"E188.bottom")])]});
            var Q46;
            Q46=makeQuery(id+"FyfzPNdeHjCoWzU_0.opExtrude","SWEPT_BODY",BODY,{"disambiguationData":[OSD([sQuery(id+"F13.wireOp",EDGE,"E176.bottom"),sQuery(id+"F13.wireOp",EDGE,"E185.right"),sQuery(id+"F13.wireOp",EDGE,"E186.right"),sQuery(id+"F13.wireOp",EDGE,"E186.bottom")])]});
            var Q47;
            Q47=makeQuery(id+"FyfzPNdeHjCoWzU_0.opExtrude","SWEPT_BODY",BODY,{"disambiguationData":[OSD([sQuery(id+"F13.wireOp",EDGE,"E174.bottom"),sQuery(id+"F13.wireOp",EDGE,"E184.right"),sQuery(id+"F13.wireOp",EDGE,"E183.right"),sQuery(id+"F13.wireOp",EDGE,"E208.top"),sQuery(id+"F13.wireOp",EDGE,"E231")])]});
            var Q48;
            Q48=makeQuery(id+"FyfzPNdeHjCoWzU_0.opExtrude","SWEPT_BODY",BODY,{"disambiguationData":[OSD([sQuery(id+"F13.wireOp",EDGE,"E167.bottom"),sQuery(id+"F13.wireOp",EDGE,"E178.right"),sQuery(id+"F13.wireOp",EDGE,"E179.right"),sQuery(id+"F13.wireOp",EDGE,"E179.bottom")])]});
            var Q49;
            Q49=makeQuery(id+"FyfzPNdeHjCoWzU_0.opExtrude","SWEPT_BODY",BODY,{"disambiguationData":[OSD([sQuery(id+"F13.wireOp",EDGE,"E169.bottom"),sQuery(id+"F13.wireOp",EDGE,"E180.right"),sQuery(id+"F13.wireOp",EDGE,"E181.right"),sQuery(id+"F13.wireOp",EDGE,"E181.bottom")])]});
            var Q50;
            Q50=makeQuery(id+"FyfzPNdeHjCoWzU_0.opExtrude","SWEPT_BODY",BODY,{"disambiguationData":[OSD([sQuery(id+"F13.wireOp",EDGE,"E165.bottom"),sQuery(id+"F13.wireOp",EDGE,"E176.right"),sQuery(id+"F13.wireOp",EDGE,"E177.right"),sQuery(id+"F13.wireOp",EDGE,"E177.bottom")])]});
            var Q51;
            Q51=makeQuery(id+"FyfzPNdeHjCoWzU_0.opExtrude","SWEPT_BODY",BODY,{"disambiguationData":[OSD([sQuery(id+"F13.wireOp",EDGE,"E163.bottom"),sQuery(id+"F13.wireOp",EDGE,"E174.right"),sQuery(id+"F13.wireOp",EDGE,"E175.right"),sQuery(id+"F13.wireOp",EDGE,"E175.bottom")])]});
            var Q52;
            Q52=makeQuery(id+"FyfzPNdeHjCoWzU_0.opExtrude","SWEPT_BODY",BODY,{"disambiguationData":[OSD([sQuery(id+"F13.wireOp",EDGE,"E168.top"),sQuery(id+"F13.wireOp",EDGE,"E167.right"),sQuery(id+"F13.wireOp",EDGE,"E168.right"),sQuery(id+"F13.wireOp",EDGE,"E168.bottom")])]});
            var Q53;
            Q53=makeQuery(id+"FyfzPNdeHjCoWzU_0.opExtrude","SWEPT_BODY",BODY,{"disambiguationData":[OSD([sQuery(id+"F13.wireOp",EDGE,"E170.top"),sQuery(id+"F13.wireOp",EDGE,"E169.right"),sQuery(id+"F13.wireOp",EDGE,"E170.right"),sQuery(id+"F13.wireOp",EDGE,"E170.bottom")])]});
            var Q54;
            Q54=makeQuery(id+"FyfzPNdeHjCoWzU_0.opExtrude","SWEPT_BODY",BODY,{"disambiguationData":[OSD([sQuery(id+"F13.wireOp",EDGE,"E166.top"),sQuery(id+"F13.wireOp",EDGE,"E165.right"),sQuery(id+"F13.wireOp",EDGE,"E166.right"),sQuery(id+"F13.wireOp",EDGE,"E166.bottom")])]});
            var Q55;
            Q55=makeQuery(id+"FyfzPNdeHjCoWzU_0.opExtrude","SWEPT_BODY",BODY,{"disambiguationData":[OSD([sQuery(id+"F13.wireOp",EDGE,"E164.top"),sQuery(id+"F13.wireOp",EDGE,"E163.right"),sQuery(id+"F13.wireOp",EDGE,"E164.right"),sQuery(id+"F13.wireOp",EDGE,"E164.bottom")])]});
            var Q56;
            Q56=makeQuery(id+"FyfzPNdeHjCoWzU_0.opExtrude","SWEPT_BODY",BODY,{"disambiguationData":[OSD([sQuery(id+"F13.wireOp",EDGE,"E160.bottom"),sQuery(id+"F13.wireOp",EDGE,"E161.left"),sQuery(id+"F13.wireOp",EDGE,"E161.bottom"),sQuery(id+"F13.wireOp",EDGE,"E173.right"),sQuery(id+"F13.wireOp",EDGE,"E160.top"),sQuery(id+"F13.wireOp",EDGE,"E172.right"),sQuery(id+"F13.wireOp",EDGE,"E207.top"),sQuery(id+"F13.wireOp",EDGE,"E231")])]});
            var Q57;
            Q57=makeQuery(id+"FyfzPNdeHjCoWzU_0.opExtrude","SWEPT_BODY",BODY,{"disambiguationData":[OSD([sQuery(id+"F13.wireOp",EDGE,"E162.top"),sQuery(id+"F13.wireOp",EDGE,"E161.right"),sQuery(id+"F13.wireOp",EDGE,"E162.right"),sQuery(id+"F13.wireOp",EDGE,"E162.bottom")])]});
            var Q58;
            Q58=makeQuery(id+"F14.opExtrude","SWEPT_BODY",BODY,{"disambiguationData":[OSD([sQuery(id+"F13.wireOp",EDGE,"E161.top"),sQuery(id+"F13.wireOp",EDGE,"E161.left"),sQuery(id+"F13.wireOp",EDGE,"E161.right"),sQuery(id+"F13.wireOp",EDGE,"E161.bottom")])]});
            var Q59;
            Q59=makeQuery(id+"F14.opExtrude","SWEPT_BODY",BODY,{"disambiguationData":[OSD([sQuery(id+"F13.wireOp",EDGE,"E215.top"),sQuery(id+"F13.wireOp",EDGE,"E214.right"),sQuery(id+"F13.wireOp",EDGE,"E227.bottom"),sQuery(id+"F13.wireOp",EDGE,"E230")])]});
            var Q60;
            Q60=makeQuery(id+"F14.opExtrude","SWEPT_BODY",BODY,{"disambiguationData":[OSD([sQuery(id+"F13.wireOp",EDGE,"E220.top"),sQuery(id+"F13.wireOp",EDGE,"E221.left"),sQuery(id+"F13.wireOp",EDGE,"E230")])]});
            var Q61;
            Q61=makeQuery(id+"F14.opExtrude","SWEPT_BODY",BODY,{"disambiguationData":[OSD([sQuery(id+"F13.wireOp",EDGE,"E221.top"),sQuery(id+"F13.wireOp",EDGE,"E222.right"),sQuery(id+"F13.wireOp",EDGE,"E230")])]});
            var Q62;
            Q62=makeQuery(id+"F14.opExtrude","SWEPT_BODY",BODY,{"disambiguationData":[OSD([sQuery(id+"F13.wireOp",EDGE,"E229.bottom"),sQuery(id+"F13.wireOp",EDGE,"E229.right"),sQuery(id+"F13.wireOp",EDGE,"E231")])]});
            var Q63;
            Q63=makeQuery(id+"FyfzPNdeHjCoWzU_0.opExtrude","SWEPT_BODY",BODY,{"disambiguationData":[OSD([sQuery(id+"F13.wireOp",EDGE,"E227.bottom"),sQuery(id+"F13.wireOp",EDGE,"E218.left"),sQuery(id+"F13.wireOp",EDGE,"E230")])]});
            var Q64;
            Q64=qCreatedBy(makeId("Front.planeOp"),FACE);
            transform(context, id + "F15", {"entities" : qUnion([Q0, Q1, Q2, Q3, Q4, Q5, Q6, Q7, Q8, Q9, Q10, Q11, Q12, Q13, Q14, Q15, Q16, Q17, Q18, Q19, Q20, Q21, Q22, Q23, Q24, Q25, Q26, Q27, Q28, Q29, Q30, Q31, Q32, Q33, Q34, Q35, Q36, Q37, Q38, Q39, Q40, Q41, Q42, Q43, Q44, Q45, Q46, Q47, Q48, Q49, Q50, Q51, Q52, Q53, Q54, Q55, Q56, Q57, Q58, Q59, Q60, Q61, Q62, Q63]), "transformType" : TransformType.TRANSLATION_DISTANCE, "transformDirection" : qUnion([Q64]), "distance" : 12.35 * mm, "oppositeDirection" : true, "makeCopy" : false});
        }
        {
            var Q0;
            Q0=makeQuery(id+"FyfzPNdeHjCoWzU_0.opExtrude","SWEPT_BODY",BODY,{"disambiguationData":[OSD([sQuery(id+"F13.wireOp",EDGE,"E221.bottom"),sQuery(id+"F13.wireOp",EDGE,"E221.right"),sQuery(id+"F13.wireOp",EDGE,"E221.left"),sQuery(id+"F13.wireOp",EDGE,"E221.top"),sQuery(id+"F13.wireOp",EDGE,"E230")])]});
            var Q1;
            Q1=makeQuery(id+"F14.opExtrude","SWEPT_BODY",BODY,{"disambiguationData":[OSD([sQuery(id+"F13.wireOp",EDGE,"E205.bottom"),sQuery(id+"F13.wireOp",EDGE,"E213.left"),sQuery(id+"F13.wireOp",EDGE,"E213.right"),sQuery(id+"F13.wireOp",EDGE,"E217.bottom")])]});
            var Q2;
            Q2=makeQuery(id+"F14.opExtrude","SWEPT_BODY",BODY,{"disambiguationData":[OSD([sQuery(id+"F13.wireOp",EDGE,"E200.bottom"),sQuery(id+"F13.wireOp",EDGE,"E210.right"),sQuery(id+"F13.wireOp",EDGE,"E210.top"),sQuery(id+"F13.wireOp",EDGE,"E225.left"),sQuery(id+"F13.wireOp",EDGE,"E231")])]});
            var Q3;
            Q3=makeQuery(id+"F14.opExtrude","SWEPT_BODY",BODY,{"disambiguationData":[OSD([sQuery(id+"F13.wireOp",EDGE,"E209.top"),sQuery(id+"F13.wireOp",EDGE,"E199.right"),sQuery(id+"F13.wireOp",EDGE,"E209.right"),sQuery(id+"F13.wireOp",EDGE,"E209.bottom"),sQuery(id+"F13.wireOp",EDGE,"E231")])]});
            var Q4;
            Q4=makeQuery(id+"F14.opExtrude","SWEPT_BODY",BODY,{"disambiguationData":[OSD([sQuery(id+"F13.wireOp",EDGE,"E208.top"),sQuery(id+"F13.wireOp",EDGE,"E192.right"),sQuery(id+"F13.wireOp",EDGE,"E208.bottom"),sQuery(id+"F13.wireOp",EDGE,"E231")])]});
            var Q5;
            Q5=makeQuery(id+"F14.opExtrude","SWEPT_BODY",BODY,{"disambiguationData":[OSD([sQuery(id+"F13.wireOp",EDGE,"E207.top"),sQuery(id+"F13.wireOp",EDGE,"E183.right"),sQuery(id+"F13.wireOp",EDGE,"E231")])]});
            var Q6;
            Q6=makeQuery(id+"F14.opExtrude","SWEPT_BODY",BODY,{"disambiguationData":[OSD([sQuery(id+"F13.wireOp",EDGE,"E160.top"),sQuery(id+"F13.wireOp",EDGE,"E172.right"),sQuery(id+"F13.wireOp",EDGE,"E231")])]});
            var Q7;
            Q7=makeQuery(id+"F14.opExtrude","SWEPT_BODY",BODY,{"disambiguationData":[OSD([sQuery(id+"F13.wireOp",EDGE,"E161.top"),sQuery(id+"F13.wireOp",EDGE,"E161.left"),sQuery(id+"F13.wireOp",EDGE,"E161.right"),sQuery(id+"F13.wireOp",EDGE,"E161.bottom")])]});
            var Q8;
            Q8=makeQuery(id+"FyfzPNdeHjCoWzU_0.opExtrude","SWEPT_BODY",BODY,{"disambiguationData":[OSD([sQuery(id+"F13.wireOp",EDGE,"E218.top"),sQuery(id+"F13.wireOp",EDGE,"E229.right"),sQuery(id+"F13.wireOp",EDGE,"E230")])]});
            var Q9;
            Q9=makeQuery(id+"FyfzPNdeHjCoWzU_0.opExtrude","SWEPT_BODY",BODY,{"disambiguationData":[OSD([sQuery(id+"F13.wireOp",EDGE,"E209.bottom"),sQuery(id+"F13.wireOp",EDGE,"E225.left"),sQuery(id+"F13.wireOp",EDGE,"E231")])]});
            var Q10;
            Q10=makeQuery(id+"FyfzPNdeHjCoWzU_0.opExtrude","SWEPT_BODY",BODY,{"disambiguationData":[OSD([sQuery(id+"F13.wireOp",EDGE,"E208.bottom"),sQuery(id+"F13.wireOp",EDGE,"E209.right"),sQuery(id+"F13.wireOp",EDGE,"E231")])]});
            var Q11;
            Q11=makeQuery(id+"FyfzPNdeHjCoWzU_0.opExtrude","SWEPT_BODY",BODY,{"disambiguationData":[OSD([sQuery(id+"F13.wireOp",EDGE,"E227.bottom"),sQuery(id+"F13.wireOp",EDGE,"E218.left"),sQuery(id+"F13.wireOp",EDGE,"E230")])]});
            var Q12;
            Q12=makeQuery(id+"FyfzPNdeHjCoWzU_0.opExtrude","SWEPT_BODY",BODY,{"disambiguationData":[OSD([sQuery(id+"F13.wireOp",EDGE,"E223.bottom"),sQuery(id+"F13.wireOp",EDGE,"E223.right"),sQuery(id+"F13.wireOp",EDGE,"E230")])]});
            var Q13;
            Q13=makeQuery(id+"FyfzPNdeHjCoWzU_0.opExtrude","SWEPT_BODY",BODY,{"disambiguationData":[OSD([sQuery(id+"F13.wireOp",EDGE,"E160.bottom"),sQuery(id+"F13.wireOp",EDGE,"E161.left"),sQuery(id+"F13.wireOp",EDGE,"E161.bottom"),sQuery(id+"F13.wireOp",EDGE,"E173.right"),sQuery(id+"F13.wireOp",EDGE,"E160.top"),sQuery(id+"F13.wireOp",EDGE,"E172.right"),sQuery(id+"F13.wireOp",EDGE,"E207.top"),sQuery(id+"F13.wireOp",EDGE,"E231")])]});
            var Q14;
            Q14=makeQuery(id+"FyfzPNdeHjCoWzU_0.opExtrude","SWEPT_BODY",BODY,{"disambiguationData":[OSD([sQuery(id+"F13.wireOp",EDGE,"E162.top"),sQuery(id+"F13.wireOp",EDGE,"E161.right"),sQuery(id+"F13.wireOp",EDGE,"E162.right"),sQuery(id+"F13.wireOp",EDGE,"E162.bottom")])]});
            var Q15;
            Q15=makeQuery(id+"FyfzPNdeHjCoWzU_0.opExtrude","SWEPT_BODY",BODY,{"disambiguationData":[OSD([sQuery(id+"F13.wireOp",EDGE,"E164.top"),sQuery(id+"F13.wireOp",EDGE,"E163.right"),sQuery(id+"F13.wireOp",EDGE,"E164.right"),sQuery(id+"F13.wireOp",EDGE,"E164.bottom")])]});
            var Q16;
            Q16=makeQuery(id+"FyfzPNdeHjCoWzU_0.opExtrude","SWEPT_BODY",BODY,{"disambiguationData":[OSD([sQuery(id+"F13.wireOp",EDGE,"E166.top"),sQuery(id+"F13.wireOp",EDGE,"E165.right"),sQuery(id+"F13.wireOp",EDGE,"E166.right"),sQuery(id+"F13.wireOp",EDGE,"E166.bottom")])]});
            var Q17;
            Q17=makeQuery(id+"FyfzPNdeHjCoWzU_0.opExtrude","SWEPT_BODY",BODY,{"disambiguationData":[OSD([sQuery(id+"F13.wireOp",EDGE,"E168.top"),sQuery(id+"F13.wireOp",EDGE,"E167.right"),sQuery(id+"F13.wireOp",EDGE,"E168.right"),sQuery(id+"F13.wireOp",EDGE,"E168.bottom")])]});
            var Q18;
            Q18=makeQuery(id+"FyfzPNdeHjCoWzU_0.opExtrude","SWEPT_BODY",BODY,{"disambiguationData":[OSD([sQuery(id+"F13.wireOp",EDGE,"E170.top"),sQuery(id+"F13.wireOp",EDGE,"E169.right"),sQuery(id+"F13.wireOp",EDGE,"E170.right"),sQuery(id+"F13.wireOp",EDGE,"E170.bottom")])]});
            var Q19;
            Q19=makeQuery(id+"FyfzPNdeHjCoWzU_0.opExtrude","SWEPT_BODY",BODY,{"disambiguationData":[OSD([sQuery(id+"F13.wireOp",EDGE,"E163.bottom"),sQuery(id+"F13.wireOp",EDGE,"E174.right"),sQuery(id+"F13.wireOp",EDGE,"E175.right"),sQuery(id+"F13.wireOp",EDGE,"E175.bottom")])]});
            var Q20;
            Q20=makeQuery(id+"FyfzPNdeHjCoWzU_0.opExtrude","SWEPT_BODY",BODY,{"disambiguationData":[OSD([sQuery(id+"F13.wireOp",EDGE,"E165.bottom"),sQuery(id+"F13.wireOp",EDGE,"E176.right"),sQuery(id+"F13.wireOp",EDGE,"E177.right"),sQuery(id+"F13.wireOp",EDGE,"E177.bottom")])]});
            var Q21;
            Q21=makeQuery(id+"FyfzPNdeHjCoWzU_0.opExtrude","SWEPT_BODY",BODY,{"disambiguationData":[OSD([sQuery(id+"F13.wireOp",EDGE,"E167.bottom"),sQuery(id+"F13.wireOp",EDGE,"E178.right"),sQuery(id+"F13.wireOp",EDGE,"E179.right"),sQuery(id+"F13.wireOp",EDGE,"E179.bottom")])]});
            var Q22;
            Q22=makeQuery(id+"FyfzPNdeHjCoWzU_0.opExtrude","SWEPT_BODY",BODY,{"disambiguationData":[OSD([sQuery(id+"F13.wireOp",EDGE,"E169.bottom"),sQuery(id+"F13.wireOp",EDGE,"E180.right"),sQuery(id+"F13.wireOp",EDGE,"E181.right"),sQuery(id+"F13.wireOp",EDGE,"E181.bottom")])]});
            var Q23;
            Q23=makeQuery(id+"FyfzPNdeHjCoWzU_0.opExtrude","SWEPT_BODY",BODY,{"disambiguationData":[OSD([sQuery(id+"F13.wireOp",EDGE,"E174.bottom"),sQuery(id+"F13.wireOp",EDGE,"E184.right"),sQuery(id+"F13.wireOp",EDGE,"E183.right"),sQuery(id+"F13.wireOp",EDGE,"E208.top"),sQuery(id+"F13.wireOp",EDGE,"E231")])]});
            var Q24;
            Q24=makeQuery(id+"FyfzPNdeHjCoWzU_0.opExtrude","SWEPT_BODY",BODY,{"disambiguationData":[OSD([sQuery(id+"F13.wireOp",EDGE,"E176.bottom"),sQuery(id+"F13.wireOp",EDGE,"E185.right"),sQuery(id+"F13.wireOp",EDGE,"E186.right"),sQuery(id+"F13.wireOp",EDGE,"E186.bottom")])]});
            var Q25;
            Q25=makeQuery(id+"FyfzPNdeHjCoWzU_0.opExtrude","SWEPT_BODY",BODY,{"disambiguationData":[OSD([sQuery(id+"F13.wireOp",EDGE,"E178.bottom"),sQuery(id+"F13.wireOp",EDGE,"E187.right"),sQuery(id+"F13.wireOp",EDGE,"E188.right"),sQuery(id+"F13.wireOp",EDGE,"E188.bottom")])]});
            var Q26;
            Q26=makeQuery(id+"FyfzPNdeHjCoWzU_0.opExtrude","SWEPT_BODY",BODY,{"disambiguationData":[OSD([sQuery(id+"F13.wireOp",EDGE,"E180.bottom"),sQuery(id+"F13.wireOp",EDGE,"E189.right"),sQuery(id+"F13.wireOp",EDGE,"E190.right"),sQuery(id+"F13.wireOp",EDGE,"E190.bottom")])]});
            var Q27;
            Q27=makeQuery(id+"FyfzPNdeHjCoWzU_0.opExtrude","SWEPT_BODY",BODY,{"disambiguationData":[OSD([sQuery(id+"F13.wireOp",EDGE,"E185.bottom"),sQuery(id+"F13.wireOp",EDGE,"E193.right"),sQuery(id+"F13.wireOp",EDGE,"E192.right"),sQuery(id+"F13.wireOp",EDGE,"E209.top")])]});
            var Q28;
            Q28=makeQuery(id+"FyfzPNdeHjCoWzU_0.opExtrude","SWEPT_BODY",BODY,{"disambiguationData":[OSD([sQuery(id+"F13.wireOp",EDGE,"E187.bottom"),sQuery(id+"F13.wireOp",EDGE,"E194.right"),sQuery(id+"F13.wireOp",EDGE,"E195.right"),sQuery(id+"F13.wireOp",EDGE,"E195.bottom")])]});
            var Q29;
            Q29=makeQuery(id+"FyfzPNdeHjCoWzU_0.opExtrude","SWEPT_BODY",BODY,{"disambiguationData":[OSD([sQuery(id+"F13.wireOp",EDGE,"E189.bottom"),sQuery(id+"F13.wireOp",EDGE,"E196.right"),sQuery(id+"F13.wireOp",EDGE,"E197.right"),sQuery(id+"F13.wireOp",EDGE,"E197.bottom")])]});
            var Q30;
            Q30=makeQuery(id+"FyfzPNdeHjCoWzU_0.opExtrude","SWEPT_BODY",BODY,{"disambiguationData":[OSD([sQuery(id+"F13.wireOp",EDGE,"E194.bottom"),sQuery(id+"F13.wireOp",EDGE,"E200.right"),sQuery(id+"F13.wireOp",EDGE,"E199.right"),sQuery(id+"F13.wireOp",EDGE,"E200.bottom")])]});
            var Q31;
            Q31=makeQuery(id+"FyfzPNdeHjCoWzU_0.opExtrude","SWEPT_BODY",BODY,{"disambiguationData":[OSD([sQuery(id+"F13.wireOp",EDGE,"E196.bottom"),sQuery(id+"F13.wireOp",EDGE,"E201.right"),sQuery(id+"F13.wireOp",EDGE,"E202.right"),sQuery(id+"F13.wireOp",EDGE,"E202.bottom")])]});
            var Q32;
            Q32=makeQuery(id+"FyfzPNdeHjCoWzU_0.opExtrude","SWEPT_BODY",BODY,{"disambiguationData":[OSD([sQuery(id+"F13.wireOp",EDGE,"E201.bottom"),sQuery(id+"F13.wireOp",EDGE,"E205.right"),sQuery(id+"F13.wireOp",EDGE,"E210.right"),sQuery(id+"F13.wireOp",EDGE,"E205.bottom")])]});
            var Q33;
            Q33=makeQuery(id+"FyfzPNdeHjCoWzU_0.opExtrude","SWEPT_BODY",BODY,{"disambiguationData":[OSD([sQuery(id+"F13.wireOp",EDGE,"E210.top"),sQuery(id+"F13.wireOp",EDGE,"E213.left"),sQuery(id+"F13.wireOp",EDGE,"E228.bottom"),sQuery(id+"F13.wireOp",EDGE,"E231")])]});
            var Q34;
            Q34=makeQuery(id+"FyfzPNdeHjCoWzU_0.opExtrude","SWEPT_BODY",BODY,{"disambiguationData":[OSD([sQuery(id+"F13.wireOp",EDGE,"E212.bottom"),sQuery(id+"F13.wireOp",EDGE,"E212.right"),sQuery(id+"F13.wireOp",EDGE,"E222.right"),sQuery(id+"F13.wireOp",EDGE,"E215.top"),sQuery(id+"F13.wireOp",EDGE,"E230")])]});
            var Q35;
            Q35=makeQuery(id+"FyfzPNdeHjCoWzU_0.opExtrude","SWEPT_BODY",BODY,{"disambiguationData":[OSD([sQuery(id+"F13.wireOp",EDGE,"E206.bottom"),sQuery(id+"F13.wireOp",EDGE,"E213.right"),sQuery(id+"F13.wireOp",EDGE,"E218.bottom"),sQuery(id+"F13.wireOp",EDGE,"E214.right")])]});
            var Q36;
            Q36=makeQuery(id+"FyfzPNdeHjCoWzU_0.opExtrude","SWEPT_BODY",BODY,{"disambiguationData":[OSD([sQuery(id+"F13.wireOp",EDGE,"E217.bottom"),sQuery(id+"F13.wireOp",EDGE,"E217.left"),sQuery(id+"F13.wireOp",EDGE,"E216.right"),sQuery(id+"F13.wireOp",EDGE,"E229.bottom"),sQuery(id+"F13.wireOp",EDGE,"E231")])]});
            var Q37;
            Q37=makeQuery(id+"FyfzPNdeHjCoWzU_0.opExtrude","SWEPT_BODY",BODY,{"disambiguationData":[OSD([sQuery(id+"F13.wireOp",EDGE,"E219.bottom"),sQuery(id+"F13.wireOp",EDGE,"E219.right"),sQuery(id+"F13.wireOp",EDGE,"E230")])]});
            var Q38;
            Q38=makeQuery(id+"FyfzPNdeHjCoWzU_0.opExtrude","SWEPT_BODY",BODY,{"disambiguationData":[OSD([sQuery(id+"F13.wireOp",EDGE,"E220.bottom"),sQuery(id+"F13.wireOp",EDGE,"E220.right"),sQuery(id+"F13.wireOp",EDGE,"E220.top"),sQuery(id+"F13.wireOp",EDGE,"E230")])]});
            var Q39;
            Q39=makeQuery(id+"F14.opExtrude","SWEPT_BODY",BODY,{"disambiguationData":[OSD([sQuery(id+"F13.wireOp",EDGE,"E218.bottom"),sQuery(id+"F13.wireOp",EDGE,"E217.left"),sQuery(id+"F13.wireOp",EDGE,"E218.left"),sQuery(id+"F13.wireOp",EDGE,"E218.top"),sQuery(id+"F13.wireOp",EDGE,"E230")])]});
            var Q40;
            Q40=makeQuery(id+"F14.opExtrude","SWEPT_BODY",BODY,{"disambiguationData":[OSD([sQuery(id+"F13.wireOp",EDGE,"E229.bottom"),sQuery(id+"F13.wireOp",EDGE,"E229.right"),sQuery(id+"F13.wireOp",EDGE,"E231")])]});
            var Q41;
            Q41=makeQuery(id+"F14.opExtrude","SWEPT_BODY",BODY,{"disambiguationData":[OSD([sQuery(id+"F13.wireOp",EDGE,"E202.bottom"),sQuery(id+"F13.wireOp",EDGE,"E205.right"),sQuery(id+"F13.wireOp",EDGE,"E212.right"),sQuery(id+"F13.wireOp",EDGE,"E206.bottom")])]});
            var Q42;
            Q42=makeQuery(id+"F14.opExtrude","SWEPT_BODY",BODY,{"disambiguationData":[OSD([sQuery(id+"F13.wireOp",EDGE,"E197.bottom"),sQuery(id+"F13.wireOp",EDGE,"E202.right"),sQuery(id+"F13.wireOp",EDGE,"E212.bottom"),sQuery(id+"F13.wireOp",EDGE,"E221.right")])]});
            var Q43;
            Q43=makeQuery(id+"F14.opExtrude","SWEPT_BODY",BODY,{"disambiguationData":[OSD([sQuery(id+"F13.wireOp",EDGE,"E195.bottom"),sQuery(id+"F13.wireOp",EDGE,"E200.right"),sQuery(id+"F13.wireOp",EDGE,"E201.right"),sQuery(id+"F13.wireOp",EDGE,"E201.bottom")])]});
            var Q44;
            Q44=makeQuery(id+"F14.opExtrude","SWEPT_BODY",BODY,{"disambiguationData":[OSD([sQuery(id+"F13.wireOp",EDGE,"E190.bottom"),sQuery(id+"F13.wireOp",EDGE,"E197.right"),sQuery(id+"F13.wireOp",EDGE,"E220.right"),sQuery(id+"F13.wireOp",EDGE,"E221.bottom")])]});
            var Q45;
            Q45=makeQuery(id+"F14.opExtrude","SWEPT_BODY",BODY,{"disambiguationData":[OSD([sQuery(id+"F13.wireOp",EDGE,"E188.bottom"),sQuery(id+"F13.wireOp",EDGE,"E195.right"),sQuery(id+"F13.wireOp",EDGE,"E196.right"),sQuery(id+"F13.wireOp",EDGE,"E196.bottom")])]});
            var Q46;
            Q46=makeQuery(id+"F14.opExtrude","SWEPT_BODY",BODY,{"disambiguationData":[OSD([sQuery(id+"F13.wireOp",EDGE,"E186.bottom"),sQuery(id+"F13.wireOp",EDGE,"E193.right"),sQuery(id+"F13.wireOp",EDGE,"E194.right"),sQuery(id+"F13.wireOp",EDGE,"E194.bottom")])]});
            var Q47;
            Q47=makeQuery(id+"F14.opExtrude","SWEPT_BODY",BODY,{"disambiguationData":[OSD([sQuery(id+"F13.wireOp",EDGE,"E181.bottom"),sQuery(id+"F13.wireOp",EDGE,"E190.right"),sQuery(id+"F13.wireOp",EDGE,"E220.bottom"),sQuery(id+"F13.wireOp",EDGE,"E219.right"),sQuery(id+"F13.wireOp",EDGE,"E230")])]});
            var Q48;
            Q48=makeQuery(id+"F14.opExtrude","SWEPT_BODY",BODY,{"disambiguationData":[OSD([sQuery(id+"F13.wireOp",EDGE,"E179.bottom"),sQuery(id+"F13.wireOp",EDGE,"E188.right"),sQuery(id+"F13.wireOp",EDGE,"E189.right"),sQuery(id+"F13.wireOp",EDGE,"E189.bottom")])]});
            var Q49;
            Q49=makeQuery(id+"F14.opExtrude","SWEPT_BODY",BODY,{"disambiguationData":[OSD([sQuery(id+"F13.wireOp",EDGE,"E177.bottom"),sQuery(id+"F13.wireOp",EDGE,"E186.right"),sQuery(id+"F13.wireOp",EDGE,"E187.right"),sQuery(id+"F13.wireOp",EDGE,"E187.bottom")])]});
            var Q50;
            Q50=makeQuery(id+"F14.opExtrude","SWEPT_BODY",BODY,{"disambiguationData":[OSD([sQuery(id+"F13.wireOp",EDGE,"E175.bottom"),sQuery(id+"F13.wireOp",EDGE,"E184.right"),sQuery(id+"F13.wireOp",EDGE,"E185.right"),sQuery(id+"F13.wireOp",EDGE,"E185.bottom")])]});
            var Q51;
            Q51=makeQuery(id+"F14.opExtrude","SWEPT_BODY",BODY,{"disambiguationData":[OSD([sQuery(id+"F13.wireOp",EDGE,"E170.bottom"),sQuery(id+"F13.wireOp",EDGE,"E181.right"),sQuery(id+"F13.wireOp",EDGE,"E219.bottom"),sQuery(id+"F13.wireOp",EDGE,"E223.right"),sQuery(id+"F13.wireOp",EDGE,"E230")])]});
            var Q52;
            Q52=makeQuery(id+"F14.opExtrude","SWEPT_BODY",BODY,{"disambiguationData":[OSD([sQuery(id+"F13.wireOp",EDGE,"E168.bottom"),sQuery(id+"F13.wireOp",EDGE,"E179.right"),sQuery(id+"F13.wireOp",EDGE,"E180.right"),sQuery(id+"F13.wireOp",EDGE,"E180.bottom")])]});
            var Q53;
            Q53=makeQuery(id+"F14.opExtrude","SWEPT_BODY",BODY,{"disambiguationData":[OSD([sQuery(id+"F13.wireOp",EDGE,"E166.bottom"),sQuery(id+"F13.wireOp",EDGE,"E177.right"),sQuery(id+"F13.wireOp",EDGE,"E178.right"),sQuery(id+"F13.wireOp",EDGE,"E178.bottom")])]});
            var Q54;
            Q54=makeQuery(id+"F14.opExtrude","SWEPT_BODY",BODY,{"disambiguationData":[OSD([sQuery(id+"F13.wireOp",EDGE,"E164.bottom"),sQuery(id+"F13.wireOp",EDGE,"E175.right"),sQuery(id+"F13.wireOp",EDGE,"E176.right"),sQuery(id+"F13.wireOp",EDGE,"E176.bottom")])]});
            var Q55;
            Q55=makeQuery(id+"F14.opExtrude","SWEPT_BODY",BODY,{"disambiguationData":[OSD([sQuery(id+"F13.wireOp",EDGE,"E162.bottom"),sQuery(id+"F13.wireOp",EDGE,"E173.right"),sQuery(id+"F13.wireOp",EDGE,"E174.right"),sQuery(id+"F13.wireOp",EDGE,"E174.bottom")])]});
            var Q56;
            Q56=makeQuery(id+"F14.opExtrude","SWEPT_BODY",BODY,{"disambiguationData":[OSD([sQuery(id+"F13.wireOp",EDGE,"E171.top"),sQuery(id+"F13.wireOp",EDGE,"E170.right"),sQuery(id+"F13.wireOp",EDGE,"E223.bottom"),sQuery(id+"F13.wireOp",EDGE,"E230")])]});
            var Q57;
            Q57=makeQuery(id+"F14.opExtrude","SWEPT_BODY",BODY,{"disambiguationData":[OSD([sQuery(id+"F13.wireOp",EDGE,"E169.top"),sQuery(id+"F13.wireOp",EDGE,"E168.right"),sQuery(id+"F13.wireOp",EDGE,"E169.right"),sQuery(id+"F13.wireOp",EDGE,"E169.bottom")])]});
            var Q58;
            Q58=makeQuery(id+"F14.opExtrude","SWEPT_BODY",BODY,{"disambiguationData":[OSD([sQuery(id+"F13.wireOp",EDGE,"E167.top"),sQuery(id+"F13.wireOp",EDGE,"E166.right"),sQuery(id+"F13.wireOp",EDGE,"E167.right"),sQuery(id+"F13.wireOp",EDGE,"E167.bottom")])]});
            var Q59;
            Q59=makeQuery(id+"F14.opExtrude","SWEPT_BODY",BODY,{"disambiguationData":[OSD([sQuery(id+"F13.wireOp",EDGE,"E165.top"),sQuery(id+"F13.wireOp",EDGE,"E164.right"),sQuery(id+"F13.wireOp",EDGE,"E165.right"),sQuery(id+"F13.wireOp",EDGE,"E165.bottom")])]});
            var Q60;
            Q60=makeQuery(id+"F14.opExtrude","SWEPT_BODY",BODY,{"disambiguationData":[OSD([sQuery(id+"F13.wireOp",EDGE,"E163.top"),sQuery(id+"F13.wireOp",EDGE,"E162.right"),sQuery(id+"F13.wireOp",EDGE,"E163.right"),sQuery(id+"F13.wireOp",EDGE,"E163.bottom")])]});
            var Q61;
            Q61=makeQuery(id+"F14.opExtrude","SWEPT_BODY",BODY,{"disambiguationData":[OSD([sQuery(id+"F13.wireOp",EDGE,"E221.top"),sQuery(id+"F13.wireOp",EDGE,"E222.right"),sQuery(id+"F13.wireOp",EDGE,"E230")])]});
            var Q62;
            Q62=makeQuery(id+"F14.opExtrude","SWEPT_BODY",BODY,{"disambiguationData":[OSD([sQuery(id+"F13.wireOp",EDGE,"E220.top"),sQuery(id+"F13.wireOp",EDGE,"E221.left"),sQuery(id+"F13.wireOp",EDGE,"E230")])]});
            var Q63;
            Q63=makeQuery(id+"F14.opExtrude","SWEPT_BODY",BODY,{"disambiguationData":[OSD([sQuery(id+"F13.wireOp",EDGE,"E215.top"),sQuery(id+"F13.wireOp",EDGE,"E214.right"),sQuery(id+"F13.wireOp",EDGE,"E227.bottom"),sQuery(id+"F13.wireOp",EDGE,"E230")])]});
            var Q64;
            Q64=makeQuery(id+"F14.opExtrude","CAP_EDGE",EDGE,{"disambiguationData":[OSD([sQuery(id+"F13.wireOp",EDGE,"E165.top")])],"isStart":false});
            transform(context, id + "F16", {"entities" : qUnion([Q0, Q1, Q2, Q3, Q4, Q5, Q6, Q7, Q8, Q9, Q10, Q11, Q12, Q13, Q14, Q15, Q16, Q17, Q18, Q19, Q20, Q21, Q22, Q23, Q24, Q25, Q26, Q27, Q28, Q29, Q30, Q31, Q32, Q33, Q34, Q35, Q36, Q37, Q38, Q39, Q40, Q41, Q42, Q43, Q44, Q45, Q46, Q47, Q48, Q49, Q50, Q51, Q52, Q53, Q54, Q55, Q56, Q57, Q58, Q59, Q60, Q61, Q62, Q63]), "transformType" : TransformType.ROTATION, "transformAxis" : qUnion([Q64]), "angle" : 45 * degree, "oppositeDirection" : true, "makeCopy" : false});
        }
        {
            var Q0;
            Q0=qCreatedBy(makeId("Right.planeOp"),FACE);
            var sketch = newSketch(context, id + "F17", { "sketchPlane" : qUnion([Q0])});
            skLineSegment(sketch, "E232.bottom", {"start": v(12, 0) * mm, "end": v(11, 0) * mm});
            skLineSegment(sketch, "E232.top", {"start": v(11.3, 1) * mm, "end": v(11, 1) * mm});
            skLineSegment(sketch, "E232.right", {"start": v(11, 0) * mm, "end": v(11, 1) * mm});
            skLineSegment(sketch, "E233.bottom", {"start": v(11, 1) * mm, "end": v(10, 1) * mm});
            skLineSegment(sketch, "E233.top", {"start": v(11, 0) * mm, "end": v(10, 0) * mm});
            skLineSegment(sketch, "E233.left", {"start": v(11, 1) * mm, "end": v(11, 0) * mm});
            skLineSegment(sketch, "E233.right", {"start": v(10, 1) * mm, "end": v(10, 0) * mm});
            skLineSegment(sketch, "E234.bottom", {"start": v(10, 1) * mm, "end": v(9, 1) * mm});
            skLineSegment(sketch, "E234.top", {"start": v(10, 0) * mm, "end": v(9, 0) * mm});
            skLineSegment(sketch, "E234.right", {"start": v(9, 1) * mm, "end": v(9, 0) * mm});
            skLineSegment(sketch, "E235.bottom", {"start": v(9, 1) * mm, "end": v(8, 1) * mm});
            skLineSegment(sketch, "E235.top", {"start": v(9, 0) * mm, "end": v(8, 0) * mm});
            skLineSegment(sketch, "E235.right", {"start": v(8, 1) * mm, "end": v(8, 0) * mm});
            skLineSegment(sketch, "E236.bottom", {"start": v(8, 1) * mm, "end": v(7, 1) * mm});
            skLineSegment(sketch, "E236.top", {"start": v(8, 0) * mm, "end": v(7, 0) * mm});
            skLineSegment(sketch, "E236.right", {"start": v(7, 1) * mm, "end": v(7, 0) * mm});
            skLineSegment(sketch, "E237.bottom", {"start": v(7, 1) * mm, "end": v(6, 1) * mm});
            skLineSegment(sketch, "E237.top", {"start": v(7, 0) * mm, "end": v(6, 0) * mm});
            skLineSegment(sketch, "E237.right", {"start": v(6, 1) * mm, "end": v(6, 0) * mm});
            skLineSegment(sketch, "E238.bottom", {"start": v(6, 1) * mm, "end": v(5, 1) * mm});
            skLineSegment(sketch, "E238.top", {"start": v(6, 0) * mm, "end": v(5, 0) * mm});
            skLineSegment(sketch, "E238.right", {"start": v(5, 1) * mm, "end": v(5, 0) * mm});
            skLineSegment(sketch, "E239.bottom", {"start": v(5, 1) * mm, "end": v(4, 1) * mm});
            skLineSegment(sketch, "E239.top", {"start": v(5, 0) * mm, "end": v(4, 0) * mm});
            skLineSegment(sketch, "E239.right", {"start": v(4, 1) * mm, "end": v(4, 0) * mm});
            skLineSegment(sketch, "E240.bottom", {"start": v(4, 1) * mm, "end": v(3, 1) * mm});
            skLineSegment(sketch, "E240.top", {"start": v(4, 0) * mm, "end": v(3, 0) * mm});
            skLineSegment(sketch, "E240.right", {"start": v(3, 1) * mm, "end": v(3, 0) * mm});
            skLineSegment(sketch, "E241.bottom", {"start": v(3, 1) * mm, "end": v(2, 1) * mm});
            skLineSegment(sketch, "E241.top", {"start": v(3, 0) * mm, "end": v(2, 0) * mm});
            skLineSegment(sketch, "E241.right", {"start": v(2, 1) * mm, "end": v(2, 0) * mm});
            skLineSegment(sketch, "E242.bottom", {"start": v(2, 1) * mm, "end": v(1, 1) * mm});
            skLineSegment(sketch, "E242.top", {"start": v(2, 0) * mm, "end": v(1, 0) * mm});
            skLineSegment(sketch, "E242.right", {"start": v(1, 1) * mm, "end": v(1, 0) * mm});
            skLineSegment(sketch, "E243.bottom", {"start": v(1, 1) * mm, "end": v(0.7, 1) * mm});
            skLineSegment(sketch, "E243.top", {"start": v(1, 0) * mm, "end": v(0, 0) * mm});
            skLineSegment(sketch, "E244.right", {"start": v(11, 1) * mm, "end": v(11, 1.4) * mm});
            skLineSegment(sketch, "E245.bottom", {"start": v(10.59, 2) * mm, "end": v(10, 2) * mm});
            skLineSegment(sketch, "E245.left", {"start": v(11, 1.4) * mm, "end": v(11, 1) * mm});
            skLineSegment(sketch, "E245.right", {"start": v(10, 2) * mm, "end": v(10, 1) * mm});
            skLineSegment(sketch, "E246.bottom", {"start": v(10, 2) * mm, "end": v(9, 2) * mm});
            skLineSegment(sketch, "E246.right", {"start": v(9, 2) * mm, "end": v(9, 1) * mm});
            skLineSegment(sketch, "E247.bottom", {"start": v(9, 2) * mm, "end": v(8, 2) * mm});
            skLineSegment(sketch, "E247.right", {"start": v(8, 2) * mm, "end": v(8, 1) * mm});
            skLineSegment(sketch, "E248.bottom", {"start": v(8, 2) * mm, "end": v(7, 2) * mm});
            skLineSegment(sketch, "E248.right", {"start": v(7, 2) * mm, "end": v(7, 1) * mm});
            skLineSegment(sketch, "E249.bottom", {"start": v(7, 2) * mm, "end": v(6, 2) * mm});
            skLineSegment(sketch, "E249.right", {"start": v(6, 2) * mm, "end": v(6, 1) * mm});
            skLineSegment(sketch, "E250.bottom", {"start": v(6, 2) * mm, "end": v(5, 2) * mm});
            skLineSegment(sketch, "E250.right", {"start": v(5, 2) * mm, "end": v(5, 1) * mm});
            skLineSegment(sketch, "E251.bottom", {"start": v(5, 2) * mm, "end": v(4, 2) * mm});
            skLineSegment(sketch, "E251.right", {"start": v(4, 2) * mm, "end": v(4, 1) * mm});
            skLineSegment(sketch, "E252.bottom", {"start": v(4, 2) * mm, "end": v(3, 2) * mm});
            skLineSegment(sketch, "E252.right", {"start": v(3, 2) * mm, "end": v(3, 1) * mm});
            skLineSegment(sketch, "E253.bottom", {"start": v(3, 2) * mm, "end": v(2, 2) * mm});
            skLineSegment(sketch, "E253.right", {"start": v(2, 2) * mm, "end": v(2, 1) * mm});
            skLineSegment(sketch, "E254.bottom", {"start": v(2, 2) * mm, "end": v(1.41, 2) * mm});
            skLineSegment(sketch, "E254.right", {"start": v(1, 1.41) * mm, "end": v(1, 1) * mm});
            skLineSegment(sketch, "E255.right", {"start": v(10, 2.83) * mm, "end": v(10, 2) * mm});
            skLineSegment(sketch, "E256.bottom", {"start": v(9.88, 3) * mm, "end": v(9, 3) * mm});
            skLineSegment(sketch, "E256.right", {"start": v(9, 3) * mm, "end": v(9, 2) * mm});
            skLineSegment(sketch, "E257.bottom", {"start": v(9, 3) * mm, "end": v(8, 3) * mm});
            skLineSegment(sketch, "E257.right", {"start": v(8, 3) * mm, "end": v(8, 2) * mm});
            skLineSegment(sketch, "E258.bottom", {"start": v(8, 3) * mm, "end": v(7, 3) * mm});
            skLineSegment(sketch, "E258.right", {"start": v(7, 3) * mm, "end": v(7, 2) * mm});
            skLineSegment(sketch, "E259.bottom", {"start": v(7, 3) * mm, "end": v(6, 3) * mm});
            skLineSegment(sketch, "E259.right", {"start": v(6, 3) * mm, "end": v(6, 2) * mm});
            skLineSegment(sketch, "E260.bottom", {"start": v(6, 3) * mm, "end": v(5, 3) * mm});
            skLineSegment(sketch, "E260.right", {"start": v(5, 3) * mm, "end": v(5, 2) * mm});
            skLineSegment(sketch, "E261.bottom", {"start": v(5, 3) * mm, "end": v(4, 3) * mm});
            skLineSegment(sketch, "E261.right", {"start": v(4, 3) * mm, "end": v(4, 2) * mm});
            skLineSegment(sketch, "E262.bottom", {"start": v(4, 3) * mm, "end": v(3, 3) * mm});
            skLineSegment(sketch, "E262.right", {"start": v(3, 3) * mm, "end": v(3, 2) * mm});
            skLineSegment(sketch, "E263.bottom", {"start": v(3, 3) * mm, "end": v(2.12, 3) * mm});
            skLineSegment(sketch, "E263.right", {"start": v(2, 2.83) * mm, "end": v(2, 2) * mm});
            skLineSegment(sketch, "E264.right", {"start": v(9, 4) * mm, "end": v(9, 3) * mm});
            skLineSegment(sketch, "E265.bottom", {"start": v(9, 4) * mm, "end": v(8, 4) * mm});
            skLineSegment(sketch, "E265.right", {"start": v(8, 4) * mm, "end": v(8, 3) * mm});
            skLineSegment(sketch, "E266.bottom", {"start": v(8, 4) * mm, "end": v(7, 4) * mm});
            skLineSegment(sketch, "E266.right", {"start": v(7, 4) * mm, "end": v(7, 3) * mm});
            skLineSegment(sketch, "E267.bottom", {"start": v(7, 4) * mm, "end": v(6, 4) * mm});
            skLineSegment(sketch, "E267.right", {"start": v(6, 4) * mm, "end": v(6, 3) * mm});
            skLineSegment(sketch, "E268.bottom", {"start": v(6, 4) * mm, "end": v(5, 4) * mm});
            skLineSegment(sketch, "E268.right", {"start": v(5, 4) * mm, "end": v(5, 3) * mm});
            skLineSegment(sketch, "E269.bottom", {"start": v(5, 4) * mm, "end": v(4, 4) * mm});
            skLineSegment(sketch, "E269.right", {"start": v(4, 4) * mm, "end": v(4, 3) * mm});
            skLineSegment(sketch, "E270.bottom", {"start": v(4, 4) * mm, "end": v(3, 4) * mm});
            skLineSegment(sketch, "E270.right", {"start": v(3, 4) * mm, "end": v(3, 3) * mm});
            skLineSegment(sketch, "E271.right", {"start": v(8, 5) * mm, "end": v(8, 4) * mm});
            skLineSegment(sketch, "E272.bottom", {"start": v(8, 5) * mm, "end": v(7, 5) * mm});
            skLineSegment(sketch, "E272.right", {"start": v(7, 5) * mm, "end": v(7, 4) * mm});
            skLineSegment(sketch, "E273.bottom", {"start": v(7, 5) * mm, "end": v(6, 5) * mm});
            skLineSegment(sketch, "E273.right", {"start": v(6, 5) * mm, "end": v(6, 4) * mm});
            skLineSegment(sketch, "E274.bottom", {"start": v(6, 5) * mm, "end": v(5, 5) * mm});
            skLineSegment(sketch, "E274.right", {"start": v(5, 5) * mm, "end": v(5, 4) * mm});
            skLineSegment(sketch, "E275.bottom", {"start": v(5, 5) * mm, "end": v(4, 5) * mm});
            skLineSegment(sketch, "E275.right", {"start": v(4, 5) * mm, "end": v(4, 4) * mm});
            skLineSegment(sketch, "E276.right", {"start": v(7, 6) * mm, "end": v(7, 5) * mm});
            skLineSegment(sketch, "E277.bottom", {"start": v(7, 6) * mm, "end": v(6, 6) * mm});
            skLineSegment(sketch, "E277.right", {"start": v(6, 6) * mm, "end": v(6, 5) * mm});
            skLineSegment(sketch, "E278.bottom", {"start": v(6, 6) * mm, "end": v(5, 6) * mm});
            skLineSegment(sketch, "E278.right", {"start": v(5, 6) * mm, "end": v(5, 5) * mm});
            skLineSegment(sketch, "E279.top", {"start": v(10, 2) * mm, "end": v(10.59, 2) * mm});
            skLineSegment(sketch, "E280.bottom", {"start": v(9, 4) * mm, "end": v(9.17, 4) * mm});
            skLineSegment(sketch, "E280.top", {"start": v(9, 3) * mm, "end": v(9.88, 3) * mm});
            skLineSegment(sketch, "E281.bottom", {"start": v(8, 5) * mm, "end": v(8.46, 5) * mm});
            skLineSegment(sketch, "E281.top", {"start": v(8, 4) * mm, "end": v(9, 4) * mm});
            skLineSegment(sketch, "E281.right", {"start": v(9, 4.24) * mm, "end": v(9, 4) * mm});
            skLineSegment(sketch, "E282.top", {"start": v(7.76, 6) * mm, "end": v(7, 6) * mm});
            skLineSegment(sketch, "E282.left", {"start": v(8, 5) * mm, "end": v(8, 5.65) * mm});
            skLineSegment(sketch, "E282.right", {"start": v(7, 5) * mm, "end": v(7, 6) * mm});
            skLineSegment(sketch, "E283.right", {"start": v(7, 6) * mm, "end": v(7, 7) * mm});
            skLineSegment(sketch, "E284.bottom", {"start": v(4, 5) * mm, "end": v(5, 5) * mm});
            skLineSegment(sketch, "E284.top", {"start": v(4.24, 6) * mm, "end": v(5, 6) * mm});
            skLineSegment(sketch, "E284.right", {"start": v(5, 5) * mm, "end": v(5, 6) * mm});
            skLineSegment(sketch, "E285.bottom", {"start": v(7, 7) * mm, "end": v(6, 7) * mm});
            skLineSegment(sketch, "E285.left", {"start": v(7, 7) * mm, "end": v(7, 6) * mm});
            skLineSegment(sketch, "E285.right", {"start": v(6, 7) * mm, "end": v(6, 6) * mm});
            skLineSegment(sketch, "E286.bottom", {"start": v(6, 7) * mm, "end": v(5, 7) * mm});
            skLineSegment(sketch, "E286.right", {"start": v(5, 7) * mm, "end": v(5, 6) * mm});
            skLineSegment(sketch, "E287.top", {"start": v(5, 6) * mm, "end": v(4.24, 6) * mm});
            skLineSegment(sketch, "E288.right", {"start": v(7, 7) * mm, "end": v(7, 7.07) * mm});
            skLineSegment(sketch, "E289.bottom", {"start": v(6, 7) * mm, "end": v(7, 7) * mm});
            skLineSegment(sketch, "E289.top", {"start": v(6, 8.05) * mm, "end": v(6.3, 8.05) * mm});
            skLineSegment(sketch, "E289.left", {"start": v(6, 7) * mm, "end": v(6, 8.05) * mm});
            skLineSegment(sketch, "E290.bottom", {"start": v(5, 7) * mm, "end": v(6, 7) * mm});
            skLineSegment(sketch, "E290.top", {"start": v(5.7, 8.05) * mm, "end": v(6, 8.05) * mm});
            skLineSegment(sketch, "E290.left", {"start": v(5, 7) * mm, "end": v(5, 7.07) * mm});
            skLineSegment(sketch, "E291.bottom", {"start": v(1.41, 2) * mm, "end": v(2, 2) * mm});
            skLineSegment(sketch, "E291.right", {"start": v(2, 2) * mm, "end": v(2, 2.83) * mm});
            skLineSegment(sketch, "E292.bottom", {"start": v(2.12, 3) * mm, "end": v(3, 3) * mm});
            skLineSegment(sketch, "E292.top", {"start": v(2.83, 4) * mm, "end": v(3, 4) * mm});
            skLineSegment(sketch, "E292.right", {"start": v(3, 3) * mm, "end": v(3, 4) * mm});
            skLineSegment(sketch, "E293.bottom", {"start": v(3, 4) * mm, "end": v(4, 4) * mm});
            skLineSegment(sketch, "E293.top", {"start": v(3.54, 5) * mm, "end": v(4, 5) * mm});
            skLineSegment(sketch, "E293.left", {"start": v(3, 4) * mm, "end": v(3, 4.24) * mm});
            skLineSegment(sketch, "E293.right", {"start": v(4, 4) * mm, "end": v(4, 5) * mm});
            skLineSegment(sketch, "E294.right", {"start": v(4, 5) * mm, "end": v(4, 5.65) * mm});
            skLineSegment(sketch, "E295.bottom", {"start": v(0.7, 1) * mm, "end": v(1, 1) * mm});
            skLineSegment(sketch, "E295.right", {"start": v(1, 1) * mm, "end": v(1, 1.41) * mm});
            skLineSegment(sketch, "E296.bottom", {"start": v(9.17, 4) * mm, "end": v(9, 4) * mm});
            skLineSegment(sketch, "E296.right", {"start": v(9, 4) * mm, "end": v(9, 4.24) * mm});
            skLineSegment(sketch, "E297.left", {"start": v(8, 5.65) * mm, "end": v(8, 5) * mm});
            skLineSegment(sketch, "E298.bottom", {"start": v(5, 7) * mm, "end": v(4.95, 7) * mm});
            skLineSegment(sketch, "E299.bottom", {"start": v(4.95, 7) * mm, "end": v(5, 7) * mm});
            skLineSegment(sketch, "E300.bottom", {"start": v(7.05, 7) * mm, "end": v(7, 7) * mm});
            skLineSegment(sketch, "E301.bottom", {"start": v(6.3, 8.05) * mm, "end": v(6, 8.05) * mm});
            skLineSegment(sketch, "E301.right", {"start": v(6, 8.05) * mm, "end": v(6, 8.48) * mm});
            skLineSegment(sketch, "E302", {"start": v(0, 0) * mm, "end": v(6, 8.48) * mm});
            skLineSegment(sketch, "E303", {"start": v(6, 8.48) * mm, "end": v(12, 0) * mm});
            skSolve(sketch);
        }
        {
            var Q0;
            Q0=makeQuery(id+"F17.imprint","IMPRINT",FACE,{"disambiguationData":[TD([[makeQuery(id+"F17.imprint","IMPRINT",EDGE,{"derivedFrom":sQuery(id+"F17.wireOp",EDGE,"E233.top")}),-1.0]])]});
            var Q1;
            Q1=makeQuery(id+"F17.imprint","IMPRINT",FACE,{"disambiguationData":[TD([[makeQuery(id+"F17.imprint","IMPRINT",EDGE,{"derivedFrom":sQuery(id+"F17.wireOp",EDGE,"E234.bottom")}),-1.0]])]});
            var Q2;
            Q2=makeQuery(id+"F17.imprint","IMPRINT",FACE,{"disambiguationData":[TD([[makeQuery(id+"F17.imprint","IMPRINT",EDGE,{"derivedFrom":sQuery(id+"F17.wireOp",EDGE,"E235.top")}),-1.0]])]});
            var Q3;
            {var subQ0=sQuery(id+"F17.wireOp",EDGE,"E232.top");Q3=makeQuery(id+"F17.imprint","IMPRINT",FACE,{"disambiguationData":[TD([[makeQuery(id+"F17.imprint","IMPRINT",EDGE,{"derivedFrom":subQ0}),-1.0]])]});}
            var Q4;
            {var subQ0=sQuery(id+"F17.wireOp",EDGE,"E279.top");Q4=makeQuery(id+"F17.imprint","IMPRINT",FACE,{"disambiguationData":[TD([[makeQuery(id+"F17.imprint","IMPRINT",EDGE,{"derivedFrom":subQ0}),1.0]])]});}
            var Q5;
            {var subQ0=sQuery(id+"F17.wireOp",EDGE,"E280.top");Q5=makeQuery(id+"F17.imprint","IMPRINT",FACE,{"disambiguationData":[TD([[makeQuery(id+"F17.imprint","IMPRINT",EDGE,{"derivedFrom":subQ0}),1.0]])]});}
            var Q6;
            Q6=makeQuery(id+"F17.imprint","IMPRINT",FACE,{"disambiguationData":[TD([[makeQuery(id+"F17.imprint","IMPRINT",EDGE,{"derivedFrom":sQuery(id+"F17.wireOp",EDGE,"E247.bottom")}),-1.0]])]});
            var Q7;
            Q7=makeQuery(id+"F17.imprint","IMPRINT",FACE,{"disambiguationData":[TD([[makeQuery(id+"F17.imprint","IMPRINT",EDGE,{"derivedFrom":sQuery(id+"F17.wireOp",EDGE,"E236.bottom")}),-1.0]])]});
            var Q8;
            Q8=makeQuery(id+"F17.imprint","IMPRINT",FACE,{"disambiguationData":[TD([[makeQuery(id+"F17.imprint","IMPRINT",EDGE,{"derivedFrom":sQuery(id+"F17.wireOp",EDGE,"E237.top")}),-1.0]])]});
            var Q9;
            Q9=makeQuery(id+"F17.imprint","IMPRINT",FACE,{"disambiguationData":[TD([[makeQuery(id+"F17.imprint","IMPRINT",EDGE,{"derivedFrom":sQuery(id+"F17.wireOp",EDGE,"E238.bottom")}),-1.0]])]});
            var Q10;
            Q10=makeQuery(id+"F17.imprint","IMPRINT",FACE,{"disambiguationData":[TD([[makeQuery(id+"F17.imprint","IMPRINT",EDGE,{"derivedFrom":sQuery(id+"F17.wireOp",EDGE,"E249.bottom")}),-1.0]])]});
            var Q11;
            Q11=makeQuery(id+"F17.imprint","IMPRINT",FACE,{"disambiguationData":[TD([[makeQuery(id+"F17.imprint","IMPRINT",EDGE,{"derivedFrom":sQuery(id+"F17.wireOp",EDGE,"E258.bottom")}),-1.0]])]});
            var Q12;
            Q12=makeQuery(id+"F17.imprint","IMPRINT",FACE,{"disambiguationData":[TD([[makeQuery(id+"F17.imprint","IMPRINT",EDGE,{"derivedFrom":sQuery(id+"F17.wireOp",EDGE,"E281.top")}),1.0]])]});
            var Q13;
            Q13=makeQuery(id+"F17.imprint","IMPRINT",FACE,{"disambiguationData":[TD([[makeQuery(id+"F17.imprint","IMPRINT",EDGE,{"derivedFrom":sQuery(id+"F17.wireOp",EDGE,"E239.top")}),-1.0]])]});
            var Q14;
            Q14=makeQuery(id+"F17.imprint","IMPRINT",FACE,{"disambiguationData":[TD([[makeQuery(id+"F17.imprint","IMPRINT",EDGE,{"derivedFrom":sQuery(id+"F17.wireOp",EDGE,"E240.bottom")}),-1.0]])]});
            var Q15;
            Q15=makeQuery(id+"F17.imprint","IMPRINT",FACE,{"disambiguationData":[TD([[makeQuery(id+"F17.imprint","IMPRINT",EDGE,{"derivedFrom":sQuery(id+"F17.wireOp",EDGE,"E241.top")}),-1.0]])]});
            var Q16;
            Q16=makeQuery(id+"F17.imprint","IMPRINT",FACE,{"disambiguationData":[TD([[makeQuery(id+"F17.imprint","IMPRINT",EDGE,{"derivedFrom":sQuery(id+"F17.wireOp",EDGE,"E251.bottom")}),-1.0]])]});
            var Q17;
            Q17=makeQuery(id+"F17.imprint","IMPRINT",FACE,{"disambiguationData":[TD([[makeQuery(id+"F17.imprint","IMPRINT",EDGE,{"derivedFrom":sQuery(id+"F17.wireOp",EDGE,"E260.bottom")}),-1.0]])]});
            var Q18;
            Q18=makeQuery(id+"F17.imprint","IMPRINT",FACE,{"disambiguationData":[TD([[makeQuery(id+"F17.imprint","IMPRINT",EDGE,{"derivedFrom":sQuery(id+"F17.wireOp",EDGE,"E267.bottom")}),-1.0]])]});
            var Q19;
            Q19=makeQuery(id+"F17.imprint","IMPRINT",FACE,{"disambiguationData":[TD([[makeQuery(id+"F17.imprint","IMPRINT",EDGE,{"derivedFrom":sQuery(id+"F17.wireOp",EDGE,"E272.bottom")}),-1.0]])]});
            var Q20;
            Q20=makeQuery(id+"F17.imprint","IMPRINT",FACE,{"disambiguationData":[TD([[makeQuery(id+"F17.imprint","IMPRINT",EDGE,{"derivedFrom":sQuery(id+"F17.wireOp",EDGE,"E277.bottom")}),-1.0]])]});
            var Q21;
            Q21=makeQuery(id+"F17.imprint","IMPRINT",FACE,{"disambiguationData":[TD([[makeQuery(id+"F17.imprint","IMPRINT",EDGE,{"derivedFrom":sQuery(id+"F17.wireOp",EDGE,"E274.bottom")}),-1.0]])]});
            var Q22;
            Q22=makeQuery(id+"F17.imprint","IMPRINT",FACE,{"disambiguationData":[TD([[makeQuery(id+"F17.imprint","IMPRINT",EDGE,{"derivedFrom":sQuery(id+"F17.wireOp",EDGE,"E269.bottom")}),-1.0]])]});
            var Q23;
            Q23=makeQuery(id+"F17.imprint","IMPRINT",FACE,{"disambiguationData":[TD([[makeQuery(id+"F17.imprint","IMPRINT",EDGE,{"derivedFrom":sQuery(id+"F17.wireOp",EDGE,"E262.bottom")}),-1.0]])]});
            var Q24;
            Q24=makeQuery(id+"F17.imprint","IMPRINT",FACE,{"disambiguationData":[TD([[makeQuery(id+"F17.imprint","IMPRINT",EDGE,{"derivedFrom":sQuery(id+"F17.wireOp",EDGE,"E253.bottom")}),-1.0]])]});
            var Q25;
            Q25=makeQuery(id+"F17.imprint","IMPRINT",FACE,{"disambiguationData":[TD([[makeQuery(id+"F17.imprint","IMPRINT",EDGE,{"derivedFrom":sQuery(id+"F17.wireOp",EDGE,"E242.bottom")}),-1.0]])]});
            var Q26;
            {var subQ0=sQuery(id+"F17.wireOp",EDGE,"E243.top");Q26=makeQuery(id+"F17.imprint","IMPRINT",FACE,{"disambiguationData":[TD([[makeQuery(id+"F17.imprint","IMPRINT",EDGE,{"derivedFrom":subQ0}),-1.0]])]});}
            var Q27;
            {var subQ0=sQuery(id+"F17.wireOp",EDGE,"E292.top");Q27=makeQuery(id+"F17.imprint","IMPRINT",FACE,{"disambiguationData":[TD([[makeQuery(id+"F17.imprint","IMPRINT",EDGE,{"derivedFrom":subQ0}),1.0]])]});}
            var Q28;
            {var subQ0=sQuery(id+"F17.wireOp",EDGE,"E293.top");Q28=makeQuery(id+"F17.imprint","IMPRINT",FACE,{"disambiguationData":[TD([[makeQuery(id+"F17.imprint","IMPRINT",EDGE,{"derivedFrom":subQ0}),1.0]])]});}
            var Q29;
            {var subQ0=sQuery(id+"F17.wireOp",EDGE,"E287.top");Q29=makeQuery(id+"F17.imprint","IMPRINT",FACE,{"disambiguationData":[TD([[makeQuery(id+"F17.imprint","IMPRINT",EDGE,{"derivedFrom":subQ0}),-1.0]])]});}
            var Q30;
            {var subQ0=sQuery(id+"F17.wireOp",EDGE,"E301.bottom");Q30=makeQuery(id+"F17.imprint","IMPRINT",FACE,{"disambiguationData":[TD([[makeQuery(id+"F17.imprint","IMPRINT",EDGE,{"derivedFrom":subQ0}),-1.0]])]});}
            var Q31;
            Q31=makeQuery(id+"F17.imprint","IMPRINT",FACE,{"disambiguationData":[TD([[makeQuery(id+"F17.imprint","IMPRINT",EDGE,{"derivedFrom":sQuery(id+"F17.wireOp",EDGE,"E290.bottom")}),1.0]])]});
            extrude(context, id + "F18", {"entities" : qUnion([Q0, Q1, Q2, Q3, Q4, Q5, Q6, Q7, Q8, Q9, Q10, Q11, Q12, Q13, Q14, Q15, Q16, Q17, Q18, Q19, Q20, Q21, Q22, Q23, Q24, Q25, Q26, Q27, Q28, Q29, Q30, Q31]), "depth" : 0.35 * mm, "offsetDistance" : 25.4 * mm});
        }
        {
            var Q0;
            Q0=makeQuery(id+"FjME2WR4CrJvMWv_1.opExtrude","SWEPT_BODY",BODY,{"disambiguationData":[OSD([sQuery(id+"F17.wireOp",EDGE,"E232.bottom"),sQuery(id+"F17.wireOp",EDGE,"E233.left"),sQuery(id+"F17.wireOp",EDGE,"E233.bottom"),sQuery(id+"F17.wireOp",EDGE,"E245.right"),sQuery(id+"F17.wireOp",EDGE,"E232.top"),sQuery(id+"F17.wireOp",EDGE,"E244.right"),sQuery(id+"F17.wireOp",EDGE,"E279.top"),sQuery(id+"F17.wireOp",EDGE,"E303")])]});
            var Q1;
            Q1=makeQuery(id+"FjME2WR4CrJvMWv_1.opExtrude","SWEPT_BODY",BODY,{"disambiguationData":[OSD([sQuery(id+"F17.wireOp",EDGE,"E246.bottom"),sQuery(id+"F17.wireOp",EDGE,"E256.right"),sQuery(id+"F17.wireOp",EDGE,"E255.right"),sQuery(id+"F17.wireOp",EDGE,"E280.top"),sQuery(id+"F17.wireOp",EDGE,"E303")])]});
            var Q2;
            Q2=makeQuery(id+"FjME2WR4CrJvMWv_1.opExtrude","SWEPT_BODY",BODY,{"disambiguationData":[OSD([sQuery(id+"F17.wireOp",EDGE,"E280.bottom"),sQuery(id+"F17.wireOp",EDGE,"E281.right"),sQuery(id+"F17.wireOp",EDGE,"E303")])]});
            var Q3;
            Q3=makeQuery(id+"F18.opExtrude","SWEPT_BODY",BODY,{"disambiguationData":[OSD([sQuery(id+"F17.wireOp",EDGE,"E280.top"),sQuery(id+"F17.wireOp",EDGE,"E264.right"),sQuery(id+"F17.wireOp",EDGE,"E280.bottom"),sQuery(id+"F17.wireOp",EDGE,"E303")])]});
            var Q4;
            Q4=makeQuery(id+"FjME2WR4CrJvMWv_1.opExtrude","SWEPT_BODY",BODY,{"disambiguationData":[OSD([sQuery(id+"F17.wireOp",EDGE,"E281.bottom"),sQuery(id+"F17.wireOp",EDGE,"E297.left"),sQuery(id+"F17.wireOp",EDGE,"E303")])]});
            var Q5;
            Q5=makeQuery(id+"FjME2WR4CrJvMWv_1.opExtrude","SWEPT_BODY",BODY,{"disambiguationData":[OSD([sQuery(id+"F17.wireOp",EDGE,"E290.top"),sQuery(id+"F17.wireOp",EDGE,"E301.right"),sQuery(id+"F17.wireOp",EDGE,"E302")])]});
            var Q6;
            Q6=makeQuery(id+"FjME2WR4CrJvMWv_1.opExtrude","SWEPT_BODY",BODY,{"disambiguationData":[OSD([sQuery(id+"F17.wireOp",EDGE,"E282.top"),sQuery(id+"F17.wireOp",EDGE,"E285.left"),sQuery(id+"F17.wireOp",EDGE,"E300.bottom"),sQuery(id+"F17.wireOp",EDGE,"E303")])]});
            var Q7;
            Q7=makeQuery(id+"FjME2WR4CrJvMWv_1.opExtrude","SWEPT_BODY",BODY,{"disambiguationData":[OSD([sQuery(id+"F17.wireOp",EDGE,"E289.bottom"),sQuery(id+"F17.wireOp",EDGE,"E289.left"),sQuery(id+"F17.wireOp",EDGE,"E288.right"),sQuery(id+"F17.wireOp",EDGE,"E301.bottom"),sQuery(id+"F17.wireOp",EDGE,"E303")])]});
            var Q8;
            Q8=makeQuery(id+"F18.opExtrude","SWEPT_BODY",BODY,{"disambiguationData":[OSD([sQuery(id+"F17.wireOp",EDGE,"E290.bottom"),sQuery(id+"F17.wireOp",EDGE,"E289.left"),sQuery(id+"F17.wireOp",EDGE,"E290.left"),sQuery(id+"F17.wireOp",EDGE,"E290.top"),sQuery(id+"F17.wireOp",EDGE,"E302")])]});
            var Q9;
            Q9=makeQuery(id+"FjME2WR4CrJvMWv_1.opExtrude","SWEPT_BODY",BODY,{"disambiguationData":[OSD([sQuery(id+"F17.wireOp",EDGE,"E257.bottom"),sQuery(id+"F17.wireOp",EDGE,"E265.right"),sQuery(id+"F17.wireOp",EDGE,"E264.right"),sQuery(id+"F17.wireOp",EDGE,"E281.top")])]});
            var Q10;
            Q10=makeQuery(id+"F18.opExtrude","SWEPT_BODY",BODY,{"disambiguationData":[OSD([sQuery(id+"F17.wireOp",EDGE,"E233.top"),sQuery(id+"F17.wireOp",EDGE,"E233.left"),sQuery(id+"F17.wireOp",EDGE,"E233.right"),sQuery(id+"F17.wireOp",EDGE,"E233.bottom")])]});
            var Q11;
            Q11=makeQuery(id+"F18.opExtrude","SWEPT_BODY",BODY,{"disambiguationData":[OSD([sQuery(id+"F17.wireOp",EDGE,"E281.top"),sQuery(id+"F17.wireOp",EDGE,"E271.right"),sQuery(id+"F17.wireOp",EDGE,"E281.right"),sQuery(id+"F17.wireOp",EDGE,"E281.bottom"),sQuery(id+"F17.wireOp",EDGE,"E303")])]});
            var Q12;
            Q12=makeQuery(id+"F18.opExtrude","SWEPT_BODY",BODY,{"disambiguationData":[OSD([sQuery(id+"F17.wireOp",EDGE,"E277.bottom"),sQuery(id+"F17.wireOp",EDGE,"E285.left"),sQuery(id+"F17.wireOp",EDGE,"E285.right"),sQuery(id+"F17.wireOp",EDGE,"E289.bottom")])]});
            var Q13;
            Q13=makeQuery(id+"F18.opExtrude","SWEPT_BODY",BODY,{"disambiguationData":[OSD([sQuery(id+"F17.wireOp",EDGE,"E272.bottom"),sQuery(id+"F17.wireOp",EDGE,"E282.right"),sQuery(id+"F17.wireOp",EDGE,"E282.top"),sQuery(id+"F17.wireOp",EDGE,"E297.left"),sQuery(id+"F17.wireOp",EDGE,"E303")])]});
            var Q14;
            Q14=makeQuery(id+"F18.opExtrude","SWEPT_BODY",BODY,{"disambiguationData":[OSD([sQuery(id+"F17.wireOp",EDGE,"E279.top"),sQuery(id+"F17.wireOp",EDGE,"E255.right"),sQuery(id+"F17.wireOp",EDGE,"E303")])]});
            var Q15;
            Q15=makeQuery(id+"F18.opExtrude","SWEPT_BODY",BODY,{"disambiguationData":[OSD([sQuery(id+"F17.wireOp",EDGE,"E232.top"),sQuery(id+"F17.wireOp",EDGE,"E244.right"),sQuery(id+"F17.wireOp",EDGE,"E303")])]});
            var Q16;
            Q16=makeQuery(id+"F18.opExtrude","SWEPT_BODY",BODY,{"disambiguationData":[OSD([sQuery(id+"F17.wireOp",EDGE,"E301.bottom"),sQuery(id+"F17.wireOp",EDGE,"E301.right"),sQuery(id+"F17.wireOp",EDGE,"E303")])]});
            var Q17;
            Q17=makeQuery(id+"FjME2WR4CrJvMWv_1.opExtrude","SWEPT_BODY",BODY,{"disambiguationData":[OSD([sQuery(id+"F17.wireOp",EDGE,"E266.bottom"),sQuery(id+"F17.wireOp",EDGE,"E272.right"),sQuery(id+"F17.wireOp",EDGE,"E271.right"),sQuery(id+"F17.wireOp",EDGE,"E272.bottom")])]});
            var Q18;
            Q18=makeQuery(id+"FjME2WR4CrJvMWv_1.opExtrude","SWEPT_BODY",BODY,{"disambiguationData":[OSD([sQuery(id+"F17.wireOp",EDGE,"E234.top"),sQuery(id+"F17.wireOp",EDGE,"E233.right"),sQuery(id+"F17.wireOp",EDGE,"E234.right"),sQuery(id+"F17.wireOp",EDGE,"E234.bottom")])]});
            var Q19;
            Q19=makeQuery(id+"F18.opExtrude","SWEPT_BODY",BODY,{"disambiguationData":[OSD([sQuery(id+"F17.wireOp",EDGE,"E247.bottom"),sQuery(id+"F17.wireOp",EDGE,"E256.right"),sQuery(id+"F17.wireOp",EDGE,"E257.right"),sQuery(id+"F17.wireOp",EDGE,"E257.bottom")])]});
            var Q20;
            Q20=makeQuery(id+"F18.opExtrude","SWEPT_BODY",BODY,{"disambiguationData":[OSD([sQuery(id+"F17.wireOp",EDGE,"E258.bottom"),sQuery(id+"F17.wireOp",EDGE,"E265.right"),sQuery(id+"F17.wireOp",EDGE,"E266.right"),sQuery(id+"F17.wireOp",EDGE,"E266.bottom")])]});
            var Q21;
            Q21=makeQuery(id+"F18.opExtrude","SWEPT_BODY",BODY,{"disambiguationData":[OSD([sQuery(id+"F17.wireOp",EDGE,"E234.bottom"),sQuery(id+"F17.wireOp",EDGE,"E245.right"),sQuery(id+"F17.wireOp",EDGE,"E246.right"),sQuery(id+"F17.wireOp",EDGE,"E246.bottom")])]});
            var Q22;
            Q22=makeQuery(id+"FjME2WR4CrJvMWv_1.opExtrude","SWEPT_BODY",BODY,{"disambiguationData":[OSD([sQuery(id+"F17.wireOp",EDGE,"E284.bottom"),sQuery(id+"F17.wireOp",EDGE,"E284.right"),sQuery(id+"F17.wireOp",EDGE,"E294.right"),sQuery(id+"F17.wireOp",EDGE,"E287.top"),sQuery(id+"F17.wireOp",EDGE,"E302")])]});
            var Q23;
            Q23=makeQuery(id+"FjME2WR4CrJvMWv_1.opExtrude","SWEPT_BODY",BODY,{"disambiguationData":[OSD([sQuery(id+"F17.wireOp",EDGE,"E278.bottom"),sQuery(id+"F17.wireOp",EDGE,"E285.right"),sQuery(id+"F17.wireOp",EDGE,"E290.bottom"),sQuery(id+"F17.wireOp",EDGE,"E286.right")])]});
            var Q24;
            Q24=makeQuery(id+"FjME2WR4CrJvMWv_1.opExtrude","SWEPT_BODY",BODY,{"disambiguationData":[OSD([sQuery(id+"F17.wireOp",EDGE,"E273.bottom"),sQuery(id+"F17.wireOp",EDGE,"E277.right"),sQuery(id+"F17.wireOp",EDGE,"E282.right"),sQuery(id+"F17.wireOp",EDGE,"E277.bottom")])]});
            var Q25;
            Q25=makeQuery(id+"FjME2WR4CrJvMWv_1.opExtrude","SWEPT_BODY",BODY,{"disambiguationData":[OSD([sQuery(id+"F17.wireOp",EDGE,"E293.bottom"),sQuery(id+"F17.wireOp",EDGE,"E293.right"),sQuery(id+"F17.wireOp",EDGE,"E293.left"),sQuery(id+"F17.wireOp",EDGE,"E293.top"),sQuery(id+"F17.wireOp",EDGE,"E302")])]});
            var Q26;
            Q26=makeQuery(id+"FjME2WR4CrJvMWv_1.opExtrude","SWEPT_BODY",BODY,{"disambiguationData":[OSD([sQuery(id+"F17.wireOp",EDGE,"E291.bottom"),sQuery(id+"F17.wireOp",EDGE,"E291.right"),sQuery(id+"F17.wireOp",EDGE,"E302")])]});
            var Q27;
            Q27=makeQuery(id+"FjME2WR4CrJvMWv_1.opExtrude","SWEPT_BODY",BODY,{"disambiguationData":[OSD([sQuery(id+"F17.wireOp",EDGE,"E295.bottom"),sQuery(id+"F17.wireOp",EDGE,"E295.right"),sQuery(id+"F17.wireOp",EDGE,"E302")])]});
            var Q28;
            Q28=makeQuery(id+"FjME2WR4CrJvMWv_1.opExtrude","SWEPT_BODY",BODY,{"disambiguationData":[OSD([sQuery(id+"F17.wireOp",EDGE,"E299.bottom"),sQuery(id+"F17.wireOp",EDGE,"E290.left"),sQuery(id+"F17.wireOp",EDGE,"E302")])]});
            var Q29;
            Q29=makeQuery(id+"FjME2WR4CrJvMWv_1.opExtrude","SWEPT_BODY",BODY,{"disambiguationData":[OSD([sQuery(id+"F17.wireOp",EDGE,"E235.bottom"),sQuery(id+"F17.wireOp",EDGE,"E246.right"),sQuery(id+"F17.wireOp",EDGE,"E247.right"),sQuery(id+"F17.wireOp",EDGE,"E247.bottom")])]});
            var Q30;
            Q30=makeQuery(id+"FjME2WR4CrJvMWv_1.opExtrude","SWEPT_BODY",BODY,{"disambiguationData":[OSD([sQuery(id+"F17.wireOp",EDGE,"E259.bottom"),sQuery(id+"F17.wireOp",EDGE,"E266.right"),sQuery(id+"F17.wireOp",EDGE,"E267.right"),sQuery(id+"F17.wireOp",EDGE,"E267.bottom")])]});
            var Q31;
            Q31=makeQuery(id+"FjME2WR4CrJvMWv_1.opExtrude","SWEPT_BODY",BODY,{"disambiguationData":[OSD([sQuery(id+"F17.wireOp",EDGE,"E248.bottom"),sQuery(id+"F17.wireOp",EDGE,"E257.right"),sQuery(id+"F17.wireOp",EDGE,"E258.right"),sQuery(id+"F17.wireOp",EDGE,"E258.bottom")])]});
            var Q32;
            Q32=makeQuery(id+"F18.opExtrude","SWEPT_BODY",BODY,{"disambiguationData":[OSD([sQuery(id+"F17.wireOp",EDGE,"E293.top"),sQuery(id+"F17.wireOp",EDGE,"E294.right"),sQuery(id+"F17.wireOp",EDGE,"E302")])]});
            var Q33;
            Q33=makeQuery(id+"F18.opExtrude","SWEPT_BODY",BODY,{"disambiguationData":[OSD([sQuery(id+"F17.wireOp",EDGE,"E274.bottom"),sQuery(id+"F17.wireOp",EDGE,"E277.right"),sQuery(id+"F17.wireOp",EDGE,"E284.right"),sQuery(id+"F17.wireOp",EDGE,"E278.bottom")])]});
            var Q34;
            Q34=makeQuery(id+"F18.opExtrude","SWEPT_BODY",BODY,{"disambiguationData":[OSD([sQuery(id+"F17.wireOp",EDGE,"E267.bottom"),sQuery(id+"F17.wireOp",EDGE,"E272.right"),sQuery(id+"F17.wireOp",EDGE,"E273.right"),sQuery(id+"F17.wireOp",EDGE,"E273.bottom")])]});
            var Q35;
            Q35=makeQuery(id+"F18.opExtrude","SWEPT_BODY",BODY,{"disambiguationData":[OSD([sQuery(id+"F17.wireOp",EDGE,"E253.bottom"),sQuery(id+"F17.wireOp",EDGE,"E262.right"),sQuery(id+"F17.wireOp",EDGE,"E292.bottom"),sQuery(id+"F17.wireOp",EDGE,"E291.right"),sQuery(id+"F17.wireOp",EDGE,"E302")])]});
            var Q36;
            Q36=makeQuery(id+"F18.opExtrude","SWEPT_BODY",BODY,{"disambiguationData":[OSD([sQuery(id+"F17.wireOp",EDGE,"E242.bottom"),sQuery(id+"F17.wireOp",EDGE,"E253.right"),sQuery(id+"F17.wireOp",EDGE,"E291.bottom"),sQuery(id+"F17.wireOp",EDGE,"E295.right"),sQuery(id+"F17.wireOp",EDGE,"E302")])]});
            var Q37;
            Q37=makeQuery(id+"F18.opExtrude","SWEPT_BODY",BODY,{"disambiguationData":[OSD([sQuery(id+"F17.wireOp",EDGE,"E235.top"),sQuery(id+"F17.wireOp",EDGE,"E234.right"),sQuery(id+"F17.wireOp",EDGE,"E235.right"),sQuery(id+"F17.wireOp",EDGE,"E235.bottom")])]});
            var Q38;
            Q38=makeQuery(id+"F18.opExtrude","SWEPT_BODY",BODY,{"disambiguationData":[OSD([sQuery(id+"F17.wireOp",EDGE,"E287.top"),sQuery(id+"F17.wireOp",EDGE,"E286.right"),sQuery(id+"F17.wireOp",EDGE,"E299.bottom"),sQuery(id+"F17.wireOp",EDGE,"E302")])]});
            var Q39;
            Q39=makeQuery(id+"F18.opExtrude","SWEPT_BODY",BODY,{"disambiguationData":[OSD([sQuery(id+"F17.wireOp",EDGE,"E292.top"),sQuery(id+"F17.wireOp",EDGE,"E293.left"),sQuery(id+"F17.wireOp",EDGE,"E302")])]});
            var Q40;
            Q40=makeQuery(id+"FjME2WR4CrJvMWv_1.opExtrude","SWEPT_BODY",BODY,{"disambiguationData":[OSD([sQuery(id+"F17.wireOp",EDGE,"E236.top"),sQuery(id+"F17.wireOp",EDGE,"E235.right"),sQuery(id+"F17.wireOp",EDGE,"E236.right"),sQuery(id+"F17.wireOp",EDGE,"E236.bottom")])]});
            var Q41;
            Q41=makeQuery(id+"F18.opExtrude","SWEPT_BODY",BODY,{"disambiguationData":[OSD([sQuery(id+"F17.wireOp",EDGE,"E260.bottom"),sQuery(id+"F17.wireOp",EDGE,"E267.right"),sQuery(id+"F17.wireOp",EDGE,"E268.right"),sQuery(id+"F17.wireOp",EDGE,"E268.bottom")])]});
            var Q42;
            Q42=makeQuery(id+"F18.opExtrude","SWEPT_BODY",BODY,{"disambiguationData":[OSD([sQuery(id+"F17.wireOp",EDGE,"E249.bottom"),sQuery(id+"F17.wireOp",EDGE,"E258.right"),sQuery(id+"F17.wireOp",EDGE,"E259.right"),sQuery(id+"F17.wireOp",EDGE,"E259.bottom")])]});
            var Q43;
            Q43=makeQuery(id+"F18.opExtrude","SWEPT_BODY",BODY,{"disambiguationData":[OSD([sQuery(id+"F17.wireOp",EDGE,"E236.bottom"),sQuery(id+"F17.wireOp",EDGE,"E247.right"),sQuery(id+"F17.wireOp",EDGE,"E248.right"),sQuery(id+"F17.wireOp",EDGE,"E248.bottom")])]});
            var Q44;
            Q44=makeQuery(id+"FjME2WR4CrJvMWv_1.opExtrude","SWEPT_BODY",BODY,{"disambiguationData":[OSD([sQuery(id+"F17.wireOp",EDGE,"E268.bottom"),sQuery(id+"F17.wireOp",EDGE,"E273.right"),sQuery(id+"F17.wireOp",EDGE,"E274.right"),sQuery(id+"F17.wireOp",EDGE,"E274.bottom")])]});
            var Q45;
            Q45=makeQuery(id+"FjME2WR4CrJvMWv_1.opExtrude","SWEPT_BODY",BODY,{"disambiguationData":[OSD([sQuery(id+"F17.wireOp",EDGE,"E261.bottom"),sQuery(id+"F17.wireOp",EDGE,"E268.right"),sQuery(id+"F17.wireOp",EDGE,"E269.right"),sQuery(id+"F17.wireOp",EDGE,"E269.bottom")])]});
            var Q46;
            Q46=makeQuery(id+"FjME2WR4CrJvMWv_1.opExtrude","SWEPT_BODY",BODY,{"disambiguationData":[OSD([sQuery(id+"F17.wireOp",EDGE,"E250.bottom"),sQuery(id+"F17.wireOp",EDGE,"E259.right"),sQuery(id+"F17.wireOp",EDGE,"E260.right"),sQuery(id+"F17.wireOp",EDGE,"E260.bottom")])]});
            var Q47;
            Q47=makeQuery(id+"FjME2WR4CrJvMWv_1.opExtrude","SWEPT_BODY",BODY,{"disambiguationData":[OSD([sQuery(id+"F17.wireOp",EDGE,"E237.bottom"),sQuery(id+"F17.wireOp",EDGE,"E248.right"),sQuery(id+"F17.wireOp",EDGE,"E249.right"),sQuery(id+"F17.wireOp",EDGE,"E249.bottom")])]});
            var Q48;
            Q48=makeQuery(id+"F18.opExtrude","SWEPT_BODY",BODY,{"disambiguationData":[OSD([sQuery(id+"F17.wireOp",EDGE,"E269.bottom"),sQuery(id+"F17.wireOp",EDGE,"E274.right"),sQuery(id+"F17.wireOp",EDGE,"E284.bottom"),sQuery(id+"F17.wireOp",EDGE,"E293.right")])]});
            var Q49;
            Q49=makeQuery(id+"F18.opExtrude","SWEPT_BODY",BODY,{"disambiguationData":[OSD([sQuery(id+"F17.wireOp",EDGE,"E237.top"),sQuery(id+"F17.wireOp",EDGE,"E236.right"),sQuery(id+"F17.wireOp",EDGE,"E237.right"),sQuery(id+"F17.wireOp",EDGE,"E237.bottom")])]});
            var Q50;
            Q50=makeQuery(id+"FjME2WR4CrJvMWv_1.opExtrude","SWEPT_BODY",BODY,{"disambiguationData":[OSD([sQuery(id+"F17.wireOp",EDGE,"E238.top"),sQuery(id+"F17.wireOp",EDGE,"E237.right"),sQuery(id+"F17.wireOp",EDGE,"E238.right"),sQuery(id+"F17.wireOp",EDGE,"E238.bottom")])]});
            var Q51;
            Q51=makeQuery(id+"F18.opExtrude","SWEPT_BODY",BODY,{"disambiguationData":[OSD([sQuery(id+"F17.wireOp",EDGE,"E262.bottom"),sQuery(id+"F17.wireOp",EDGE,"E269.right"),sQuery(id+"F17.wireOp",EDGE,"E292.right"),sQuery(id+"F17.wireOp",EDGE,"E293.bottom")])]});
            var Q52;
            Q52=makeQuery(id+"F18.opExtrude","SWEPT_BODY",BODY,{"disambiguationData":[OSD([sQuery(id+"F17.wireOp",EDGE,"E251.bottom"),sQuery(id+"F17.wireOp",EDGE,"E260.right"),sQuery(id+"F17.wireOp",EDGE,"E261.right"),sQuery(id+"F17.wireOp",EDGE,"E261.bottom")])]});
            var Q53;
            Q53=makeQuery(id+"F18.opExtrude","SWEPT_BODY",BODY,{"disambiguationData":[OSD([sQuery(id+"F17.wireOp",EDGE,"E238.bottom"),sQuery(id+"F17.wireOp",EDGE,"E249.right"),sQuery(id+"F17.wireOp",EDGE,"E250.right"),sQuery(id+"F17.wireOp",EDGE,"E250.bottom")])]});
            var Q54;
            Q54=makeQuery(id+"FjME2WR4CrJvMWv_1.opExtrude","SWEPT_BODY",BODY,{"disambiguationData":[OSD([sQuery(id+"F17.wireOp",EDGE,"E292.bottom"),sQuery(id+"F17.wireOp",EDGE,"E292.right"),sQuery(id+"F17.wireOp",EDGE,"E292.top"),sQuery(id+"F17.wireOp",EDGE,"E302")])]});
            var Q55;
            Q55=makeQuery(id+"FjME2WR4CrJvMWv_1.opExtrude","SWEPT_BODY",BODY,{"disambiguationData":[OSD([sQuery(id+"F17.wireOp",EDGE,"E252.bottom"),sQuery(id+"F17.wireOp",EDGE,"E261.right"),sQuery(id+"F17.wireOp",EDGE,"E262.right"),sQuery(id+"F17.wireOp",EDGE,"E262.bottom")])]});
            var Q56;
            Q56=makeQuery(id+"FjME2WR4CrJvMWv_1.opExtrude","SWEPT_BODY",BODY,{"disambiguationData":[OSD([sQuery(id+"F17.wireOp",EDGE,"E239.bottom"),sQuery(id+"F17.wireOp",EDGE,"E250.right"),sQuery(id+"F17.wireOp",EDGE,"E251.right"),sQuery(id+"F17.wireOp",EDGE,"E251.bottom")])]});
            var Q57;
            Q57=makeQuery(id+"F18.opExtrude","SWEPT_BODY",BODY,{"disambiguationData":[OSD([sQuery(id+"F17.wireOp",EDGE,"E239.top"),sQuery(id+"F17.wireOp",EDGE,"E238.right"),sQuery(id+"F17.wireOp",EDGE,"E239.right"),sQuery(id+"F17.wireOp",EDGE,"E239.bottom")])]});
            var Q58;
            Q58=makeQuery(id+"FjME2WR4CrJvMWv_1.opExtrude","SWEPT_BODY",BODY,{"disambiguationData":[OSD([sQuery(id+"F17.wireOp",EDGE,"E240.top"),sQuery(id+"F17.wireOp",EDGE,"E239.right"),sQuery(id+"F17.wireOp",EDGE,"E240.right"),sQuery(id+"F17.wireOp",EDGE,"E240.bottom")])]});
            var Q59;
            Q59=makeQuery(id+"F18.opExtrude","SWEPT_BODY",BODY,{"disambiguationData":[OSD([sQuery(id+"F17.wireOp",EDGE,"E240.bottom"),sQuery(id+"F17.wireOp",EDGE,"E251.right"),sQuery(id+"F17.wireOp",EDGE,"E252.right"),sQuery(id+"F17.wireOp",EDGE,"E252.bottom")])]});
            var Q60;
            Q60=makeQuery(id+"FjME2WR4CrJvMWv_1.opExtrude","SWEPT_BODY",BODY,{"disambiguationData":[OSD([sQuery(id+"F17.wireOp",EDGE,"E241.bottom"),sQuery(id+"F17.wireOp",EDGE,"E252.right"),sQuery(id+"F17.wireOp",EDGE,"E253.right"),sQuery(id+"F17.wireOp",EDGE,"E253.bottom")])]});
            var Q61;
            Q61=makeQuery(id+"F18.opExtrude","SWEPT_BODY",BODY,{"disambiguationData":[OSD([sQuery(id+"F17.wireOp",EDGE,"E241.top"),sQuery(id+"F17.wireOp",EDGE,"E240.right"),sQuery(id+"F17.wireOp",EDGE,"E241.right"),sQuery(id+"F17.wireOp",EDGE,"E241.bottom")])]});
            var Q62;
            Q62=makeQuery(id+"FjME2WR4CrJvMWv_1.opExtrude","SWEPT_BODY",BODY,{"disambiguationData":[OSD([sQuery(id+"F17.wireOp",EDGE,"E242.top"),sQuery(id+"F17.wireOp",EDGE,"E241.right"),sQuery(id+"F17.wireOp",EDGE,"E242.right"),sQuery(id+"F17.wireOp",EDGE,"E242.bottom")])]});
            var Q63;
            Q63=makeQuery(id+"F18.opExtrude","SWEPT_BODY",BODY,{"disambiguationData":[OSD([sQuery(id+"F17.wireOp",EDGE,"E243.top"),sQuery(id+"F17.wireOp",EDGE,"E242.right"),sQuery(id+"F17.wireOp",EDGE,"E295.bottom"),sQuery(id+"F17.wireOp",EDGE,"E302")])]});
            var Q64;
            Q64=qCreatedBy(makeId("Right.planeOp"),FACE);
            transform(context, id + "F19", {"entities" : qUnion([Q0, Q1, Q2, Q3, Q4, Q5, Q6, Q7, Q8, Q9, Q10, Q11, Q12, Q13, Q14, Q15, Q16, Q17, Q18, Q19, Q20, Q21, Q22, Q23, Q24, Q25, Q26, Q27, Q28, Q29, Q30, Q31, Q32, Q33, Q34, Q35, Q36, Q37, Q38, Q39, Q40, Q41, Q42, Q43, Q44, Q45, Q46, Q47, Q48, Q49, Q50, Q51, Q52, Q53, Q54, Q55, Q56, Q57, Q58, Q59, Q60, Q61, Q62, Q63]), "transformType" : TransformType.TRANSLATION_DISTANCE, "transformDirection" : qUnion([Q64]), "distance" : 12.35 * mm, "oppositeDirection" : true, "makeCopy" : false});
        }
        {
            var Q0;
            Q0=makeQuery(id+"FjME2WR4CrJvMWv_1.opExtrude","SWEPT_BODY",BODY,{"disambiguationData":[OSD([sQuery(id+"F17.wireOp",EDGE,"E232.bottom"),sQuery(id+"F17.wireOp",EDGE,"E233.left"),sQuery(id+"F17.wireOp",EDGE,"E233.bottom"),sQuery(id+"F17.wireOp",EDGE,"E245.right"),sQuery(id+"F17.wireOp",EDGE,"E232.top"),sQuery(id+"F17.wireOp",EDGE,"E244.right"),sQuery(id+"F17.wireOp",EDGE,"E279.top"),sQuery(id+"F17.wireOp",EDGE,"E303")])]});
            var Q1;
            Q1=makeQuery(id+"FjME2WR4CrJvMWv_1.opExtrude","SWEPT_BODY",BODY,{"disambiguationData":[OSD([sQuery(id+"F17.wireOp",EDGE,"E246.bottom"),sQuery(id+"F17.wireOp",EDGE,"E256.right"),sQuery(id+"F17.wireOp",EDGE,"E255.right"),sQuery(id+"F17.wireOp",EDGE,"E280.top"),sQuery(id+"F17.wireOp",EDGE,"E303")])]});
            var Q2;
            Q2=makeQuery(id+"FjME2WR4CrJvMWv_1.opExtrude","SWEPT_BODY",BODY,{"disambiguationData":[OSD([sQuery(id+"F17.wireOp",EDGE,"E280.bottom"),sQuery(id+"F17.wireOp",EDGE,"E281.right"),sQuery(id+"F17.wireOp",EDGE,"E303")])]});
            var Q3;
            Q3=makeQuery(id+"F18.opExtrude","SWEPT_BODY",BODY,{"disambiguationData":[OSD([sQuery(id+"F17.wireOp",EDGE,"E281.top"),sQuery(id+"F17.wireOp",EDGE,"E271.right"),sQuery(id+"F17.wireOp",EDGE,"E281.right"),sQuery(id+"F17.wireOp",EDGE,"E281.bottom"),sQuery(id+"F17.wireOp",EDGE,"E303")])]});
            var Q4;
            Q4=makeQuery(id+"F18.opExtrude","SWEPT_BODY",BODY,{"disambiguationData":[OSD([sQuery(id+"F17.wireOp",EDGE,"E280.top"),sQuery(id+"F17.wireOp",EDGE,"E264.right"),sQuery(id+"F17.wireOp",EDGE,"E280.bottom"),sQuery(id+"F17.wireOp",EDGE,"E303")])]});
            var Q5;
            Q5=makeQuery(id+"F18.opExtrude","SWEPT_BODY",BODY,{"disambiguationData":[OSD([sQuery(id+"F17.wireOp",EDGE,"E272.bottom"),sQuery(id+"F17.wireOp",EDGE,"E282.right"),sQuery(id+"F17.wireOp",EDGE,"E282.top"),sQuery(id+"F17.wireOp",EDGE,"E297.left"),sQuery(id+"F17.wireOp",EDGE,"E303")])]});
            var Q6;
            Q6=makeQuery(id+"F18.opExtrude","SWEPT_BODY",BODY,{"disambiguationData":[OSD([sQuery(id+"F17.wireOp",EDGE,"E279.top"),sQuery(id+"F17.wireOp",EDGE,"E255.right"),sQuery(id+"F17.wireOp",EDGE,"E303")])]});
            var Q7;
            Q7=makeQuery(id+"F18.opExtrude","SWEPT_BODY",BODY,{"disambiguationData":[OSD([sQuery(id+"F17.wireOp",EDGE,"E232.top"),sQuery(id+"F17.wireOp",EDGE,"E244.right"),sQuery(id+"F17.wireOp",EDGE,"E303")])]});
            var Q8;
            Q8=makeQuery(id+"FjME2WR4CrJvMWv_1.opExtrude","SWEPT_BODY",BODY,{"disambiguationData":[OSD([sQuery(id+"F17.wireOp",EDGE,"E281.bottom"),sQuery(id+"F17.wireOp",EDGE,"E297.left"),sQuery(id+"F17.wireOp",EDGE,"E303")])]});
            var Q9;
            Q9=makeQuery(id+"F18.opExtrude","SWEPT_BODY",BODY,{"disambiguationData":[OSD([sQuery(id+"F17.wireOp",EDGE,"E301.bottom"),sQuery(id+"F17.wireOp",EDGE,"E301.right"),sQuery(id+"F17.wireOp",EDGE,"E303")])]});
            var Q10;
            Q10=makeQuery(id+"FjME2WR4CrJvMWv_1.opExtrude","SWEPT_BODY",BODY,{"disambiguationData":[OSD([sQuery(id+"F17.wireOp",EDGE,"E290.top"),sQuery(id+"F17.wireOp",EDGE,"E301.right"),sQuery(id+"F17.wireOp",EDGE,"E302")])]});
            var Q11;
            Q11=makeQuery(id+"FjME2WR4CrJvMWv_1.opExtrude","SWEPT_BODY",BODY,{"disambiguationData":[OSD([sQuery(id+"F17.wireOp",EDGE,"E282.top"),sQuery(id+"F17.wireOp",EDGE,"E285.left"),sQuery(id+"F17.wireOp",EDGE,"E300.bottom"),sQuery(id+"F17.wireOp",EDGE,"E303")])]});
            var Q12;
            Q12=makeQuery(id+"FjME2WR4CrJvMWv_1.opExtrude","SWEPT_BODY",BODY,{"disambiguationData":[OSD([sQuery(id+"F17.wireOp",EDGE,"E289.bottom"),sQuery(id+"F17.wireOp",EDGE,"E289.left"),sQuery(id+"F17.wireOp",EDGE,"E288.right"),sQuery(id+"F17.wireOp",EDGE,"E301.bottom"),sQuery(id+"F17.wireOp",EDGE,"E303")])]});
            var Q13;
            Q13=makeQuery(id+"FjME2WR4CrJvMWv_1.opExtrude","SWEPT_BODY",BODY,{"disambiguationData":[OSD([sQuery(id+"F17.wireOp",EDGE,"E299.bottom"),sQuery(id+"F17.wireOp",EDGE,"E290.left"),sQuery(id+"F17.wireOp",EDGE,"E302")])]});
            var Q14;
            Q14=makeQuery(id+"F18.opExtrude","SWEPT_BODY",BODY,{"disambiguationData":[OSD([sQuery(id+"F17.wireOp",EDGE,"E290.bottom"),sQuery(id+"F17.wireOp",EDGE,"E289.left"),sQuery(id+"F17.wireOp",EDGE,"E290.left"),sQuery(id+"F17.wireOp",EDGE,"E290.top"),sQuery(id+"F17.wireOp",EDGE,"E302")])]});
            var Q15;
            Q15=makeQuery(id+"FjME2WR4CrJvMWv_1.opExtrude","SWEPT_BODY",BODY,{"disambiguationData":[OSD([sQuery(id+"F17.wireOp",EDGE,"E266.bottom"),sQuery(id+"F17.wireOp",EDGE,"E272.right"),sQuery(id+"F17.wireOp",EDGE,"E271.right"),sQuery(id+"F17.wireOp",EDGE,"E272.bottom")])]});
            var Q16;
            Q16=makeQuery(id+"FjME2WR4CrJvMWv_1.opExtrude","SWEPT_BODY",BODY,{"disambiguationData":[OSD([sQuery(id+"F17.wireOp",EDGE,"E257.bottom"),sQuery(id+"F17.wireOp",EDGE,"E265.right"),sQuery(id+"F17.wireOp",EDGE,"E264.right"),sQuery(id+"F17.wireOp",EDGE,"E281.top")])]});
            var Q17;
            Q17=makeQuery(id+"F18.opExtrude","SWEPT_BODY",BODY,{"disambiguationData":[OSD([sQuery(id+"F17.wireOp",EDGE,"E233.top"),sQuery(id+"F17.wireOp",EDGE,"E233.left"),sQuery(id+"F17.wireOp",EDGE,"E233.right"),sQuery(id+"F17.wireOp",EDGE,"E233.bottom")])]});
            var Q18;
            Q18=makeQuery(id+"F18.opExtrude","SWEPT_BODY",BODY,{"disambiguationData":[OSD([sQuery(id+"F17.wireOp",EDGE,"E277.bottom"),sQuery(id+"F17.wireOp",EDGE,"E285.left"),sQuery(id+"F17.wireOp",EDGE,"E285.right"),sQuery(id+"F17.wireOp",EDGE,"E289.bottom")])]});
            var Q19;
            Q19=makeQuery(id+"F18.opExtrude","SWEPT_BODY",BODY,{"disambiguationData":[OSD([sQuery(id+"F17.wireOp",EDGE,"E247.bottom"),sQuery(id+"F17.wireOp",EDGE,"E256.right"),sQuery(id+"F17.wireOp",EDGE,"E257.right"),sQuery(id+"F17.wireOp",EDGE,"E257.bottom")])]});
            var Q20;
            Q20=makeQuery(id+"F18.opExtrude","SWEPT_BODY",BODY,{"disambiguationData":[OSD([sQuery(id+"F17.wireOp",EDGE,"E234.bottom"),sQuery(id+"F17.wireOp",EDGE,"E245.right"),sQuery(id+"F17.wireOp",EDGE,"E246.right"),sQuery(id+"F17.wireOp",EDGE,"E246.bottom")])]});
            var Q21;
            Q21=makeQuery(id+"FjME2WR4CrJvMWv_1.opExtrude","SWEPT_BODY",BODY,{"disambiguationData":[OSD([sQuery(id+"F17.wireOp",EDGE,"E284.bottom"),sQuery(id+"F17.wireOp",EDGE,"E284.right"),sQuery(id+"F17.wireOp",EDGE,"E294.right"),sQuery(id+"F17.wireOp",EDGE,"E287.top"),sQuery(id+"F17.wireOp",EDGE,"E302")])]});
            var Q22;
            Q22=makeQuery(id+"FjME2WR4CrJvMWv_1.opExtrude","SWEPT_BODY",BODY,{"disambiguationData":[OSD([sQuery(id+"F17.wireOp",EDGE,"E273.bottom"),sQuery(id+"F17.wireOp",EDGE,"E277.right"),sQuery(id+"F17.wireOp",EDGE,"E282.right"),sQuery(id+"F17.wireOp",EDGE,"E277.bottom")])]});
            var Q23;
            Q23=makeQuery(id+"FjME2WR4CrJvMWv_1.opExtrude","SWEPT_BODY",BODY,{"disambiguationData":[OSD([sQuery(id+"F17.wireOp",EDGE,"E293.bottom"),sQuery(id+"F17.wireOp",EDGE,"E293.right"),sQuery(id+"F17.wireOp",EDGE,"E293.left"),sQuery(id+"F17.wireOp",EDGE,"E293.top"),sQuery(id+"F17.wireOp",EDGE,"E302")])]});
            var Q24;
            Q24=makeQuery(id+"FjME2WR4CrJvMWv_1.opExtrude","SWEPT_BODY",BODY,{"disambiguationData":[OSD([sQuery(id+"F17.wireOp",EDGE,"E291.bottom"),sQuery(id+"F17.wireOp",EDGE,"E291.right"),sQuery(id+"F17.wireOp",EDGE,"E302")])]});
            var Q25;
            Q25=makeQuery(id+"FjME2WR4CrJvMWv_1.opExtrude","SWEPT_BODY",BODY,{"disambiguationData":[OSD([sQuery(id+"F17.wireOp",EDGE,"E295.bottom"),sQuery(id+"F17.wireOp",EDGE,"E295.right"),sQuery(id+"F17.wireOp",EDGE,"E302")])]});
            var Q26;
            Q26=makeQuery(id+"FjME2WR4CrJvMWv_1.opExtrude","SWEPT_BODY",BODY,{"disambiguationData":[OSD([sQuery(id+"F17.wireOp",EDGE,"E235.bottom"),sQuery(id+"F17.wireOp",EDGE,"E246.right"),sQuery(id+"F17.wireOp",EDGE,"E247.right"),sQuery(id+"F17.wireOp",EDGE,"E247.bottom")])]});
            var Q27;
            Q27=makeQuery(id+"FjME2WR4CrJvMWv_1.opExtrude","SWEPT_BODY",BODY,{"disambiguationData":[OSD([sQuery(id+"F17.wireOp",EDGE,"E248.bottom"),sQuery(id+"F17.wireOp",EDGE,"E257.right"),sQuery(id+"F17.wireOp",EDGE,"E258.right"),sQuery(id+"F17.wireOp",EDGE,"E258.bottom")])]});
            var Q28;
            Q28=makeQuery(id+"FjME2WR4CrJvMWv_1.opExtrude","SWEPT_BODY",BODY,{"disambiguationData":[OSD([sQuery(id+"F17.wireOp",EDGE,"E234.top"),sQuery(id+"F17.wireOp",EDGE,"E233.right"),sQuery(id+"F17.wireOp",EDGE,"E234.right"),sQuery(id+"F17.wireOp",EDGE,"E234.bottom")])]});
            var Q29;
            Q29=makeQuery(id+"F18.opExtrude","SWEPT_BODY",BODY,{"disambiguationData":[OSD([sQuery(id+"F17.wireOp",EDGE,"E293.top"),sQuery(id+"F17.wireOp",EDGE,"E294.right"),sQuery(id+"F17.wireOp",EDGE,"E302")])]});
            var Q30;
            Q30=makeQuery(id+"F18.opExtrude","SWEPT_BODY",BODY,{"disambiguationData":[OSD([sQuery(id+"F17.wireOp",EDGE,"E274.bottom"),sQuery(id+"F17.wireOp",EDGE,"E277.right"),sQuery(id+"F17.wireOp",EDGE,"E284.right"),sQuery(id+"F17.wireOp",EDGE,"E278.bottom")])]});
            var Q31;
            Q31=makeQuery(id+"F18.opExtrude","SWEPT_BODY",BODY,{"disambiguationData":[OSD([sQuery(id+"F17.wireOp",EDGE,"E267.bottom"),sQuery(id+"F17.wireOp",EDGE,"E272.right"),sQuery(id+"F17.wireOp",EDGE,"E273.right"),sQuery(id+"F17.wireOp",EDGE,"E273.bottom")])]});
            var Q32;
            Q32=makeQuery(id+"F18.opExtrude","SWEPT_BODY",BODY,{"disambiguationData":[OSD([sQuery(id+"F17.wireOp",EDGE,"E253.bottom"),sQuery(id+"F17.wireOp",EDGE,"E262.right"),sQuery(id+"F17.wireOp",EDGE,"E292.bottom"),sQuery(id+"F17.wireOp",EDGE,"E291.right"),sQuery(id+"F17.wireOp",EDGE,"E302")])]});
            var Q33;
            Q33=makeQuery(id+"F18.opExtrude","SWEPT_BODY",BODY,{"disambiguationData":[OSD([sQuery(id+"F17.wireOp",EDGE,"E258.bottom"),sQuery(id+"F17.wireOp",EDGE,"E265.right"),sQuery(id+"F17.wireOp",EDGE,"E266.right"),sQuery(id+"F17.wireOp",EDGE,"E266.bottom")])]});
            var Q34;
            Q34=makeQuery(id+"F18.opExtrude","SWEPT_BODY",BODY,{"disambiguationData":[OSD([sQuery(id+"F17.wireOp",EDGE,"E242.bottom"),sQuery(id+"F17.wireOp",EDGE,"E253.right"),sQuery(id+"F17.wireOp",EDGE,"E291.bottom"),sQuery(id+"F17.wireOp",EDGE,"E295.right"),sQuery(id+"F17.wireOp",EDGE,"E302")])]});
            var Q35;
            Q35=makeQuery(id+"F18.opExtrude","SWEPT_BODY",BODY,{"disambiguationData":[OSD([sQuery(id+"F17.wireOp",EDGE,"E292.top"),sQuery(id+"F17.wireOp",EDGE,"E293.left"),sQuery(id+"F17.wireOp",EDGE,"E302")])]});
            var Q36;
            Q36=makeQuery(id+"FjME2WR4CrJvMWv_1.opExtrude","SWEPT_BODY",BODY,{"disambiguationData":[OSD([sQuery(id+"F17.wireOp",EDGE,"E278.bottom"),sQuery(id+"F17.wireOp",EDGE,"E285.right"),sQuery(id+"F17.wireOp",EDGE,"E290.bottom"),sQuery(id+"F17.wireOp",EDGE,"E286.right")])]});
            var Q37;
            Q37=makeQuery(id+"FjME2WR4CrJvMWv_1.opExtrude","SWEPT_BODY",BODY,{"disambiguationData":[OSD([sQuery(id+"F17.wireOp",EDGE,"E259.bottom"),sQuery(id+"F17.wireOp",EDGE,"E266.right"),sQuery(id+"F17.wireOp",EDGE,"E267.right"),sQuery(id+"F17.wireOp",EDGE,"E267.bottom")])]});
            var Q38;
            Q38=makeQuery(id+"F18.opExtrude","SWEPT_BODY",BODY,{"disambiguationData":[OSD([sQuery(id+"F17.wireOp",EDGE,"E249.bottom"),sQuery(id+"F17.wireOp",EDGE,"E258.right"),sQuery(id+"F17.wireOp",EDGE,"E259.right"),sQuery(id+"F17.wireOp",EDGE,"E259.bottom")])]});
            var Q39;
            Q39=makeQuery(id+"F18.opExtrude","SWEPT_BODY",BODY,{"disambiguationData":[OSD([sQuery(id+"F17.wireOp",EDGE,"E236.bottom"),sQuery(id+"F17.wireOp",EDGE,"E247.right"),sQuery(id+"F17.wireOp",EDGE,"E248.right"),sQuery(id+"F17.wireOp",EDGE,"E248.bottom")])]});
            var Q40;
            Q40=makeQuery(id+"F18.opExtrude","SWEPT_BODY",BODY,{"disambiguationData":[OSD([sQuery(id+"F17.wireOp",EDGE,"E235.top"),sQuery(id+"F17.wireOp",EDGE,"E234.right"),sQuery(id+"F17.wireOp",EDGE,"E235.right"),sQuery(id+"F17.wireOp",EDGE,"E235.bottom")])]});
            var Q41;
            Q41=makeQuery(id+"F18.opExtrude","SWEPT_BODY",BODY,{"disambiguationData":[OSD([sQuery(id+"F17.wireOp",EDGE,"E287.top"),sQuery(id+"F17.wireOp",EDGE,"E286.right"),sQuery(id+"F17.wireOp",EDGE,"E299.bottom"),sQuery(id+"F17.wireOp",EDGE,"E302")])]});
            var Q42;
            Q42=makeQuery(id+"FjME2WR4CrJvMWv_1.opExtrude","SWEPT_BODY",BODY,{"disambiguationData":[OSD([sQuery(id+"F17.wireOp",EDGE,"E268.bottom"),sQuery(id+"F17.wireOp",EDGE,"E273.right"),sQuery(id+"F17.wireOp",EDGE,"E274.right"),sQuery(id+"F17.wireOp",EDGE,"E274.bottom")])]});
            var Q43;
            Q43=makeQuery(id+"FjME2WR4CrJvMWv_1.opExtrude","SWEPT_BODY",BODY,{"disambiguationData":[OSD([sQuery(id+"F17.wireOp",EDGE,"E236.top"),sQuery(id+"F17.wireOp",EDGE,"E235.right"),sQuery(id+"F17.wireOp",EDGE,"E236.right"),sQuery(id+"F17.wireOp",EDGE,"E236.bottom")])]});
            var Q44;
            Q44=makeQuery(id+"FjME2WR4CrJvMWv_1.opExtrude","SWEPT_BODY",BODY,{"disambiguationData":[OSD([sQuery(id+"F17.wireOp",EDGE,"E250.bottom"),sQuery(id+"F17.wireOp",EDGE,"E259.right"),sQuery(id+"F17.wireOp",EDGE,"E260.right"),sQuery(id+"F17.wireOp",EDGE,"E260.bottom")])]});
            var Q45;
            Q45=makeQuery(id+"FjME2WR4CrJvMWv_1.opExtrude","SWEPT_BODY",BODY,{"disambiguationData":[OSD([sQuery(id+"F17.wireOp",EDGE,"E237.bottom"),sQuery(id+"F17.wireOp",EDGE,"E248.right"),sQuery(id+"F17.wireOp",EDGE,"E249.right"),sQuery(id+"F17.wireOp",EDGE,"E249.bottom")])]});
            var Q46;
            Q46=makeQuery(id+"F18.opExtrude","SWEPT_BODY",BODY,{"disambiguationData":[OSD([sQuery(id+"F17.wireOp",EDGE,"E269.bottom"),sQuery(id+"F17.wireOp",EDGE,"E274.right"),sQuery(id+"F17.wireOp",EDGE,"E284.bottom"),sQuery(id+"F17.wireOp",EDGE,"E293.right")])]});
            var Q47;
            Q47=makeQuery(id+"F18.opExtrude","SWEPT_BODY",BODY,{"disambiguationData":[OSD([sQuery(id+"F17.wireOp",EDGE,"E260.bottom"),sQuery(id+"F17.wireOp",EDGE,"E267.right"),sQuery(id+"F17.wireOp",EDGE,"E268.right"),sQuery(id+"F17.wireOp",EDGE,"E268.bottom")])]});
            var Q48;
            Q48=makeQuery(id+"FjME2WR4CrJvMWv_1.opExtrude","SWEPT_BODY",BODY,{"disambiguationData":[OSD([sQuery(id+"F17.wireOp",EDGE,"E261.bottom"),sQuery(id+"F17.wireOp",EDGE,"E268.right"),sQuery(id+"F17.wireOp",EDGE,"E269.right"),sQuery(id+"F17.wireOp",EDGE,"E269.bottom")])]});
            var Q49;
            Q49=makeQuery(id+"F18.opExtrude","SWEPT_BODY",BODY,{"disambiguationData":[OSD([sQuery(id+"F17.wireOp",EDGE,"E251.bottom"),sQuery(id+"F17.wireOp",EDGE,"E260.right"),sQuery(id+"F17.wireOp",EDGE,"E261.right"),sQuery(id+"F17.wireOp",EDGE,"E261.bottom")])]});
            var Q50;
            Q50=makeQuery(id+"F18.opExtrude","SWEPT_BODY",BODY,{"disambiguationData":[OSD([sQuery(id+"F17.wireOp",EDGE,"E238.bottom"),sQuery(id+"F17.wireOp",EDGE,"E249.right"),sQuery(id+"F17.wireOp",EDGE,"E250.right"),sQuery(id+"F17.wireOp",EDGE,"E250.bottom")])]});
            var Q51;
            Q51=makeQuery(id+"F18.opExtrude","SWEPT_BODY",BODY,{"disambiguationData":[OSD([sQuery(id+"F17.wireOp",EDGE,"E237.top"),sQuery(id+"F17.wireOp",EDGE,"E236.right"),sQuery(id+"F17.wireOp",EDGE,"E237.right"),sQuery(id+"F17.wireOp",EDGE,"E237.bottom")])]});
            var Q52;
            Q52=makeQuery(id+"FjME2WR4CrJvMWv_1.opExtrude","SWEPT_BODY",BODY,{"disambiguationData":[OSD([sQuery(id+"F17.wireOp",EDGE,"E238.top"),sQuery(id+"F17.wireOp",EDGE,"E237.right"),sQuery(id+"F17.wireOp",EDGE,"E238.right"),sQuery(id+"F17.wireOp",EDGE,"E238.bottom")])]});
            var Q53;
            Q53=makeQuery(id+"FjME2WR4CrJvMWv_1.opExtrude","SWEPT_BODY",BODY,{"disambiguationData":[OSD([sQuery(id+"F17.wireOp",EDGE,"E252.bottom"),sQuery(id+"F17.wireOp",EDGE,"E261.right"),sQuery(id+"F17.wireOp",EDGE,"E262.right"),sQuery(id+"F17.wireOp",EDGE,"E262.bottom")])]});
            var Q54;
            Q54=makeQuery(id+"FjME2WR4CrJvMWv_1.opExtrude","SWEPT_BODY",BODY,{"disambiguationData":[OSD([sQuery(id+"F17.wireOp",EDGE,"E239.bottom"),sQuery(id+"F17.wireOp",EDGE,"E250.right"),sQuery(id+"F17.wireOp",EDGE,"E251.right"),sQuery(id+"F17.wireOp",EDGE,"E251.bottom")])]});
            var Q55;
            Q55=makeQuery(id+"F18.opExtrude","SWEPT_BODY",BODY,{"disambiguationData":[OSD([sQuery(id+"F17.wireOp",EDGE,"E262.bottom"),sQuery(id+"F17.wireOp",EDGE,"E269.right"),sQuery(id+"F17.wireOp",EDGE,"E292.right"),sQuery(id+"F17.wireOp",EDGE,"E293.bottom")])]});
            var Q56;
            Q56=makeQuery(id+"FjME2WR4CrJvMWv_1.opExtrude","SWEPT_BODY",BODY,{"disambiguationData":[OSD([sQuery(id+"F17.wireOp",EDGE,"E292.bottom"),sQuery(id+"F17.wireOp",EDGE,"E292.right"),sQuery(id+"F17.wireOp",EDGE,"E292.top"),sQuery(id+"F17.wireOp",EDGE,"E302")])]});
            var Q57;
            Q57=makeQuery(id+"F18.opExtrude","SWEPT_BODY",BODY,{"disambiguationData":[OSD([sQuery(id+"F17.wireOp",EDGE,"E240.bottom"),sQuery(id+"F17.wireOp",EDGE,"E251.right"),sQuery(id+"F17.wireOp",EDGE,"E252.right"),sQuery(id+"F17.wireOp",EDGE,"E252.bottom")])]});
            var Q58;
            Q58=makeQuery(id+"F18.opExtrude","SWEPT_BODY",BODY,{"disambiguationData":[OSD([sQuery(id+"F17.wireOp",EDGE,"E239.top"),sQuery(id+"F17.wireOp",EDGE,"E238.right"),sQuery(id+"F17.wireOp",EDGE,"E239.right"),sQuery(id+"F17.wireOp",EDGE,"E239.bottom")])]});
            var Q59;
            Q59=makeQuery(id+"FjME2WR4CrJvMWv_1.opExtrude","SWEPT_BODY",BODY,{"disambiguationData":[OSD([sQuery(id+"F17.wireOp",EDGE,"E240.top"),sQuery(id+"F17.wireOp",EDGE,"E239.right"),sQuery(id+"F17.wireOp",EDGE,"E240.right"),sQuery(id+"F17.wireOp",EDGE,"E240.bottom")])]});
            var Q60;
            Q60=makeQuery(id+"FjME2WR4CrJvMWv_1.opExtrude","SWEPT_BODY",BODY,{"disambiguationData":[OSD([sQuery(id+"F17.wireOp",EDGE,"E241.bottom"),sQuery(id+"F17.wireOp",EDGE,"E252.right"),sQuery(id+"F17.wireOp",EDGE,"E253.right"),sQuery(id+"F17.wireOp",EDGE,"E253.bottom")])]});
            var Q61;
            Q61=makeQuery(id+"F18.opExtrude","SWEPT_BODY",BODY,{"disambiguationData":[OSD([sQuery(id+"F17.wireOp",EDGE,"E241.top"),sQuery(id+"F17.wireOp",EDGE,"E240.right"),sQuery(id+"F17.wireOp",EDGE,"E241.right"),sQuery(id+"F17.wireOp",EDGE,"E241.bottom")])]});
            var Q62;
            Q62=makeQuery(id+"FjME2WR4CrJvMWv_1.opExtrude","SWEPT_BODY",BODY,{"disambiguationData":[OSD([sQuery(id+"F17.wireOp",EDGE,"E242.top"),sQuery(id+"F17.wireOp",EDGE,"E241.right"),sQuery(id+"F17.wireOp",EDGE,"E242.right"),sQuery(id+"F17.wireOp",EDGE,"E242.bottom")])]});
            var Q63;
            Q63=makeQuery(id+"F18.opExtrude","SWEPT_BODY",BODY,{"disambiguationData":[OSD([sQuery(id+"F17.wireOp",EDGE,"E243.top"),sQuery(id+"F17.wireOp",EDGE,"E242.right"),sQuery(id+"F17.wireOp",EDGE,"E295.bottom"),sQuery(id+"F17.wireOp",EDGE,"E302")])]});
            var Q64;
            Q64=makeQuery(id+"F18.opExtrude","CAP_EDGE",EDGE,{"disambiguationData":[OSD([sQuery(id+"F17.wireOp",EDGE,"E239.top")])],"isStart":false});
            transform(context, id + "F20", {"entities" : qUnion([Q0, Q1, Q2, Q3, Q4, Q5, Q6, Q7, Q8, Q9, Q10, Q11, Q12, Q13, Q14, Q15, Q16, Q17, Q18, Q19, Q20, Q21, Q22, Q23, Q24, Q25, Q26, Q27, Q28, Q29, Q30, Q31, Q32, Q33, Q34, Q35, Q36, Q37, Q38, Q39, Q40, Q41, Q42, Q43, Q44, Q45, Q46, Q47, Q48, Q49, Q50, Q51, Q52, Q53, Q54, Q55, Q56, Q57, Q58, Q59, Q60, Q61, Q62, Q63]), "transformType" : TransformType.ROTATION, "transformAxis" : qUnion([Q64]), "angle" : 45 * degree, "oppositeDirection" : true, "makeCopy" : false});
        }
    });
